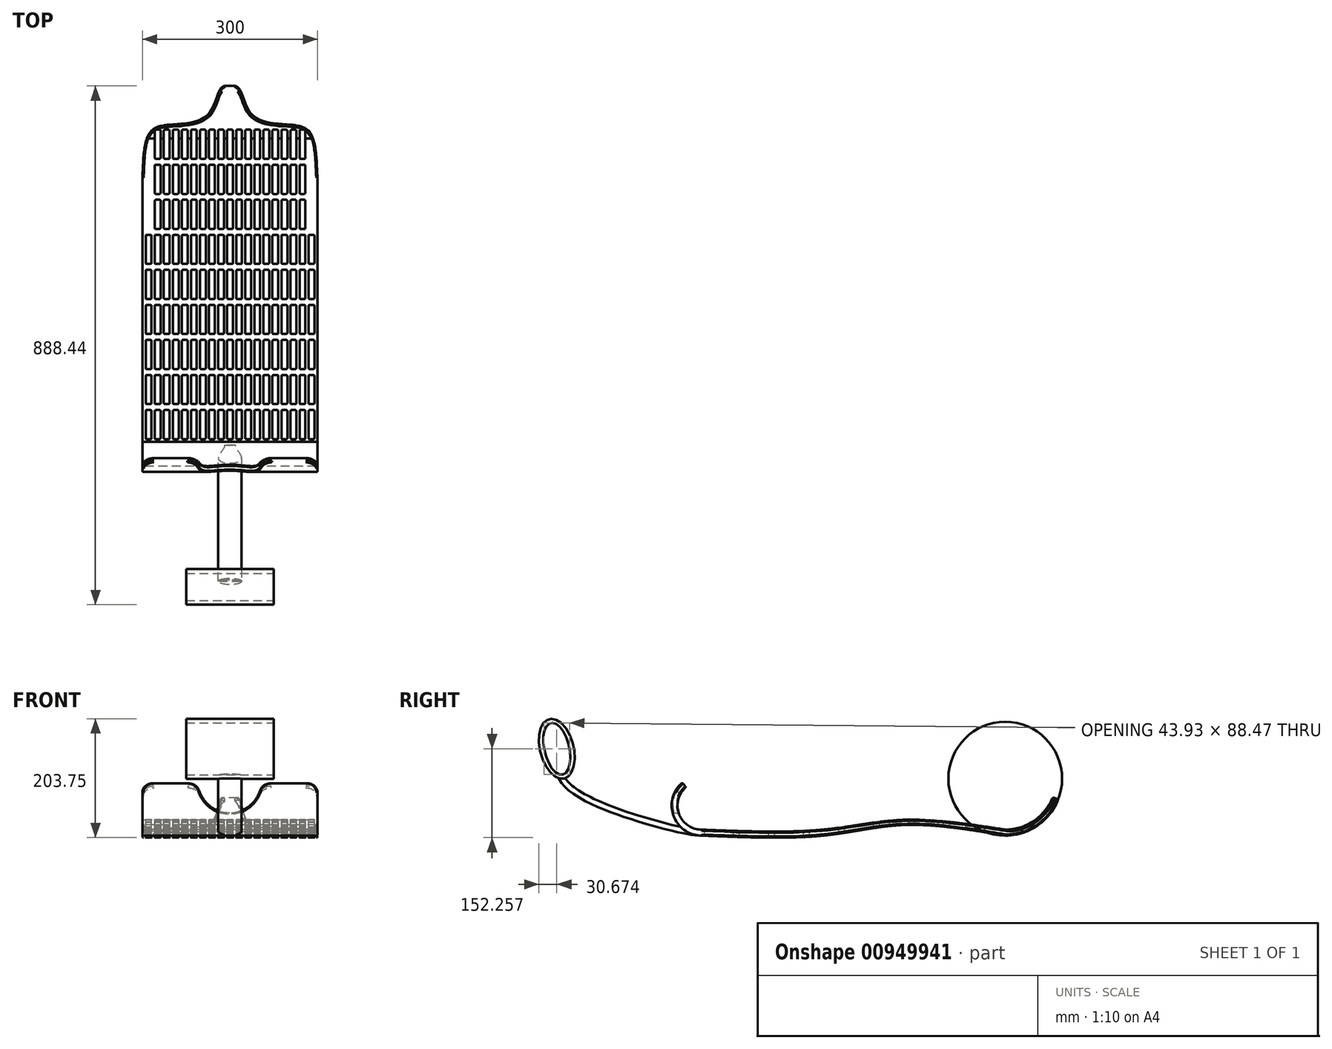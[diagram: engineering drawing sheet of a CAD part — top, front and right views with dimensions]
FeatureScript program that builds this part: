
annotation { "Feature Type Name" : "Feature", "Feature Type Description" : "" }
export const myFeature = defineFeature(function(context is Context, id is Id, definition is map)
    precondition{}
    {
        {
            var Q0;
            Q0=qCreatedBy(makeId("Right.planeOp"),FACE);
            var sketch = newSketch(context, id + "F0", { "sketchPlane" : qUnion([Q0])});
            skArc(sketch, "E0", {"start": v(0, 0) * mm, "mid": v(54.84, 16.9) * mm, "end": v(90.64, 61.76) * mm});
            skArc(sketch, "E1", {"start": v(-520, 0) * mm, "mid": v(-568.17, 33.63) * mm, "end": v(-553.2, 90.44) * mm});
            skArc(sketch, "E2.0", {"start": v(-520, 10) * mm, "mid": v(-558.78, 37.08) * mm, "end": v(-546.73, 82.82) * mm});
            skArc(sketch, "E2.2", {"start": v(0, 10) * mm, "mid": v(49.2, 25.17) * mm, "end": v(81.33, 65.42) * mm});
            skLineSegment(sketch, "E3", {"start": v(-553.2, 90.44) * mm, "end": v(-546.73, 82.82) * mm});
            skLineSegment(sketch, "E4", {"start": v(81.33, 65.42) * mm, "end": v(90.64, 61.76) * mm});
            skFitSpline(sketch, "E5", {"points": [v(-520, 10) * mm, v(-313.28, 10) * mm, v(-172.96, 26.9) * mm, v(0, 10) * mm], "startDerivative": vector(600.12, -23.53) * mm, "endDerivative": vector(538.4, -83.7) * mm});
            skFitSpline(sketch, "E6", {"points": [v(-520, 0) * mm, v(-310.97, 0) * mm, v(-172.96, 18.13) * mm, v(0, 0) * mm], "startDerivative": vector(605.75, -25.5) * mm, "endDerivative": vector(539.73, -90) * mm});
            skSolve(sketch);
        }
        {
            var Q0;
            Q0=makeQuery(id+"F0.imprint","IMPRINT",FACE,{"disambiguationData":[TD([[makeQuery(id+"F0.imprint","IMPRINT",EDGE,{"derivedFrom":sQuery(id+"F0.wireOp",EDGE,"GC1lfuyi-SQlX-Y11Y-IKv3-B2b0vn97BP75")}),-1.0]])]});
            var Q1;
            Q1=makeQuery(id+"F0.imprint","IMPRINT",FACE,{"disambiguationData":[TD([[makeQuery(id+"F0.imprint","IMPRINT",EDGE,{"derivedFrom":sQuery(id+"F0.wireOp",EDGE,"E0")}),1.0]])]});
            extrude(context, id + "F1", {"entities" : qUnion([Q0, Q1]), "depth" : 300 * mm, "offsetDistance" : 25 * mm});
        }
        {
            var Q0;
            Q0=qCreatedBy(makeId("Front.planeOp"),FACE);
            var sketch = newSketch(context, id + "F2", { "sketchPlane" : qUnion([Q0])});
            skCircle(sketch, "E7", {"center": v(149.46, 93.55) * mm, "radius": 54.72 * mm});
            skSolve(sketch);
        }
        {
            var Q0;
            Q0 = qSketchRegion(id + "F2", true);
            extrude(context, id + "F3", {"entities" : qUnion([Q0]), "operationType" : NewBodyOperationType.REMOVE, "endBound" : BoundingType.THROUGH_ALL, "depth" : 25 * mm, "offsetDistance" : 25 * mm});
        }
        {
            var Q0;
            Q0=makeQuery(id+"F3.boolean.opBoolean","INTERSECT",EDGE,{"disambiguationData":[OD(0.0)],"derivedFrom":[makeQuery(id+"F1.opExtrude","SWEPT_FACE",FACE,{"disambiguationData":[OSD([sQuery(id+"F0.wireOp",EDGE,"E3")])]}),makeQuery(id+"F3.opExtrude","SWEPT_FACE",FACE,{"disambiguationData":[OSD([sQuery(id+"F2.wireOp",EDGE,"E7")])]})]});
            var Q1;
            Q1=makeQuery(id+"F3.boolean.opBoolean","INTERSECT",EDGE,{"disambiguationData":[OD(1.0)],"derivedFrom":[makeQuery(id+"F1.opExtrude","SWEPT_FACE",FACE,{"disambiguationData":[OSD([sQuery(id+"F0.wireOp",EDGE,"E3")])]}),makeQuery(id+"F3.opExtrude","SWEPT_FACE",FACE,{"disambiguationData":[OSD([sQuery(id+"F2.wireOp",EDGE,"E7")])]})]});
            fillet(context, id + "F4", {"entities" : qUnion([Q0, Q1]), "radius" : 20 * mm, "tangentPropagation" : true, "allowEdgeOverflow" : false});
        }
        {
            var Q0;
            Q0=makeQuery(id+"F1.opExtrude","CAP_EDGE",EDGE,{"disambiguationData":[OSD([sQuery(id+"F0.wireOp",EDGE,"E3")])],"isStart":false});
            var Q1;
            Q1=makeQuery(id+"F1.opExtrude","CAP_EDGE",EDGE,{"disambiguationData":[OSD([sQuery(id+"F0.wireOp",EDGE,"E3")])],"isStart":true});
            fillet(context, id + "F5", {"entities" : qUnion([Q0, Q1]), "radius" : 20 * mm, "tangentPropagation" : true, "allowEdgeOverflow" : false});
        }
        {
            var Q0;
            Q0=qCreatedBy(makeId("Front.planeOp"),FACE);
            cPlane(context, id + "F6", {"entities" : qUnion([Q0]), "cplaneType" : CPlaneType.OFFSET, "offset" : 526 * mm, "width" : 150 * mm, "height" : 150 * mm});
        }
        {
            var Q0;
            Q0=qCreatedBy(makeId("Right.planeOp"),FACE);
            cPlane(context, id + "F7", {"entities" : qUnion([Q0]), "cplaneType" : CPlaneType.OFFSET, "offset" : 150 * mm, "width" : 150 * mm, "height" : 150 * mm});
        }
        {
            var Q0;
            Q0=qCreatedBy(id+"F7.planeOp",FACE);
            var sketch = newSketch(context, id + "F8", { "sketchPlane" : qUnion([Q0])});
            skFitSpline(sketch, "E8", {"points": [v(-525.68, 4.57) * mm, v(-580.72, 15.5) * mm, v(-760.94, 103.52) * mm], "startDerivative": vector(-124.59, 16.55) * mm, "endDerivative": vector(-36.47, 177.5) * mm});
            skSolve(sketch);
        }
        {
            var Q0;
            Q0=qCreatedBy(id+"F6.planeOp",FACE);
            var sketch = newSketch(context, id + "F9", { "sketchPlane" : qUnion([Q0])});
            skEllipse(sketch, "E9", {"center": v(150.13, 4.74) * mm, "majorRadius": 20 * mm, "minorRadius": 5 * mm, "majorAxis": v(1, 0)});
            skSolve(sketch);
        }
        {
            var Q0;
            Q0 = qSketchRegion(id + "F9", true);
            var Q1;
            Q1=sQuery(id+"F8.wireOp",EDGE,"E8");
            sweep(context, id + "F10", {"operationType" : NewBodyOperationType.ADD, "profiles" : qUnion([Q0]), "path" : qUnion([Q1])});
        }
        {
            var Q0;
            Q0=qCreatedBy(makeId("Right.planeOp"),FACE);
            cPlane(context, id + "F11", {"entities" : qUnion([Q0]), "cplaneType" : CPlaneType.OFFSET, "offset" : 150 * mm, "width" : 150 * mm, "height" : 150 * mm});
        }
        {
            var Q0;
            Q0=qCreatedBy(id+"F11.planeOp",FACE);
            var sketch = newSketch(context, id + "F12", { "sketchPlane" : qUnion([Q0])});
            skEllipse(sketch, "E10", {"center": v(-768.07, 148.66) * mm, "majorRadius": 52.59 * mm, "minorRadius": 28.75 * mm, "majorAxis": v(0.24, -0.97)});
            skEllipse(sketch, "E11", {"center": v(-768.07, 148.66) * mm, "majorRadius": 45.41 * mm, "minorRadius": 21.36 * mm, "majorAxis": v(0.23, -0.97)});
            skSolve(sketch);
        }
        {
            var Q0;
            Q0 = qSketchRegion(id + "F12", true);
            extrude(context, id + "F13", {"entities" : qUnion([Q0]), "operationType" : NewBodyOperationType.ADD, "depth" : 150 * mm, "offsetDistance" : 25 * mm, "symmetric" : true});
        }
        {
            var Q0;
            Q0=qCreatedBy(makeId("Top.planeOp"),FACE);
            var sketch = newSketch(context, id + "F14", { "sketchPlane" : qUnion([Q0])});
            skLineSegment(sketch, "E12.bottom", {"start": v(7.77, -515.2) * mm, "end": v(13.77, -515.2) * mm});
            skLineSegment(sketch, "E12.top", {"start": v(7.77, -465.2) * mm, "end": v(13.77, -465.2) * mm});
            skLineSegment(sketch, "E12.left", {"start": v(5.77, -513.2) * mm, "end": v(5.77, -467.2) * mm});
            skLineSegment(sketch, "E12.right", {"start": v(15.77, -513.2) * mm, "end": v(15.77, -467.2) * mm});
            skPoint(sketch, "E13.visualSharp", {"position": v(15.77, -465.2) * mm});
            skArc(sketch, "E13.filletArc", {"start": v(15.77, -467.2) * mm, "mid": v(15.18, -465.8) * mm, "end": v(13.77, -465.2) * mm});
            skPoint(sketch, "E14.visualSharp", {"position": v(5.77, -465.2) * mm});
            skArc(sketch, "E14.filletArc", {"start": v(7.77, -465.2) * mm, "mid": v(6.35, -465.8) * mm, "end": v(5.77, -467.2) * mm});
            skPoint(sketch, "E15.visualSharp", {"position": v(5.77, -515.2) * mm});
            skArc(sketch, "E15.filletArc", {"start": v(5.77, -513.2) * mm, "mid": v(6.35, -514.62) * mm, "end": v(7.77, -515.2) * mm});
            skPoint(sketch, "E16.visualSharp", {"position": v(15.77, -515.2) * mm});
            skArc(sketch, "E16.filletArc", {"start": v(13.77, -515.2) * mm, "mid": v(15.18, -514.62) * mm, "end": v(15.77, -513.2) * mm});
            skLineSegment(sketch, "E17.0.1.0", {"start": v(15.77, -453.2) * mm, "end": v(15.77, -407.2) * mm});
            skPoint(sketch, "E17.0.1.1", {"position": v(5.77, -455.2) * mm});
            skLineSegment(sketch, "E17.0.1.2", {"start": v(5.77, -453.2) * mm, "end": v(5.77, -407.2) * mm});
            skArc(sketch, "E17.0.1.3", {"start": v(5.77, -453.2) * mm, "mid": v(6.35, -454.62) * mm, "end": v(7.77, -455.2) * mm});
            skPoint(sketch, "E17.0.1.4", {"position": v(15.77, -455.2) * mm});
            skPoint(sketch, "E17.0.1.5", {"position": v(5.77, -405.2) * mm});
            skLineSegment(sketch, "E17.0.1.6", {"start": v(7.77, -405.2) * mm, "end": v(13.77, -405.2) * mm});
            skLineSegment(sketch, "E17.0.1.7", {"start": v(7.77, -455.2) * mm, "end": v(13.77, -455.2) * mm});
            skPoint(sketch, "E17.0.1.8", {"position": v(15.77, -405.2) * mm});
            skArc(sketch, "E17.0.1.9", {"start": v(15.77, -407.2) * mm, "mid": v(15.18, -405.8) * mm, "end": v(13.77, -405.2) * mm});
            skArc(sketch, "E17.0.1.10", {"start": v(13.77, -455.2) * mm, "mid": v(15.18, -454.62) * mm, "end": v(15.77, -453.2) * mm});
            skArc(sketch, "E17.0.1.11", {"start": v(7.77, -405.2) * mm, "mid": v(6.35, -405.8) * mm, "end": v(5.77, -407.2) * mm});
            skLineSegment(sketch, "E17.0.2.0", {"start": v(15.77, -393.2) * mm, "end": v(15.77, -347.2) * mm});
            skPoint(sketch, "E17.0.2.1", {"position": v(5.77, -395.2) * mm});
            skLineSegment(sketch, "E17.0.2.2", {"start": v(5.77, -393.2) * mm, "end": v(5.77, -347.2) * mm});
            skArc(sketch, "E17.0.2.3", {"start": v(5.77, -393.2) * mm, "mid": v(6.35, -394.62) * mm, "end": v(7.77, -395.2) * mm});
            skPoint(sketch, "E17.0.2.4", {"position": v(15.77, -395.2) * mm});
            skPoint(sketch, "E17.0.2.5", {"position": v(5.77, -345.2) * mm});
            skLineSegment(sketch, "E17.0.2.6", {"start": v(7.77, -345.2) * mm, "end": v(13.77, -345.2) * mm});
            skLineSegment(sketch, "E17.0.2.7", {"start": v(7.77, -395.2) * mm, "end": v(13.77, -395.2) * mm});
            skPoint(sketch, "E17.0.2.8", {"position": v(15.77, -345.2) * mm});
            skArc(sketch, "E17.0.2.9", {"start": v(15.77, -347.2) * mm, "mid": v(15.18, -345.8) * mm, "end": v(13.77, -345.2) * mm});
            skArc(sketch, "E17.0.2.10", {"start": v(13.77, -395.2) * mm, "mid": v(15.18, -394.62) * mm, "end": v(15.77, -393.2) * mm});
            skArc(sketch, "E17.0.2.11", {"start": v(7.77, -345.2) * mm, "mid": v(6.35, -345.8) * mm, "end": v(5.77, -347.2) * mm});
            skLineSegment(sketch, "E17.0.3.0", {"start": v(15.77, -333.2) * mm, "end": v(15.77, -287.2) * mm});
            skPoint(sketch, "E17.0.3.1", {"position": v(5.77, -335.2) * mm});
            skLineSegment(sketch, "E17.0.3.2", {"start": v(5.77, -333.2) * mm, "end": v(5.77, -287.2) * mm});
            skArc(sketch, "E17.0.3.3", {"start": v(5.77, -333.2) * mm, "mid": v(6.35, -334.62) * mm, "end": v(7.77, -335.2) * mm});
            skPoint(sketch, "E17.0.3.4", {"position": v(15.77, -335.2) * mm});
            skPoint(sketch, "E17.0.3.5", {"position": v(5.77, -285.2) * mm});
            skLineSegment(sketch, "E17.0.3.6", {"start": v(7.77, -285.2) * mm, "end": v(13.77, -285.2) * mm});
            skLineSegment(sketch, "E17.0.3.7", {"start": v(7.77, -335.2) * mm, "end": v(13.77, -335.2) * mm});
            skPoint(sketch, "E17.0.3.8", {"position": v(15.77, -285.2) * mm});
            skArc(sketch, "E17.0.3.9", {"start": v(15.77, -287.2) * mm, "mid": v(15.18, -285.8) * mm, "end": v(13.77, -285.2) * mm});
            skArc(sketch, "E17.0.3.10", {"start": v(13.77, -335.2) * mm, "mid": v(15.18, -334.62) * mm, "end": v(15.77, -333.2) * mm});
            skArc(sketch, "E17.0.3.11", {"start": v(7.77, -285.2) * mm, "mid": v(6.35, -285.8) * mm, "end": v(5.77, -287.2) * mm});
            skLineSegment(sketch, "E17.0.4.0", {"start": v(15.77, -273.2) * mm, "end": v(15.77, -227.2) * mm});
            skPoint(sketch, "E17.0.4.1", {"position": v(5.77, -275.2) * mm});
            skLineSegment(sketch, "E17.0.4.2", {"start": v(5.77, -273.2) * mm, "end": v(5.77, -227.2) * mm});
            skArc(sketch, "E17.0.4.3", {"start": v(5.77, -273.2) * mm, "mid": v(6.35, -274.62) * mm, "end": v(7.77, -275.2) * mm});
            skPoint(sketch, "E17.0.4.4", {"position": v(15.77, -275.2) * mm});
            skPoint(sketch, "E17.0.4.5", {"position": v(5.77, -225.2) * mm});
            skLineSegment(sketch, "E17.0.4.6", {"start": v(7.77, -225.2) * mm, "end": v(13.77, -225.2) * mm});
            skLineSegment(sketch, "E17.0.4.7", {"start": v(7.77, -275.2) * mm, "end": v(13.77, -275.2) * mm});
            skPoint(sketch, "E17.0.4.8", {"position": v(15.77, -225.2) * mm});
            skArc(sketch, "E17.0.4.9", {"start": v(15.77, -227.2) * mm, "mid": v(15.18, -225.8) * mm, "end": v(13.77, -225.2) * mm});
            skArc(sketch, "E17.0.4.10", {"start": v(13.77, -275.2) * mm, "mid": v(15.18, -274.62) * mm, "end": v(15.77, -273.2) * mm});
            skArc(sketch, "E17.0.4.11", {"start": v(7.77, -225.2) * mm, "mid": v(6.35, -225.8) * mm, "end": v(5.77, -227.2) * mm});
            skLineSegment(sketch, "E17.1.0.0", {"start": v(31.27, -513.2) * mm, "end": v(31.27, -467.2) * mm});
            skPoint(sketch, "E17.1.0.1", {"position": v(21.27, -515.2) * mm});
            skLineSegment(sketch, "E17.1.0.2", {"start": v(21.27, -513.2) * mm, "end": v(21.27, -467.2) * mm});
            skArc(sketch, "E17.1.0.3", {"start": v(21.27, -513.2) * mm, "mid": v(21.85, -514.62) * mm, "end": v(23.27, -515.2) * mm});
            skPoint(sketch, "E17.1.0.4", {"position": v(31.27, -515.2) * mm});
            skPoint(sketch, "E17.1.0.5", {"position": v(21.27, -465.2) * mm});
            skLineSegment(sketch, "E17.1.0.6", {"start": v(23.27, -465.2) * mm, "end": v(29.27, -465.2) * mm});
            skLineSegment(sketch, "E17.1.0.7", {"start": v(23.27, -515.2) * mm, "end": v(29.27, -515.2) * mm});
            skPoint(sketch, "E17.1.0.8", {"position": v(31.27, -465.2) * mm});
            skArc(sketch, "E17.1.0.9", {"start": v(31.27, -467.2) * mm, "mid": v(30.68, -465.8) * mm, "end": v(29.27, -465.2) * mm});
            skArc(sketch, "E17.1.0.10", {"start": v(29.27, -515.2) * mm, "mid": v(30.68, -514.62) * mm, "end": v(31.27, -513.2) * mm});
            skArc(sketch, "E17.1.0.11", {"start": v(23.27, -465.2) * mm, "mid": v(21.85, -465.8) * mm, "end": v(21.27, -467.2) * mm});
            skLineSegment(sketch, "E17.1.1.0", {"start": v(31.27, -453.2) * mm, "end": v(31.27, -407.2) * mm});
            skPoint(sketch, "E17.1.1.1", {"position": v(21.27, -455.2) * mm});
            skLineSegment(sketch, "E17.1.1.2", {"start": v(21.27, -453.2) * mm, "end": v(21.27, -407.2) * mm});
            skArc(sketch, "E17.1.1.3", {"start": v(21.27, -453.2) * mm, "mid": v(21.85, -454.62) * mm, "end": v(23.27, -455.2) * mm});
            skPoint(sketch, "E17.1.1.4", {"position": v(31.27, -455.2) * mm});
            skPoint(sketch, "E17.1.1.5", {"position": v(21.27, -405.2) * mm});
            skLineSegment(sketch, "E17.1.1.6", {"start": v(23.27, -405.2) * mm, "end": v(29.27, -405.2) * mm});
            skLineSegment(sketch, "E17.1.1.7", {"start": v(23.27, -455.2) * mm, "end": v(29.27, -455.2) * mm});
            skPoint(sketch, "E17.1.1.8", {"position": v(31.27, -405.2) * mm});
            skArc(sketch, "E17.1.1.9", {"start": v(31.27, -407.2) * mm, "mid": v(30.68, -405.8) * mm, "end": v(29.27, -405.2) * mm});
            skArc(sketch, "E17.1.1.10", {"start": v(29.27, -455.2) * mm, "mid": v(30.68, -454.62) * mm, "end": v(31.27, -453.2) * mm});
            skArc(sketch, "E17.1.1.11", {"start": v(23.27, -405.2) * mm, "mid": v(21.85, -405.8) * mm, "end": v(21.27, -407.2) * mm});
            skLineSegment(sketch, "E17.1.2.0", {"start": v(31.27, -393.2) * mm, "end": v(31.27, -347.2) * mm});
            skPoint(sketch, "E17.1.2.1", {"position": v(21.27, -395.2) * mm});
            skLineSegment(sketch, "E17.1.2.2", {"start": v(21.27, -393.2) * mm, "end": v(21.27, -347.2) * mm});
            skArc(sketch, "E17.1.2.3", {"start": v(21.27, -393.2) * mm, "mid": v(21.85, -394.62) * mm, "end": v(23.27, -395.2) * mm});
            skPoint(sketch, "E17.1.2.4", {"position": v(31.27, -395.2) * mm});
            skPoint(sketch, "E17.1.2.5", {"position": v(21.27, -345.2) * mm});
            skLineSegment(sketch, "E17.1.2.6", {"start": v(23.27, -345.2) * mm, "end": v(29.27, -345.2) * mm});
            skLineSegment(sketch, "E17.1.2.7", {"start": v(23.27, -395.2) * mm, "end": v(29.27, -395.2) * mm});
            skPoint(sketch, "E17.1.2.8", {"position": v(31.27, -345.2) * mm});
            skArc(sketch, "E17.1.2.9", {"start": v(31.27, -347.2) * mm, "mid": v(30.68, -345.8) * mm, "end": v(29.27, -345.2) * mm});
            skArc(sketch, "E17.1.2.10", {"start": v(29.27, -395.2) * mm, "mid": v(30.68, -394.62) * mm, "end": v(31.27, -393.2) * mm});
            skArc(sketch, "E17.1.2.11", {"start": v(23.27, -345.2) * mm, "mid": v(21.85, -345.8) * mm, "end": v(21.27, -347.2) * mm});
            skLineSegment(sketch, "E17.1.3.0", {"start": v(31.27, -333.2) * mm, "end": v(31.27, -287.2) * mm});
            skPoint(sketch, "E17.1.3.1", {"position": v(21.27, -335.2) * mm});
            skLineSegment(sketch, "E17.1.3.2", {"start": v(21.27, -333.2) * mm, "end": v(21.27, -287.2) * mm});
            skArc(sketch, "E17.1.3.3", {"start": v(21.27, -333.2) * mm, "mid": v(21.85, -334.62) * mm, "end": v(23.27, -335.2) * mm});
            skPoint(sketch, "E17.1.3.4", {"position": v(31.27, -335.2) * mm});
            skPoint(sketch, "E17.1.3.5", {"position": v(21.27, -285.2) * mm});
            skLineSegment(sketch, "E17.1.3.6", {"start": v(23.27, -285.2) * mm, "end": v(29.27, -285.2) * mm});
            skLineSegment(sketch, "E17.1.3.7", {"start": v(23.27, -335.2) * mm, "end": v(29.27, -335.2) * mm});
            skPoint(sketch, "E17.1.3.8", {"position": v(31.27, -285.2) * mm});
            skArc(sketch, "E17.1.3.9", {"start": v(31.27, -287.2) * mm, "mid": v(30.68, -285.8) * mm, "end": v(29.27, -285.2) * mm});
            skArc(sketch, "E17.1.3.10", {"start": v(29.27, -335.2) * mm, "mid": v(30.68, -334.62) * mm, "end": v(31.27, -333.2) * mm});
            skArc(sketch, "E17.1.3.11", {"start": v(23.27, -285.2) * mm, "mid": v(21.85, -285.8) * mm, "end": v(21.27, -287.2) * mm});
            skLineSegment(sketch, "E17.1.4.0", {"start": v(31.27, -273.2) * mm, "end": v(31.27, -227.2) * mm});
            skPoint(sketch, "E17.1.4.1", {"position": v(21.27, -275.2) * mm});
            skLineSegment(sketch, "E17.1.4.2", {"start": v(21.27, -273.2) * mm, "end": v(21.27, -227.2) * mm});
            skArc(sketch, "E17.1.4.3", {"start": v(21.27, -273.2) * mm, "mid": v(21.85, -274.62) * mm, "end": v(23.27, -275.2) * mm});
            skPoint(sketch, "E17.1.4.4", {"position": v(31.27, -275.2) * mm});
            skPoint(sketch, "E17.1.4.5", {"position": v(21.27, -225.2) * mm});
            skLineSegment(sketch, "E17.1.4.6", {"start": v(23.27, -225.2) * mm, "end": v(29.27, -225.2) * mm});
            skLineSegment(sketch, "E17.1.4.7", {"start": v(23.27, -275.2) * mm, "end": v(29.27, -275.2) * mm});
            skPoint(sketch, "E17.1.4.8", {"position": v(31.27, -225.2) * mm});
            skArc(sketch, "E17.1.4.9", {"start": v(31.27, -227.2) * mm, "mid": v(30.68, -225.8) * mm, "end": v(29.27, -225.2) * mm});
            skArc(sketch, "E17.1.4.10", {"start": v(29.27, -275.2) * mm, "mid": v(30.68, -274.62) * mm, "end": v(31.27, -273.2) * mm});
            skArc(sketch, "E17.1.4.11", {"start": v(23.27, -225.2) * mm, "mid": v(21.85, -225.8) * mm, "end": v(21.27, -227.2) * mm});
            skLineSegment(sketch, "E17.2.0.0", {"start": v(46.77, -513.2) * mm, "end": v(46.77, -467.2) * mm});
            skPoint(sketch, "E17.2.0.1", {"position": v(36.77, -515.2) * mm});
            skLineSegment(sketch, "E17.2.0.2", {"start": v(36.77, -513.2) * mm, "end": v(36.77, -467.2) * mm});
            skArc(sketch, "E17.2.0.3", {"start": v(36.77, -513.2) * mm, "mid": v(37.35, -514.62) * mm, "end": v(38.77, -515.2) * mm});
            skPoint(sketch, "E17.2.0.4", {"position": v(46.77, -515.2) * mm});
            skPoint(sketch, "E17.2.0.5", {"position": v(36.77, -465.2) * mm});
            skLineSegment(sketch, "E17.2.0.6", {"start": v(38.77, -465.2) * mm, "end": v(44.77, -465.2) * mm});
            skLineSegment(sketch, "E17.2.0.7", {"start": v(38.77, -515.2) * mm, "end": v(44.77, -515.2) * mm});
            skPoint(sketch, "E17.2.0.8", {"position": v(46.77, -465.2) * mm});
            skArc(sketch, "E17.2.0.9", {"start": v(46.77, -467.2) * mm, "mid": v(46.18, -465.8) * mm, "end": v(44.77, -465.2) * mm});
            skArc(sketch, "E17.2.0.10", {"start": v(44.77, -515.2) * mm, "mid": v(46.18, -514.62) * mm, "end": v(46.77, -513.2) * mm});
            skArc(sketch, "E17.2.0.11", {"start": v(38.77, -465.2) * mm, "mid": v(37.35, -465.8) * mm, "end": v(36.77, -467.2) * mm});
            skLineSegment(sketch, "E17.2.1.0", {"start": v(46.77, -453.2) * mm, "end": v(46.77, -407.2) * mm});
            skPoint(sketch, "E17.2.1.1", {"position": v(36.77, -455.2) * mm});
            skLineSegment(sketch, "E17.2.1.2", {"start": v(36.77, -453.2) * mm, "end": v(36.77, -407.2) * mm});
            skArc(sketch, "E17.2.1.3", {"start": v(36.77, -453.2) * mm, "mid": v(37.35, -454.62) * mm, "end": v(38.77, -455.2) * mm});
            skPoint(sketch, "E17.2.1.4", {"position": v(46.77, -455.2) * mm});
            skPoint(sketch, "E17.2.1.5", {"position": v(36.77, -405.2) * mm});
            skLineSegment(sketch, "E17.2.1.6", {"start": v(38.77, -405.2) * mm, "end": v(44.77, -405.2) * mm});
            skLineSegment(sketch, "E17.2.1.7", {"start": v(38.77, -455.2) * mm, "end": v(44.77, -455.2) * mm});
            skPoint(sketch, "E17.2.1.8", {"position": v(46.77, -405.2) * mm});
            skArc(sketch, "E17.2.1.9", {"start": v(46.77, -407.2) * mm, "mid": v(46.18, -405.8) * mm, "end": v(44.77, -405.2) * mm});
            skArc(sketch, "E17.2.1.10", {"start": v(44.77, -455.2) * mm, "mid": v(46.18, -454.62) * mm, "end": v(46.77, -453.2) * mm});
            skArc(sketch, "E17.2.1.11", {"start": v(38.77, -405.2) * mm, "mid": v(37.35, -405.8) * mm, "end": v(36.77, -407.2) * mm});
            skLineSegment(sketch, "E17.2.2.0", {"start": v(46.77, -393.2) * mm, "end": v(46.77, -347.2) * mm});
            skPoint(sketch, "E17.2.2.1", {"position": v(36.77, -395.2) * mm});
            skLineSegment(sketch, "E17.2.2.2", {"start": v(36.77, -393.2) * mm, "end": v(36.77, -347.2) * mm});
            skArc(sketch, "E17.2.2.3", {"start": v(36.77, -393.2) * mm, "mid": v(37.35, -394.62) * mm, "end": v(38.77, -395.2) * mm});
            skPoint(sketch, "E17.2.2.4", {"position": v(46.77, -395.2) * mm});
            skPoint(sketch, "E17.2.2.5", {"position": v(36.77, -345.2) * mm});
            skLineSegment(sketch, "E17.2.2.6", {"start": v(38.77, -345.2) * mm, "end": v(44.77, -345.2) * mm});
            skLineSegment(sketch, "E17.2.2.7", {"start": v(38.77, -395.2) * mm, "end": v(44.77, -395.2) * mm});
            skPoint(sketch, "E17.2.2.8", {"position": v(46.77, -345.2) * mm});
            skArc(sketch, "E17.2.2.9", {"start": v(46.77, -347.2) * mm, "mid": v(46.18, -345.8) * mm, "end": v(44.77, -345.2) * mm});
            skArc(sketch, "E17.2.2.10", {"start": v(44.77, -395.2) * mm, "mid": v(46.18, -394.62) * mm, "end": v(46.77, -393.2) * mm});
            skArc(sketch, "E17.2.2.11", {"start": v(38.77, -345.2) * mm, "mid": v(37.35, -345.8) * mm, "end": v(36.77, -347.2) * mm});
            skLineSegment(sketch, "E17.2.3.0", {"start": v(46.77, -333.2) * mm, "end": v(46.77, -287.2) * mm});
            skPoint(sketch, "E17.2.3.1", {"position": v(36.77, -335.2) * mm});
            skLineSegment(sketch, "E17.2.3.2", {"start": v(36.77, -333.2) * mm, "end": v(36.77, -287.2) * mm});
            skArc(sketch, "E17.2.3.3", {"start": v(36.77, -333.2) * mm, "mid": v(37.35, -334.62) * mm, "end": v(38.77, -335.2) * mm});
            skPoint(sketch, "E17.2.3.4", {"position": v(46.77, -335.2) * mm});
            skPoint(sketch, "E17.2.3.5", {"position": v(36.77, -285.2) * mm});
            skLineSegment(sketch, "E17.2.3.6", {"start": v(38.77, -285.2) * mm, "end": v(44.77, -285.2) * mm});
            skLineSegment(sketch, "E17.2.3.7", {"start": v(38.77, -335.2) * mm, "end": v(44.77, -335.2) * mm});
            skPoint(sketch, "E17.2.3.8", {"position": v(46.77, -285.2) * mm});
            skArc(sketch, "E17.2.3.9", {"start": v(46.77, -287.2) * mm, "mid": v(46.18, -285.8) * mm, "end": v(44.77, -285.2) * mm});
            skArc(sketch, "E17.2.3.10", {"start": v(44.77, -335.2) * mm, "mid": v(46.18, -334.62) * mm, "end": v(46.77, -333.2) * mm});
            skArc(sketch, "E17.2.3.11", {"start": v(38.77, -285.2) * mm, "mid": v(37.35, -285.8) * mm, "end": v(36.77, -287.2) * mm});
            skLineSegment(sketch, "E17.2.4.0", {"start": v(46.77, -273.2) * mm, "end": v(46.77, -227.2) * mm});
            skPoint(sketch, "E17.2.4.1", {"position": v(36.77, -275.2) * mm});
            skLineSegment(sketch, "E17.2.4.2", {"start": v(36.77, -273.2) * mm, "end": v(36.77, -227.2) * mm});
            skArc(sketch, "E17.2.4.3", {"start": v(36.77, -273.2) * mm, "mid": v(37.35, -274.62) * mm, "end": v(38.77, -275.2) * mm});
            skPoint(sketch, "E17.2.4.4", {"position": v(46.77, -275.2) * mm});
            skPoint(sketch, "E17.2.4.5", {"position": v(36.77, -225.2) * mm});
            skLineSegment(sketch, "E17.2.4.6", {"start": v(38.77, -225.2) * mm, "end": v(44.77, -225.2) * mm});
            skLineSegment(sketch, "E17.2.4.7", {"start": v(38.77, -275.2) * mm, "end": v(44.77, -275.2) * mm});
            skPoint(sketch, "E17.2.4.8", {"position": v(46.77, -225.2) * mm});
            skArc(sketch, "E17.2.4.9", {"start": v(46.77, -227.2) * mm, "mid": v(46.18, -225.8) * mm, "end": v(44.77, -225.2) * mm});
            skArc(sketch, "E17.2.4.10", {"start": v(44.77, -275.2) * mm, "mid": v(46.18, -274.62) * mm, "end": v(46.77, -273.2) * mm});
            skArc(sketch, "E17.2.4.11", {"start": v(38.77, -225.2) * mm, "mid": v(37.35, -225.8) * mm, "end": v(36.77, -227.2) * mm});
            skLineSegment(sketch, "E17.3.0.0", {"start": v(62.27, -513.2) * mm, "end": v(62.27, -467.2) * mm});
            skPoint(sketch, "E17.3.0.1", {"position": v(52.27, -515.2) * mm});
            skLineSegment(sketch, "E17.3.0.2", {"start": v(52.27, -513.2) * mm, "end": v(52.27, -467.2) * mm});
            skArc(sketch, "E17.3.0.3", {"start": v(52.27, -513.2) * mm, "mid": v(52.85, -514.62) * mm, "end": v(54.27, -515.2) * mm});
            skPoint(sketch, "E17.3.0.4", {"position": v(62.27, -515.2) * mm});
            skPoint(sketch, "E17.3.0.5", {"position": v(52.27, -465.2) * mm});
            skLineSegment(sketch, "E17.3.0.6", {"start": v(54.27, -465.2) * mm, "end": v(60.27, -465.2) * mm});
            skLineSegment(sketch, "E17.3.0.7", {"start": v(54.27, -515.2) * mm, "end": v(60.27, -515.2) * mm});
            skPoint(sketch, "E17.3.0.8", {"position": v(62.27, -465.2) * mm});
            skArc(sketch, "E17.3.0.9", {"start": v(62.27, -467.2) * mm, "mid": v(61.68, -465.8) * mm, "end": v(60.27, -465.2) * mm});
            skArc(sketch, "E17.3.0.10", {"start": v(60.27, -515.2) * mm, "mid": v(61.68, -514.62) * mm, "end": v(62.27, -513.2) * mm});
            skArc(sketch, "E17.3.0.11", {"start": v(54.27, -465.2) * mm, "mid": v(52.85, -465.8) * mm, "end": v(52.27, -467.2) * mm});
            skLineSegment(sketch, "E17.3.1.0", {"start": v(62.27, -453.2) * mm, "end": v(62.27, -407.2) * mm});
            skPoint(sketch, "E17.3.1.1", {"position": v(52.27, -455.2) * mm});
            skLineSegment(sketch, "E17.3.1.2", {"start": v(52.27, -453.2) * mm, "end": v(52.27, -407.2) * mm});
            skArc(sketch, "E17.3.1.3", {"start": v(52.27, -453.2) * mm, "mid": v(52.85, -454.62) * mm, "end": v(54.27, -455.2) * mm});
            skPoint(sketch, "E17.3.1.4", {"position": v(62.27, -455.2) * mm});
            skPoint(sketch, "E17.3.1.5", {"position": v(52.27, -405.2) * mm});
            skLineSegment(sketch, "E17.3.1.6", {"start": v(54.27, -405.2) * mm, "end": v(60.27, -405.2) * mm});
            skLineSegment(sketch, "E17.3.1.7", {"start": v(54.27, -455.2) * mm, "end": v(60.27, -455.2) * mm});
            skPoint(sketch, "E17.3.1.8", {"position": v(62.27, -405.2) * mm});
            skArc(sketch, "E17.3.1.9", {"start": v(62.27, -407.2) * mm, "mid": v(61.68, -405.8) * mm, "end": v(60.27, -405.2) * mm});
            skArc(sketch, "E17.3.1.10", {"start": v(60.27, -455.2) * mm, "mid": v(61.68, -454.62) * mm, "end": v(62.27, -453.2) * mm});
            skArc(sketch, "E17.3.1.11", {"start": v(54.27, -405.2) * mm, "mid": v(52.85, -405.8) * mm, "end": v(52.27, -407.2) * mm});
            skLineSegment(sketch, "E17.3.2.0", {"start": v(62.27, -393.2) * mm, "end": v(62.27, -347.2) * mm});
            skPoint(sketch, "E17.3.2.1", {"position": v(52.27, -395.2) * mm});
            skLineSegment(sketch, "E17.3.2.2", {"start": v(52.27, -393.2) * mm, "end": v(52.27, -347.2) * mm});
            skArc(sketch, "E17.3.2.3", {"start": v(52.27, -393.2) * mm, "mid": v(52.85, -394.62) * mm, "end": v(54.27, -395.2) * mm});
            skPoint(sketch, "E17.3.2.4", {"position": v(62.27, -395.2) * mm});
            skPoint(sketch, "E17.3.2.5", {"position": v(52.27, -345.2) * mm});
            skLineSegment(sketch, "E17.3.2.6", {"start": v(54.27, -345.2) * mm, "end": v(60.27, -345.2) * mm});
            skLineSegment(sketch, "E17.3.2.7", {"start": v(54.27, -395.2) * mm, "end": v(60.27, -395.2) * mm});
            skPoint(sketch, "E17.3.2.8", {"position": v(62.27, -345.2) * mm});
            skArc(sketch, "E17.3.2.9", {"start": v(62.27, -347.2) * mm, "mid": v(61.68, -345.8) * mm, "end": v(60.27, -345.2) * mm});
            skArc(sketch, "E17.3.2.10", {"start": v(60.27, -395.2) * mm, "mid": v(61.68, -394.62) * mm, "end": v(62.27, -393.2) * mm});
            skArc(sketch, "E17.3.2.11", {"start": v(54.27, -345.2) * mm, "mid": v(52.85, -345.8) * mm, "end": v(52.27, -347.2) * mm});
            skLineSegment(sketch, "E17.3.3.0", {"start": v(62.27, -333.2) * mm, "end": v(62.27, -287.2) * mm});
            skPoint(sketch, "E17.3.3.1", {"position": v(52.27, -335.2) * mm});
            skLineSegment(sketch, "E17.3.3.2", {"start": v(52.27, -333.2) * mm, "end": v(52.27, -287.2) * mm});
            skArc(sketch, "E17.3.3.3", {"start": v(52.27, -333.2) * mm, "mid": v(52.85, -334.62) * mm, "end": v(54.27, -335.2) * mm});
            skPoint(sketch, "E17.3.3.4", {"position": v(62.27, -335.2) * mm});
            skPoint(sketch, "E17.3.3.5", {"position": v(52.27, -285.2) * mm});
            skLineSegment(sketch, "E17.3.3.6", {"start": v(54.27, -285.2) * mm, "end": v(60.27, -285.2) * mm});
            skLineSegment(sketch, "E17.3.3.7", {"start": v(54.27, -335.2) * mm, "end": v(60.27, -335.2) * mm});
            skPoint(sketch, "E17.3.3.8", {"position": v(62.27, -285.2) * mm});
            skArc(sketch, "E17.3.3.9", {"start": v(62.27, -287.2) * mm, "mid": v(61.68, -285.8) * mm, "end": v(60.27, -285.2) * mm});
            skArc(sketch, "E17.3.3.10", {"start": v(60.27, -335.2) * mm, "mid": v(61.68, -334.62) * mm, "end": v(62.27, -333.2) * mm});
            skArc(sketch, "E17.3.3.11", {"start": v(54.27, -285.2) * mm, "mid": v(52.85, -285.8) * mm, "end": v(52.27, -287.2) * mm});
            skLineSegment(sketch, "E17.3.4.0", {"start": v(62.27, -273.2) * mm, "end": v(62.27, -227.2) * mm});
            skPoint(sketch, "E17.3.4.1", {"position": v(52.27, -275.2) * mm});
            skLineSegment(sketch, "E17.3.4.2", {"start": v(52.27, -273.2) * mm, "end": v(52.27, -227.2) * mm});
            skArc(sketch, "E17.3.4.3", {"start": v(52.27, -273.2) * mm, "mid": v(52.85, -274.62) * mm, "end": v(54.27, -275.2) * mm});
            skPoint(sketch, "E17.3.4.4", {"position": v(62.27, -275.2) * mm});
            skPoint(sketch, "E17.3.4.5", {"position": v(52.27, -225.2) * mm});
            skLineSegment(sketch, "E17.3.4.6", {"start": v(54.27, -225.2) * mm, "end": v(60.27, -225.2) * mm});
            skLineSegment(sketch, "E17.3.4.7", {"start": v(54.27, -275.2) * mm, "end": v(60.27, -275.2) * mm});
            skPoint(sketch, "E17.3.4.8", {"position": v(62.27, -225.2) * mm});
            skArc(sketch, "E17.3.4.9", {"start": v(62.27, -227.2) * mm, "mid": v(61.68, -225.8) * mm, "end": v(60.27, -225.2) * mm});
            skArc(sketch, "E17.3.4.10", {"start": v(60.27, -275.2) * mm, "mid": v(61.68, -274.62) * mm, "end": v(62.27, -273.2) * mm});
            skArc(sketch, "E17.3.4.11", {"start": v(54.27, -225.2) * mm, "mid": v(52.85, -225.8) * mm, "end": v(52.27, -227.2) * mm});
            skLineSegment(sketch, "E17.4.0.0", {"start": v(77.77, -513.2) * mm, "end": v(77.77, -467.2) * mm});
            skPoint(sketch, "E17.4.0.1", {"position": v(67.77, -515.2) * mm});
            skLineSegment(sketch, "E17.4.0.2", {"start": v(67.77, -513.2) * mm, "end": v(67.77, -467.2) * mm});
            skArc(sketch, "E17.4.0.3", {"start": v(67.77, -513.2) * mm, "mid": v(68.35, -514.62) * mm, "end": v(69.77, -515.2) * mm});
            skPoint(sketch, "E17.4.0.4", {"position": v(77.77, -515.2) * mm});
            skPoint(sketch, "E17.4.0.5", {"position": v(67.77, -465.2) * mm});
            skLineSegment(sketch, "E17.4.0.6", {"start": v(69.77, -465.2) * mm, "end": v(75.77, -465.2) * mm});
            skLineSegment(sketch, "E17.4.0.7", {"start": v(69.77, -515.2) * mm, "end": v(75.77, -515.2) * mm});
            skPoint(sketch, "E17.4.0.8", {"position": v(77.77, -465.2) * mm});
            skArc(sketch, "E17.4.0.9", {"start": v(77.77, -467.2) * mm, "mid": v(77.18, -465.8) * mm, "end": v(75.77, -465.2) * mm});
            skArc(sketch, "E17.4.0.10", {"start": v(75.77, -515.2) * mm, "mid": v(77.18, -514.62) * mm, "end": v(77.77, -513.2) * mm});
            skArc(sketch, "E17.4.0.11", {"start": v(69.77, -465.2) * mm, "mid": v(68.35, -465.8) * mm, "end": v(67.77, -467.2) * mm});
            skLineSegment(sketch, "E17.4.1.0", {"start": v(77.77, -453.2) * mm, "end": v(77.77, -407.2) * mm});
            skPoint(sketch, "E17.4.1.1", {"position": v(67.77, -455.2) * mm});
            skLineSegment(sketch, "E17.4.1.2", {"start": v(67.77, -453.2) * mm, "end": v(67.77, -407.2) * mm});
            skArc(sketch, "E17.4.1.3", {"start": v(67.77, -453.2) * mm, "mid": v(68.35, -454.62) * mm, "end": v(69.77, -455.2) * mm});
            skPoint(sketch, "E17.4.1.4", {"position": v(77.77, -455.2) * mm});
            skPoint(sketch, "E17.4.1.5", {"position": v(67.77, -405.2) * mm});
            skLineSegment(sketch, "E17.4.1.6", {"start": v(69.77, -405.2) * mm, "end": v(75.77, -405.2) * mm});
            skLineSegment(sketch, "E17.4.1.7", {"start": v(69.77, -455.2) * mm, "end": v(75.77, -455.2) * mm});
            skPoint(sketch, "E17.4.1.8", {"position": v(77.77, -405.2) * mm});
            skArc(sketch, "E17.4.1.9", {"start": v(77.77, -407.2) * mm, "mid": v(77.18, -405.8) * mm, "end": v(75.77, -405.2) * mm});
            skArc(sketch, "E17.4.1.10", {"start": v(75.77, -455.2) * mm, "mid": v(77.18, -454.62) * mm, "end": v(77.77, -453.2) * mm});
            skArc(sketch, "E17.4.1.11", {"start": v(69.77, -405.2) * mm, "mid": v(68.35, -405.8) * mm, "end": v(67.77, -407.2) * mm});
            skLineSegment(sketch, "E17.4.2.0", {"start": v(77.77, -393.2) * mm, "end": v(77.77, -347.2) * mm});
            skPoint(sketch, "E17.4.2.1", {"position": v(67.77, -395.2) * mm});
            skLineSegment(sketch, "E17.4.2.2", {"start": v(67.77, -393.2) * mm, "end": v(67.77, -347.2) * mm});
            skArc(sketch, "E17.4.2.3", {"start": v(67.77, -393.2) * mm, "mid": v(68.35, -394.62) * mm, "end": v(69.77, -395.2) * mm});
            skPoint(sketch, "E17.4.2.4", {"position": v(77.77, -395.2) * mm});
            skPoint(sketch, "E17.4.2.5", {"position": v(67.77, -345.2) * mm});
            skLineSegment(sketch, "E17.4.2.6", {"start": v(69.77, -345.2) * mm, "end": v(75.77, -345.2) * mm});
            skLineSegment(sketch, "E17.4.2.7", {"start": v(69.77, -395.2) * mm, "end": v(75.77, -395.2) * mm});
            skPoint(sketch, "E17.4.2.8", {"position": v(77.77, -345.2) * mm});
            skArc(sketch, "E17.4.2.9", {"start": v(77.77, -347.2) * mm, "mid": v(77.18, -345.8) * mm, "end": v(75.77, -345.2) * mm});
            skArc(sketch, "E17.4.2.10", {"start": v(75.77, -395.2) * mm, "mid": v(77.18, -394.62) * mm, "end": v(77.77, -393.2) * mm});
            skArc(sketch, "E17.4.2.11", {"start": v(69.77, -345.2) * mm, "mid": v(68.35, -345.8) * mm, "end": v(67.77, -347.2) * mm});
            skLineSegment(sketch, "E17.4.3.0", {"start": v(77.77, -333.2) * mm, "end": v(77.77, -287.2) * mm});
            skPoint(sketch, "E17.4.3.1", {"position": v(67.77, -335.2) * mm});
            skLineSegment(sketch, "E17.4.3.2", {"start": v(67.77, -333.2) * mm, "end": v(67.77, -287.2) * mm});
            skArc(sketch, "E17.4.3.3", {"start": v(67.77, -333.2) * mm, "mid": v(68.35, -334.62) * mm, "end": v(69.77, -335.2) * mm});
            skPoint(sketch, "E17.4.3.4", {"position": v(77.77, -335.2) * mm});
            skPoint(sketch, "E17.4.3.5", {"position": v(67.77, -285.2) * mm});
            skLineSegment(sketch, "E17.4.3.6", {"start": v(69.77, -285.2) * mm, "end": v(75.77, -285.2) * mm});
            skLineSegment(sketch, "E17.4.3.7", {"start": v(69.77, -335.2) * mm, "end": v(75.77, -335.2) * mm});
            skPoint(sketch, "E17.4.3.8", {"position": v(77.77, -285.2) * mm});
            skArc(sketch, "E17.4.3.9", {"start": v(77.77, -287.2) * mm, "mid": v(77.18, -285.8) * mm, "end": v(75.77, -285.2) * mm});
            skArc(sketch, "E17.4.3.10", {"start": v(75.77, -335.2) * mm, "mid": v(77.18, -334.62) * mm, "end": v(77.77, -333.2) * mm});
            skArc(sketch, "E17.4.3.11", {"start": v(69.77, -285.2) * mm, "mid": v(68.35, -285.8) * mm, "end": v(67.77, -287.2) * mm});
            skLineSegment(sketch, "E17.4.4.0", {"start": v(77.77, -273.2) * mm, "end": v(77.77, -227.2) * mm});
            skPoint(sketch, "E17.4.4.1", {"position": v(67.77, -275.2) * mm});
            skLineSegment(sketch, "E17.4.4.2", {"start": v(67.77, -273.2) * mm, "end": v(67.77, -227.2) * mm});
            skArc(sketch, "E17.4.4.3", {"start": v(67.77, -273.2) * mm, "mid": v(68.35, -274.62) * mm, "end": v(69.77, -275.2) * mm});
            skPoint(sketch, "E17.4.4.4", {"position": v(77.77, -275.2) * mm});
            skPoint(sketch, "E17.4.4.5", {"position": v(67.77, -225.2) * mm});
            skLineSegment(sketch, "E17.4.4.6", {"start": v(69.77, -225.2) * mm, "end": v(75.77, -225.2) * mm});
            skLineSegment(sketch, "E17.4.4.7", {"start": v(69.77, -275.2) * mm, "end": v(75.77, -275.2) * mm});
            skPoint(sketch, "E17.4.4.8", {"position": v(77.77, -225.2) * mm});
            skArc(sketch, "E17.4.4.9", {"start": v(77.77, -227.2) * mm, "mid": v(77.18, -225.8) * mm, "end": v(75.77, -225.2) * mm});
            skArc(sketch, "E17.4.4.10", {"start": v(75.77, -275.2) * mm, "mid": v(77.18, -274.62) * mm, "end": v(77.77, -273.2) * mm});
            skArc(sketch, "E17.4.4.11", {"start": v(69.77, -225.2) * mm, "mid": v(68.35, -225.8) * mm, "end": v(67.77, -227.2) * mm});
            skLineSegment(sketch, "E17.5.0.0", {"start": v(93.27, -513.2) * mm, "end": v(93.27, -467.2) * mm});
            skPoint(sketch, "E17.5.0.1", {"position": v(83.27, -515.2) * mm});
            skLineSegment(sketch, "E17.5.0.2", {"start": v(83.27, -513.2) * mm, "end": v(83.27, -467.2) * mm});
            skArc(sketch, "E17.5.0.3", {"start": v(83.27, -513.2) * mm, "mid": v(83.85, -514.62) * mm, "end": v(85.27, -515.2) * mm});
            skPoint(sketch, "E17.5.0.4", {"position": v(93.27, -515.2) * mm});
            skPoint(sketch, "E17.5.0.5", {"position": v(83.27, -465.2) * mm});
            skLineSegment(sketch, "E17.5.0.6", {"start": v(85.27, -465.2) * mm, "end": v(91.27, -465.2) * mm});
            skLineSegment(sketch, "E17.5.0.7", {"start": v(85.27, -515.2) * mm, "end": v(91.27, -515.2) * mm});
            skPoint(sketch, "E17.5.0.8", {"position": v(93.27, -465.2) * mm});
            skArc(sketch, "E17.5.0.9", {"start": v(93.27, -467.2) * mm, "mid": v(92.68, -465.8) * mm, "end": v(91.27, -465.2) * mm});
            skArc(sketch, "E17.5.0.10", {"start": v(91.27, -515.2) * mm, "mid": v(92.68, -514.62) * mm, "end": v(93.27, -513.2) * mm});
            skArc(sketch, "E17.5.0.11", {"start": v(85.27, -465.2) * mm, "mid": v(83.85, -465.8) * mm, "end": v(83.27, -467.2) * mm});
            skLineSegment(sketch, "E17.5.1.0", {"start": v(93.27, -453.2) * mm, "end": v(93.27, -407.2) * mm});
            skPoint(sketch, "E17.5.1.1", {"position": v(83.27, -455.2) * mm});
            skLineSegment(sketch, "E17.5.1.2", {"start": v(83.27, -453.2) * mm, "end": v(83.27, -407.2) * mm});
            skArc(sketch, "E17.5.1.3", {"start": v(83.27, -453.2) * mm, "mid": v(83.85, -454.62) * mm, "end": v(85.27, -455.2) * mm});
            skPoint(sketch, "E17.5.1.4", {"position": v(93.27, -455.2) * mm});
            skPoint(sketch, "E17.5.1.5", {"position": v(83.27, -405.2) * mm});
            skLineSegment(sketch, "E17.5.1.6", {"start": v(85.27, -405.2) * mm, "end": v(91.27, -405.2) * mm});
            skLineSegment(sketch, "E17.5.1.7", {"start": v(85.27, -455.2) * mm, "end": v(91.27, -455.2) * mm});
            skPoint(sketch, "E17.5.1.8", {"position": v(93.27, -405.2) * mm});
            skArc(sketch, "E17.5.1.9", {"start": v(93.27, -407.2) * mm, "mid": v(92.68, -405.8) * mm, "end": v(91.27, -405.2) * mm});
            skArc(sketch, "E17.5.1.10", {"start": v(91.27, -455.2) * mm, "mid": v(92.68, -454.62) * mm, "end": v(93.27, -453.2) * mm});
            skArc(sketch, "E17.5.1.11", {"start": v(85.27, -405.2) * mm, "mid": v(83.85, -405.8) * mm, "end": v(83.27, -407.2) * mm});
            skLineSegment(sketch, "E17.5.2.0", {"start": v(93.27, -393.2) * mm, "end": v(93.27, -347.2) * mm});
            skPoint(sketch, "E17.5.2.1", {"position": v(83.27, -395.2) * mm});
            skLineSegment(sketch, "E17.5.2.2", {"start": v(83.27, -393.2) * mm, "end": v(83.27, -347.2) * mm});
            skArc(sketch, "E17.5.2.3", {"start": v(83.27, -393.2) * mm, "mid": v(83.85, -394.62) * mm, "end": v(85.27, -395.2) * mm});
            skPoint(sketch, "E17.5.2.4", {"position": v(93.27, -395.2) * mm});
            skPoint(sketch, "E17.5.2.5", {"position": v(83.27, -345.2) * mm});
            skLineSegment(sketch, "E17.5.2.6", {"start": v(85.27, -345.2) * mm, "end": v(91.27, -345.2) * mm});
            skLineSegment(sketch, "E17.5.2.7", {"start": v(85.27, -395.2) * mm, "end": v(91.27, -395.2) * mm});
            skPoint(sketch, "E17.5.2.8", {"position": v(93.27, -345.2) * mm});
            skArc(sketch, "E17.5.2.9", {"start": v(93.27, -347.2) * mm, "mid": v(92.68, -345.8) * mm, "end": v(91.27, -345.2) * mm});
            skArc(sketch, "E17.5.2.10", {"start": v(91.27, -395.2) * mm, "mid": v(92.68, -394.62) * mm, "end": v(93.27, -393.2) * mm});
            skArc(sketch, "E17.5.2.11", {"start": v(85.27, -345.2) * mm, "mid": v(83.85, -345.8) * mm, "end": v(83.27, -347.2) * mm});
            skLineSegment(sketch, "E17.5.3.0", {"start": v(93.27, -333.2) * mm, "end": v(93.27, -287.2) * mm});
            skPoint(sketch, "E17.5.3.1", {"position": v(83.27, -335.2) * mm});
            skLineSegment(sketch, "E17.5.3.2", {"start": v(83.27, -333.2) * mm, "end": v(83.27, -287.2) * mm});
            skArc(sketch, "E17.5.3.3", {"start": v(83.27, -333.2) * mm, "mid": v(83.85, -334.62) * mm, "end": v(85.27, -335.2) * mm});
            skPoint(sketch, "E17.5.3.4", {"position": v(93.27, -335.2) * mm});
            skPoint(sketch, "E17.5.3.5", {"position": v(83.27, -285.2) * mm});
            skLineSegment(sketch, "E17.5.3.6", {"start": v(85.27, -285.2) * mm, "end": v(91.27, -285.2) * mm});
            skLineSegment(sketch, "E17.5.3.7", {"start": v(85.27, -335.2) * mm, "end": v(91.27, -335.2) * mm});
            skPoint(sketch, "E17.5.3.8", {"position": v(93.27, -285.2) * mm});
            skArc(sketch, "E17.5.3.9", {"start": v(93.27, -287.2) * mm, "mid": v(92.68, -285.8) * mm, "end": v(91.27, -285.2) * mm});
            skArc(sketch, "E17.5.3.10", {"start": v(91.27, -335.2) * mm, "mid": v(92.68, -334.62) * mm, "end": v(93.27, -333.2) * mm});
            skArc(sketch, "E17.5.3.11", {"start": v(85.27, -285.2) * mm, "mid": v(83.85, -285.8) * mm, "end": v(83.27, -287.2) * mm});
            skLineSegment(sketch, "E17.5.4.0", {"start": v(93.27, -273.2) * mm, "end": v(93.27, -227.2) * mm});
            skPoint(sketch, "E17.5.4.1", {"position": v(83.27, -275.2) * mm});
            skLineSegment(sketch, "E17.5.4.2", {"start": v(83.27, -273.2) * mm, "end": v(83.27, -227.2) * mm});
            skArc(sketch, "E17.5.4.3", {"start": v(83.27, -273.2) * mm, "mid": v(83.85, -274.62) * mm, "end": v(85.27, -275.2) * mm});
            skPoint(sketch, "E17.5.4.4", {"position": v(93.27, -275.2) * mm});
            skPoint(sketch, "E17.5.4.5", {"position": v(83.27, -225.2) * mm});
            skLineSegment(sketch, "E17.5.4.6", {"start": v(85.27, -225.2) * mm, "end": v(91.27, -225.2) * mm});
            skLineSegment(sketch, "E17.5.4.7", {"start": v(85.27, -275.2) * mm, "end": v(91.27, -275.2) * mm});
            skPoint(sketch, "E17.5.4.8", {"position": v(93.27, -225.2) * mm});
            skArc(sketch, "E17.5.4.9", {"start": v(93.27, -227.2) * mm, "mid": v(92.68, -225.8) * mm, "end": v(91.27, -225.2) * mm});
            skArc(sketch, "E17.5.4.10", {"start": v(91.27, -275.2) * mm, "mid": v(92.68, -274.62) * mm, "end": v(93.27, -273.2) * mm});
            skArc(sketch, "E17.5.4.11", {"start": v(85.27, -225.2) * mm, "mid": v(83.85, -225.8) * mm, "end": v(83.27, -227.2) * mm});
            skLineSegment(sketch, "E17.6.0.0", {"start": v(108.77, -513.2) * mm, "end": v(108.77, -467.2) * mm});
            skPoint(sketch, "E17.6.0.1", {"position": v(98.77, -515.2) * mm});
            skLineSegment(sketch, "E17.6.0.2", {"start": v(98.77, -513.2) * mm, "end": v(98.77, -467.2) * mm});
            skArc(sketch, "E17.6.0.3", {"start": v(98.77, -513.2) * mm, "mid": v(99.35, -514.62) * mm, "end": v(100.77, -515.2) * mm});
            skPoint(sketch, "E17.6.0.4", {"position": v(108.77, -515.2) * mm});
            skPoint(sketch, "E17.6.0.5", {"position": v(98.77, -465.2) * mm});
            skLineSegment(sketch, "E17.6.0.6", {"start": v(100.77, -465.2) * mm, "end": v(106.77, -465.2) * mm});
            skLineSegment(sketch, "E17.6.0.7", {"start": v(100.77, -515.2) * mm, "end": v(106.77, -515.2) * mm});
            skPoint(sketch, "E17.6.0.8", {"position": v(108.77, -465.2) * mm});
            skArc(sketch, "E17.6.0.9", {"start": v(108.77, -467.2) * mm, "mid": v(108.18, -465.8) * mm, "end": v(106.77, -465.2) * mm});
            skArc(sketch, "E17.6.0.10", {"start": v(106.77, -515.2) * mm, "mid": v(108.18, -514.62) * mm, "end": v(108.77, -513.2) * mm});
            skArc(sketch, "E17.6.0.11", {"start": v(100.77, -465.2) * mm, "mid": v(99.35, -465.8) * mm, "end": v(98.77, -467.2) * mm});
            skLineSegment(sketch, "E17.6.1.0", {"start": v(108.77, -453.2) * mm, "end": v(108.77, -407.2) * mm});
            skPoint(sketch, "E17.6.1.1", {"position": v(98.77, -455.2) * mm});
            skLineSegment(sketch, "E17.6.1.2", {"start": v(98.77, -453.2) * mm, "end": v(98.77, -407.2) * mm});
            skArc(sketch, "E17.6.1.3", {"start": v(98.77, -453.2) * mm, "mid": v(99.35, -454.62) * mm, "end": v(100.77, -455.2) * mm});
            skPoint(sketch, "E17.6.1.4", {"position": v(108.77, -455.2) * mm});
            skPoint(sketch, "E17.6.1.5", {"position": v(98.77, -405.2) * mm});
            skLineSegment(sketch, "E17.6.1.6", {"start": v(100.77, -405.2) * mm, "end": v(106.77, -405.2) * mm});
            skLineSegment(sketch, "E17.6.1.7", {"start": v(100.77, -455.2) * mm, "end": v(106.77, -455.2) * mm});
            skPoint(sketch, "E17.6.1.8", {"position": v(108.77, -405.2) * mm});
            skArc(sketch, "E17.6.1.9", {"start": v(108.77, -407.2) * mm, "mid": v(108.18, -405.8) * mm, "end": v(106.77, -405.2) * mm});
            skArc(sketch, "E17.6.1.10", {"start": v(106.77, -455.2) * mm, "mid": v(108.18, -454.62) * mm, "end": v(108.77, -453.2) * mm});
            skArc(sketch, "E17.6.1.11", {"start": v(100.77, -405.2) * mm, "mid": v(99.35, -405.8) * mm, "end": v(98.77, -407.2) * mm});
            skLineSegment(sketch, "E17.6.2.0", {"start": v(108.77, -393.2) * mm, "end": v(108.77, -347.2) * mm});
            skPoint(sketch, "E17.6.2.1", {"position": v(98.77, -395.2) * mm});
            skLineSegment(sketch, "E17.6.2.2", {"start": v(98.77, -393.2) * mm, "end": v(98.77, -347.2) * mm});
            skArc(sketch, "E17.6.2.3", {"start": v(98.77, -393.2) * mm, "mid": v(99.35, -394.62) * mm, "end": v(100.77, -395.2) * mm});
            skPoint(sketch, "E17.6.2.4", {"position": v(108.77, -395.2) * mm});
            skPoint(sketch, "E17.6.2.5", {"position": v(98.77, -345.2) * mm});
            skLineSegment(sketch, "E17.6.2.6", {"start": v(100.77, -345.2) * mm, "end": v(106.77, -345.2) * mm});
            skLineSegment(sketch, "E17.6.2.7", {"start": v(100.77, -395.2) * mm, "end": v(106.77, -395.2) * mm});
            skPoint(sketch, "E17.6.2.8", {"position": v(108.77, -345.2) * mm});
            skArc(sketch, "E17.6.2.9", {"start": v(108.77, -347.2) * mm, "mid": v(108.18, -345.8) * mm, "end": v(106.77, -345.2) * mm});
            skArc(sketch, "E17.6.2.10", {"start": v(106.77, -395.2) * mm, "mid": v(108.18, -394.62) * mm, "end": v(108.77, -393.2) * mm});
            skArc(sketch, "E17.6.2.11", {"start": v(100.77, -345.2) * mm, "mid": v(99.35, -345.8) * mm, "end": v(98.77, -347.2) * mm});
            skLineSegment(sketch, "E17.6.3.0", {"start": v(108.77, -333.2) * mm, "end": v(108.77, -287.2) * mm});
            skPoint(sketch, "E17.6.3.1", {"position": v(98.77, -335.2) * mm});
            skLineSegment(sketch, "E17.6.3.2", {"start": v(98.77, -333.2) * mm, "end": v(98.77, -287.2) * mm});
            skArc(sketch, "E17.6.3.3", {"start": v(98.77, -333.2) * mm, "mid": v(99.35, -334.62) * mm, "end": v(100.77, -335.2) * mm});
            skPoint(sketch, "E17.6.3.4", {"position": v(108.77, -335.2) * mm});
            skPoint(sketch, "E17.6.3.5", {"position": v(98.77, -285.2) * mm});
            skLineSegment(sketch, "E17.6.3.6", {"start": v(100.77, -285.2) * mm, "end": v(106.77, -285.2) * mm});
            skLineSegment(sketch, "E17.6.3.7", {"start": v(100.77, -335.2) * mm, "end": v(106.77, -335.2) * mm});
            skPoint(sketch, "E17.6.3.8", {"position": v(108.77, -285.2) * mm});
            skArc(sketch, "E17.6.3.9", {"start": v(108.77, -287.2) * mm, "mid": v(108.18, -285.8) * mm, "end": v(106.77, -285.2) * mm});
            skArc(sketch, "E17.6.3.10", {"start": v(106.77, -335.2) * mm, "mid": v(108.18, -334.62) * mm, "end": v(108.77, -333.2) * mm});
            skArc(sketch, "E17.6.3.11", {"start": v(100.77, -285.2) * mm, "mid": v(99.35, -285.8) * mm, "end": v(98.77, -287.2) * mm});
            skLineSegment(sketch, "E17.6.4.0", {"start": v(108.77, -273.2) * mm, "end": v(108.77, -227.2) * mm});
            skPoint(sketch, "E17.6.4.1", {"position": v(98.77, -275.2) * mm});
            skLineSegment(sketch, "E17.6.4.2", {"start": v(98.77, -273.2) * mm, "end": v(98.77, -227.2) * mm});
            skArc(sketch, "E17.6.4.3", {"start": v(98.77, -273.2) * mm, "mid": v(99.35, -274.62) * mm, "end": v(100.77, -275.2) * mm});
            skPoint(sketch, "E17.6.4.4", {"position": v(108.77, -275.2) * mm});
            skPoint(sketch, "E17.6.4.5", {"position": v(98.77, -225.2) * mm});
            skLineSegment(sketch, "E17.6.4.6", {"start": v(100.77, -225.2) * mm, "end": v(106.77, -225.2) * mm});
            skLineSegment(sketch, "E17.6.4.7", {"start": v(100.77, -275.2) * mm, "end": v(106.77, -275.2) * mm});
            skPoint(sketch, "E17.6.4.8", {"position": v(108.77, -225.2) * mm});
            skArc(sketch, "E17.6.4.9", {"start": v(108.77, -227.2) * mm, "mid": v(108.18, -225.8) * mm, "end": v(106.77, -225.2) * mm});
            skArc(sketch, "E17.6.4.10", {"start": v(106.77, -275.2) * mm, "mid": v(108.18, -274.62) * mm, "end": v(108.77, -273.2) * mm});
            skArc(sketch, "E17.6.4.11", {"start": v(100.77, -225.2) * mm, "mid": v(99.35, -225.8) * mm, "end": v(98.77, -227.2) * mm});
            skLineSegment(sketch, "E17.7.0.0", {"start": v(124.27, -513.2) * mm, "end": v(124.27, -467.2) * mm});
            skPoint(sketch, "E17.7.0.1", {"position": v(114.27, -515.2) * mm});
            skLineSegment(sketch, "E17.7.0.2", {"start": v(114.27, -513.2) * mm, "end": v(114.27, -467.2) * mm});
            skArc(sketch, "E17.7.0.3", {"start": v(114.27, -513.2) * mm, "mid": v(114.85, -514.62) * mm, "end": v(116.27, -515.2) * mm});
            skPoint(sketch, "E17.7.0.4", {"position": v(124.27, -515.2) * mm});
            skPoint(sketch, "E17.7.0.5", {"position": v(114.27, -465.2) * mm});
            skLineSegment(sketch, "E17.7.0.6", {"start": v(116.27, -465.2) * mm, "end": v(122.27, -465.2) * mm});
            skLineSegment(sketch, "E17.7.0.7", {"start": v(116.27, -515.2) * mm, "end": v(122.27, -515.2) * mm});
            skPoint(sketch, "E17.7.0.8", {"position": v(124.27, -465.2) * mm});
            skArc(sketch, "E17.7.0.9", {"start": v(124.27, -467.2) * mm, "mid": v(123.68, -465.8) * mm, "end": v(122.27, -465.2) * mm});
            skArc(sketch, "E17.7.0.10", {"start": v(122.27, -515.2) * mm, "mid": v(123.68, -514.62) * mm, "end": v(124.27, -513.2) * mm});
            skArc(sketch, "E17.7.0.11", {"start": v(116.27, -465.2) * mm, "mid": v(114.85, -465.8) * mm, "end": v(114.27, -467.2) * mm});
            skLineSegment(sketch, "E17.7.1.0", {"start": v(124.27, -453.2) * mm, "end": v(124.27, -407.2) * mm});
            skPoint(sketch, "E17.7.1.1", {"position": v(114.27, -455.2) * mm});
            skLineSegment(sketch, "E17.7.1.2", {"start": v(114.27, -453.2) * mm, "end": v(114.27, -407.2) * mm});
            skArc(sketch, "E17.7.1.3", {"start": v(114.27, -453.2) * mm, "mid": v(114.85, -454.62) * mm, "end": v(116.27, -455.2) * mm});
            skPoint(sketch, "E17.7.1.4", {"position": v(124.27, -455.2) * mm});
            skPoint(sketch, "E17.7.1.5", {"position": v(114.27, -405.2) * mm});
            skLineSegment(sketch, "E17.7.1.6", {"start": v(116.27, -405.2) * mm, "end": v(122.27, -405.2) * mm});
            skLineSegment(sketch, "E17.7.1.7", {"start": v(116.27, -455.2) * mm, "end": v(122.27, -455.2) * mm});
            skPoint(sketch, "E17.7.1.8", {"position": v(124.27, -405.2) * mm});
            skArc(sketch, "E17.7.1.9", {"start": v(124.27, -407.2) * mm, "mid": v(123.68, -405.8) * mm, "end": v(122.27, -405.2) * mm});
            skArc(sketch, "E17.7.1.10", {"start": v(122.27, -455.2) * mm, "mid": v(123.68, -454.62) * mm, "end": v(124.27, -453.2) * mm});
            skArc(sketch, "E17.7.1.11", {"start": v(116.27, -405.2) * mm, "mid": v(114.85, -405.8) * mm, "end": v(114.27, -407.2) * mm});
            skLineSegment(sketch, "E17.7.2.0", {"start": v(124.27, -393.2) * mm, "end": v(124.27, -347.2) * mm});
            skPoint(sketch, "E17.7.2.1", {"position": v(114.27, -395.2) * mm});
            skLineSegment(sketch, "E17.7.2.2", {"start": v(114.27, -393.2) * mm, "end": v(114.27, -347.2) * mm});
            skArc(sketch, "E17.7.2.3", {"start": v(114.27, -393.2) * mm, "mid": v(114.85, -394.62) * mm, "end": v(116.27, -395.2) * mm});
            skPoint(sketch, "E17.7.2.4", {"position": v(124.27, -395.2) * mm});
            skPoint(sketch, "E17.7.2.5", {"position": v(114.27, -345.2) * mm});
            skLineSegment(sketch, "E17.7.2.6", {"start": v(116.27, -345.2) * mm, "end": v(122.27, -345.2) * mm});
            skLineSegment(sketch, "E17.7.2.7", {"start": v(116.27, -395.2) * mm, "end": v(122.27, -395.2) * mm});
            skPoint(sketch, "E17.7.2.8", {"position": v(124.27, -345.2) * mm});
            skArc(sketch, "E17.7.2.9", {"start": v(124.27, -347.2) * mm, "mid": v(123.68, -345.8) * mm, "end": v(122.27, -345.2) * mm});
            skArc(sketch, "E17.7.2.10", {"start": v(122.27, -395.2) * mm, "mid": v(123.68, -394.62) * mm, "end": v(124.27, -393.2) * mm});
            skArc(sketch, "E17.7.2.11", {"start": v(116.27, -345.2) * mm, "mid": v(114.85, -345.8) * mm, "end": v(114.27, -347.2) * mm});
            skLineSegment(sketch, "E17.7.3.0", {"start": v(124.27, -333.2) * mm, "end": v(124.27, -287.2) * mm});
            skPoint(sketch, "E17.7.3.1", {"position": v(114.27, -335.2) * mm});
            skLineSegment(sketch, "E17.7.3.2", {"start": v(114.27, -333.2) * mm, "end": v(114.27, -287.2) * mm});
            skArc(sketch, "E17.7.3.3", {"start": v(114.27, -333.2) * mm, "mid": v(114.85, -334.62) * mm, "end": v(116.27, -335.2) * mm});
            skPoint(sketch, "E17.7.3.4", {"position": v(124.27, -335.2) * mm});
            skPoint(sketch, "E17.7.3.5", {"position": v(114.27, -285.2) * mm});
            skLineSegment(sketch, "E17.7.3.6", {"start": v(116.27, -285.2) * mm, "end": v(122.27, -285.2) * mm});
            skLineSegment(sketch, "E17.7.3.7", {"start": v(116.27, -335.2) * mm, "end": v(122.27, -335.2) * mm});
            skPoint(sketch, "E17.7.3.8", {"position": v(124.27, -285.2) * mm});
            skArc(sketch, "E17.7.3.9", {"start": v(124.27, -287.2) * mm, "mid": v(123.68, -285.8) * mm, "end": v(122.27, -285.2) * mm});
            skArc(sketch, "E17.7.3.10", {"start": v(122.27, -335.2) * mm, "mid": v(123.68, -334.62) * mm, "end": v(124.27, -333.2) * mm});
            skArc(sketch, "E17.7.3.11", {"start": v(116.27, -285.2) * mm, "mid": v(114.85, -285.8) * mm, "end": v(114.27, -287.2) * mm});
            skLineSegment(sketch, "E17.7.4.0", {"start": v(124.27, -273.2) * mm, "end": v(124.27, -227.2) * mm});
            skPoint(sketch, "E17.7.4.1", {"position": v(114.27, -275.2) * mm});
            skLineSegment(sketch, "E17.7.4.2", {"start": v(114.27, -273.2) * mm, "end": v(114.27, -227.2) * mm});
            skArc(sketch, "E17.7.4.3", {"start": v(114.27, -273.2) * mm, "mid": v(114.85, -274.62) * mm, "end": v(116.27, -275.2) * mm});
            skPoint(sketch, "E17.7.4.4", {"position": v(124.27, -275.2) * mm});
            skPoint(sketch, "E17.7.4.5", {"position": v(114.27, -225.2) * mm});
            skLineSegment(sketch, "E17.7.4.6", {"start": v(116.27, -225.2) * mm, "end": v(122.27, -225.2) * mm});
            skLineSegment(sketch, "E17.7.4.7", {"start": v(116.27, -275.2) * mm, "end": v(122.27, -275.2) * mm});
            skPoint(sketch, "E17.7.4.8", {"position": v(124.27, -225.2) * mm});
            skArc(sketch, "E17.7.4.9", {"start": v(124.27, -227.2) * mm, "mid": v(123.68, -225.8) * mm, "end": v(122.27, -225.2) * mm});
            skArc(sketch, "E17.7.4.10", {"start": v(122.27, -275.2) * mm, "mid": v(123.68, -274.62) * mm, "end": v(124.27, -273.2) * mm});
            skArc(sketch, "E17.7.4.11", {"start": v(116.27, -225.2) * mm, "mid": v(114.85, -225.8) * mm, "end": v(114.27, -227.2) * mm});
            skLineSegment(sketch, "E17.8.0.0", {"start": v(139.77, -513.2) * mm, "end": v(139.77, -467.2) * mm});
            skPoint(sketch, "E17.8.0.1", {"position": v(129.77, -515.2) * mm});
            skLineSegment(sketch, "E17.8.0.2", {"start": v(129.77, -513.2) * mm, "end": v(129.77, -467.2) * mm});
            skArc(sketch, "E17.8.0.3", {"start": v(129.77, -513.2) * mm, "mid": v(130.35, -514.62) * mm, "end": v(131.77, -515.2) * mm});
            skPoint(sketch, "E17.8.0.4", {"position": v(139.77, -515.2) * mm});
            skPoint(sketch, "E17.8.0.5", {"position": v(129.77, -465.2) * mm});
            skLineSegment(sketch, "E17.8.0.6", {"start": v(131.77, -465.2) * mm, "end": v(137.77, -465.2) * mm});
            skLineSegment(sketch, "E17.8.0.7", {"start": v(131.77, -515.2) * mm, "end": v(137.77, -515.2) * mm});
            skPoint(sketch, "E17.8.0.8", {"position": v(139.77, -465.2) * mm});
            skArc(sketch, "E17.8.0.9", {"start": v(139.77, -467.2) * mm, "mid": v(139.18, -465.8) * mm, "end": v(137.77, -465.2) * mm});
            skArc(sketch, "E17.8.0.10", {"start": v(137.77, -515.2) * mm, "mid": v(139.18, -514.62) * mm, "end": v(139.77, -513.2) * mm});
            skArc(sketch, "E17.8.0.11", {"start": v(131.77, -465.2) * mm, "mid": v(130.35, -465.8) * mm, "end": v(129.77, -467.2) * mm});
            skLineSegment(sketch, "E17.8.1.0", {"start": v(139.77, -453.2) * mm, "end": v(139.77, -407.2) * mm});
            skPoint(sketch, "E17.8.1.1", {"position": v(129.77, -455.2) * mm});
            skLineSegment(sketch, "E17.8.1.2", {"start": v(129.77, -453.2) * mm, "end": v(129.77, -407.2) * mm});
            skArc(sketch, "E17.8.1.3", {"start": v(129.77, -453.2) * mm, "mid": v(130.35, -454.62) * mm, "end": v(131.77, -455.2) * mm});
            skPoint(sketch, "E17.8.1.4", {"position": v(139.77, -455.2) * mm});
            skPoint(sketch, "E17.8.1.5", {"position": v(129.77, -405.2) * mm});
            skLineSegment(sketch, "E17.8.1.6", {"start": v(131.77, -405.2) * mm, "end": v(137.77, -405.2) * mm});
            skLineSegment(sketch, "E17.8.1.7", {"start": v(131.77, -455.2) * mm, "end": v(137.77, -455.2) * mm});
            skPoint(sketch, "E17.8.1.8", {"position": v(139.77, -405.2) * mm});
            skArc(sketch, "E17.8.1.9", {"start": v(139.77, -407.2) * mm, "mid": v(139.18, -405.8) * mm, "end": v(137.77, -405.2) * mm});
            skArc(sketch, "E17.8.1.10", {"start": v(137.77, -455.2) * mm, "mid": v(139.18, -454.62) * mm, "end": v(139.77, -453.2) * mm});
            skArc(sketch, "E17.8.1.11", {"start": v(131.77, -405.2) * mm, "mid": v(130.35, -405.8) * mm, "end": v(129.77, -407.2) * mm});
            skLineSegment(sketch, "E17.8.2.0", {"start": v(139.77, -393.2) * mm, "end": v(139.77, -347.2) * mm});
            skPoint(sketch, "E17.8.2.1", {"position": v(129.77, -395.2) * mm});
            skLineSegment(sketch, "E17.8.2.2", {"start": v(129.77, -393.2) * mm, "end": v(129.77, -347.2) * mm});
            skArc(sketch, "E17.8.2.3", {"start": v(129.77, -393.2) * mm, "mid": v(130.35, -394.62) * mm, "end": v(131.77, -395.2) * mm});
            skPoint(sketch, "E17.8.2.4", {"position": v(139.77, -395.2) * mm});
            skPoint(sketch, "E17.8.2.5", {"position": v(129.77, -345.2) * mm});
            skLineSegment(sketch, "E17.8.2.6", {"start": v(131.77, -345.2) * mm, "end": v(137.77, -345.2) * mm});
            skLineSegment(sketch, "E17.8.2.7", {"start": v(131.77, -395.2) * mm, "end": v(137.77, -395.2) * mm});
            skPoint(sketch, "E17.8.2.8", {"position": v(139.77, -345.2) * mm});
            skArc(sketch, "E17.8.2.9", {"start": v(139.77, -347.2) * mm, "mid": v(139.18, -345.8) * mm, "end": v(137.77, -345.2) * mm});
            skArc(sketch, "E17.8.2.10", {"start": v(137.77, -395.2) * mm, "mid": v(139.18, -394.62) * mm, "end": v(139.77, -393.2) * mm});
            skArc(sketch, "E17.8.2.11", {"start": v(131.77, -345.2) * mm, "mid": v(130.35, -345.8) * mm, "end": v(129.77, -347.2) * mm});
            skLineSegment(sketch, "E17.8.3.0", {"start": v(139.77, -333.2) * mm, "end": v(139.77, -287.2) * mm});
            skPoint(sketch, "E17.8.3.1", {"position": v(129.77, -335.2) * mm});
            skLineSegment(sketch, "E17.8.3.2", {"start": v(129.77, -333.2) * mm, "end": v(129.77, -287.2) * mm});
            skArc(sketch, "E17.8.3.3", {"start": v(129.77, -333.2) * mm, "mid": v(130.35, -334.62) * mm, "end": v(131.77, -335.2) * mm});
            skPoint(sketch, "E17.8.3.4", {"position": v(139.77, -335.2) * mm});
            skPoint(sketch, "E17.8.3.5", {"position": v(129.77, -285.2) * mm});
            skLineSegment(sketch, "E17.8.3.6", {"start": v(131.77, -285.2) * mm, "end": v(137.77, -285.2) * mm});
            skLineSegment(sketch, "E17.8.3.7", {"start": v(131.77, -335.2) * mm, "end": v(137.77, -335.2) * mm});
            skPoint(sketch, "E17.8.3.8", {"position": v(139.77, -285.2) * mm});
            skArc(sketch, "E17.8.3.9", {"start": v(139.77, -287.2) * mm, "mid": v(139.18, -285.8) * mm, "end": v(137.77, -285.2) * mm});
            skArc(sketch, "E17.8.3.10", {"start": v(137.77, -335.2) * mm, "mid": v(139.18, -334.62) * mm, "end": v(139.77, -333.2) * mm});
            skArc(sketch, "E17.8.3.11", {"start": v(131.77, -285.2) * mm, "mid": v(130.35, -285.8) * mm, "end": v(129.77, -287.2) * mm});
            skLineSegment(sketch, "E17.8.4.0", {"start": v(139.77, -273.2) * mm, "end": v(139.77, -227.2) * mm});
            skPoint(sketch, "E17.8.4.1", {"position": v(129.77, -275.2) * mm});
            skLineSegment(sketch, "E17.8.4.2", {"start": v(129.77, -273.2) * mm, "end": v(129.77, -227.2) * mm});
            skArc(sketch, "E17.8.4.3", {"start": v(129.77, -273.2) * mm, "mid": v(130.35, -274.62) * mm, "end": v(131.77, -275.2) * mm});
            skPoint(sketch, "E17.8.4.4", {"position": v(139.77, -275.2) * mm});
            skPoint(sketch, "E17.8.4.5", {"position": v(129.77, -225.2) * mm});
            skLineSegment(sketch, "E17.8.4.6", {"start": v(131.77, -225.2) * mm, "end": v(137.77, -225.2) * mm});
            skLineSegment(sketch, "E17.8.4.7", {"start": v(131.77, -275.2) * mm, "end": v(137.77, -275.2) * mm});
            skPoint(sketch, "E17.8.4.8", {"position": v(139.77, -225.2) * mm});
            skArc(sketch, "E17.8.4.9", {"start": v(139.77, -227.2) * mm, "mid": v(139.18, -225.8) * mm, "end": v(137.77, -225.2) * mm});
            skArc(sketch, "E17.8.4.10", {"start": v(137.77, -275.2) * mm, "mid": v(139.18, -274.62) * mm, "end": v(139.77, -273.2) * mm});
            skArc(sketch, "E17.8.4.11", {"start": v(131.77, -225.2) * mm, "mid": v(130.35, -225.8) * mm, "end": v(129.77, -227.2) * mm});
            skLineSegment(sketch, "E17.9.0.0", {"start": v(155.27, -513.2) * mm, "end": v(155.27, -467.2) * mm});
            skPoint(sketch, "E17.9.0.1", {"position": v(145.27, -515.2) * mm});
            skLineSegment(sketch, "E17.9.0.2", {"start": v(145.27, -513.2) * mm, "end": v(145.27, -467.2) * mm});
            skArc(sketch, "E17.9.0.3", {"start": v(145.27, -513.2) * mm, "mid": v(145.85, -514.62) * mm, "end": v(147.27, -515.2) * mm});
            skPoint(sketch, "E17.9.0.4", {"position": v(155.27, -515.2) * mm});
            skPoint(sketch, "E17.9.0.5", {"position": v(145.27, -465.2) * mm});
            skLineSegment(sketch, "E17.9.0.6", {"start": v(147.27, -465.2) * mm, "end": v(153.27, -465.2) * mm});
            skLineSegment(sketch, "E17.9.0.7", {"start": v(147.27, -515.2) * mm, "end": v(153.27, -515.2) * mm});
            skPoint(sketch, "E17.9.0.8", {"position": v(155.27, -465.2) * mm});
            skArc(sketch, "E17.9.0.9", {"start": v(155.27, -467.2) * mm, "mid": v(154.68, -465.8) * mm, "end": v(153.27, -465.2) * mm});
            skArc(sketch, "E17.9.0.10", {"start": v(153.27, -515.2) * mm, "mid": v(154.68, -514.62) * mm, "end": v(155.27, -513.2) * mm});
            skArc(sketch, "E17.9.0.11", {"start": v(147.27, -465.2) * mm, "mid": v(145.85, -465.8) * mm, "end": v(145.27, -467.2) * mm});
            skLineSegment(sketch, "E17.9.1.0", {"start": v(155.27, -453.2) * mm, "end": v(155.27, -407.2) * mm});
            skPoint(sketch, "E17.9.1.1", {"position": v(145.27, -455.2) * mm});
            skLineSegment(sketch, "E17.9.1.2", {"start": v(145.27, -453.2) * mm, "end": v(145.27, -407.2) * mm});
            skArc(sketch, "E17.9.1.3", {"start": v(145.27, -453.2) * mm, "mid": v(145.85, -454.62) * mm, "end": v(147.27, -455.2) * mm});
            skPoint(sketch, "E17.9.1.4", {"position": v(155.27, -455.2) * mm});
            skPoint(sketch, "E17.9.1.5", {"position": v(145.27, -405.2) * mm});
            skLineSegment(sketch, "E17.9.1.6", {"start": v(147.27, -405.2) * mm, "end": v(153.27, -405.2) * mm});
            skLineSegment(sketch, "E17.9.1.7", {"start": v(147.27, -455.2) * mm, "end": v(153.27, -455.2) * mm});
            skPoint(sketch, "E17.9.1.8", {"position": v(155.27, -405.2) * mm});
            skArc(sketch, "E17.9.1.9", {"start": v(155.27, -407.2) * mm, "mid": v(154.68, -405.8) * mm, "end": v(153.27, -405.2) * mm});
            skArc(sketch, "E17.9.1.10", {"start": v(153.27, -455.2) * mm, "mid": v(154.68, -454.62) * mm, "end": v(155.27, -453.2) * mm});
            skArc(sketch, "E17.9.1.11", {"start": v(147.27, -405.2) * mm, "mid": v(145.85, -405.8) * mm, "end": v(145.27, -407.2) * mm});
            skLineSegment(sketch, "E17.9.2.0", {"start": v(155.27, -393.2) * mm, "end": v(155.27, -347.2) * mm});
            skPoint(sketch, "E17.9.2.1", {"position": v(145.27, -395.2) * mm});
            skLineSegment(sketch, "E17.9.2.2", {"start": v(145.27, -393.2) * mm, "end": v(145.27, -347.2) * mm});
            skArc(sketch, "E17.9.2.3", {"start": v(145.27, -393.2) * mm, "mid": v(145.85, -394.62) * mm, "end": v(147.27, -395.2) * mm});
            skPoint(sketch, "E17.9.2.4", {"position": v(155.27, -395.2) * mm});
            skPoint(sketch, "E17.9.2.5", {"position": v(145.27, -345.2) * mm});
            skLineSegment(sketch, "E17.9.2.6", {"start": v(147.27, -345.2) * mm, "end": v(153.27, -345.2) * mm});
            skLineSegment(sketch, "E17.9.2.7", {"start": v(147.27, -395.2) * mm, "end": v(153.27, -395.2) * mm});
            skPoint(sketch, "E17.9.2.8", {"position": v(155.27, -345.2) * mm});
            skArc(sketch, "E17.9.2.9", {"start": v(155.27, -347.2) * mm, "mid": v(154.68, -345.8) * mm, "end": v(153.27, -345.2) * mm});
            skArc(sketch, "E17.9.2.10", {"start": v(153.27, -395.2) * mm, "mid": v(154.68, -394.62) * mm, "end": v(155.27, -393.2) * mm});
            skArc(sketch, "E17.9.2.11", {"start": v(147.27, -345.2) * mm, "mid": v(145.85, -345.8) * mm, "end": v(145.27, -347.2) * mm});
            skLineSegment(sketch, "E17.9.3.0", {"start": v(155.27, -333.2) * mm, "end": v(155.27, -287.2) * mm});
            skPoint(sketch, "E17.9.3.1", {"position": v(145.27, -335.2) * mm});
            skLineSegment(sketch, "E17.9.3.2", {"start": v(145.27, -333.2) * mm, "end": v(145.27, -287.2) * mm});
            skArc(sketch, "E17.9.3.3", {"start": v(145.27, -333.2) * mm, "mid": v(145.85, -334.62) * mm, "end": v(147.27, -335.2) * mm});
            skPoint(sketch, "E17.9.3.4", {"position": v(155.27, -335.2) * mm});
            skPoint(sketch, "E17.9.3.5", {"position": v(145.27, -285.2) * mm});
            skLineSegment(sketch, "E17.9.3.6", {"start": v(147.27, -285.2) * mm, "end": v(153.27, -285.2) * mm});
            skLineSegment(sketch, "E17.9.3.7", {"start": v(147.27, -335.2) * mm, "end": v(153.27, -335.2) * mm});
            skPoint(sketch, "E17.9.3.8", {"position": v(155.27, -285.2) * mm});
            skArc(sketch, "E17.9.3.9", {"start": v(155.27, -287.2) * mm, "mid": v(154.68, -285.8) * mm, "end": v(153.27, -285.2) * mm});
            skArc(sketch, "E17.9.3.10", {"start": v(153.27, -335.2) * mm, "mid": v(154.68, -334.62) * mm, "end": v(155.27, -333.2) * mm});
            skArc(sketch, "E17.9.3.11", {"start": v(147.27, -285.2) * mm, "mid": v(145.85, -285.8) * mm, "end": v(145.27, -287.2) * mm});
            skLineSegment(sketch, "E17.9.4.0", {"start": v(155.27, -273.2) * mm, "end": v(155.27, -227.2) * mm});
            skPoint(sketch, "E17.9.4.1", {"position": v(145.27, -275.2) * mm});
            skLineSegment(sketch, "E17.9.4.2", {"start": v(145.27, -273.2) * mm, "end": v(145.27, -227.2) * mm});
            skArc(sketch, "E17.9.4.3", {"start": v(145.27, -273.2) * mm, "mid": v(145.85, -274.62) * mm, "end": v(147.27, -275.2) * mm});
            skPoint(sketch, "E17.9.4.4", {"position": v(155.27, -275.2) * mm});
            skPoint(sketch, "E17.9.4.5", {"position": v(145.27, -225.2) * mm});
            skLineSegment(sketch, "E17.9.4.6", {"start": v(147.27, -225.2) * mm, "end": v(153.27, -225.2) * mm});
            skLineSegment(sketch, "E17.9.4.7", {"start": v(147.27, -275.2) * mm, "end": v(153.27, -275.2) * mm});
            skPoint(sketch, "E17.9.4.8", {"position": v(155.27, -225.2) * mm});
            skArc(sketch, "E17.9.4.9", {"start": v(155.27, -227.2) * mm, "mid": v(154.68, -225.8) * mm, "end": v(153.27, -225.2) * mm});
            skArc(sketch, "E17.9.4.10", {"start": v(153.27, -275.2) * mm, "mid": v(154.68, -274.62) * mm, "end": v(155.27, -273.2) * mm});
            skArc(sketch, "E17.9.4.11", {"start": v(147.27, -225.2) * mm, "mid": v(145.85, -225.8) * mm, "end": v(145.27, -227.2) * mm});
            skLineSegment(sketch, "E17.10.0.0", {"start": v(170.77, -513.2) * mm, "end": v(170.77, -467.2) * mm});
            skPoint(sketch, "E17.10.0.1", {"position": v(160.77, -515.2) * mm});
            skLineSegment(sketch, "E17.10.0.2", {"start": v(160.77, -513.2) * mm, "end": v(160.77, -467.2) * mm});
            skArc(sketch, "E17.10.0.3", {"start": v(160.77, -513.2) * mm, "mid": v(161.35, -514.62) * mm, "end": v(162.77, -515.2) * mm});
            skPoint(sketch, "E17.10.0.4", {"position": v(170.77, -515.2) * mm});
            skPoint(sketch, "E17.10.0.5", {"position": v(160.77, -465.2) * mm});
            skLineSegment(sketch, "E17.10.0.6", {"start": v(162.77, -465.2) * mm, "end": v(168.77, -465.2) * mm});
            skLineSegment(sketch, "E17.10.0.7", {"start": v(162.77, -515.2) * mm, "end": v(168.77, -515.2) * mm});
            skPoint(sketch, "E17.10.0.8", {"position": v(170.77, -465.2) * mm});
            skArc(sketch, "E17.10.0.9", {"start": v(170.77, -467.2) * mm, "mid": v(170.18, -465.8) * mm, "end": v(168.77, -465.2) * mm});
            skArc(sketch, "E17.10.0.10", {"start": v(168.77, -515.2) * mm, "mid": v(170.18, -514.62) * mm, "end": v(170.77, -513.2) * mm});
            skArc(sketch, "E17.10.0.11", {"start": v(162.77, -465.2) * mm, "mid": v(161.35, -465.8) * mm, "end": v(160.77, -467.2) * mm});
            skLineSegment(sketch, "E17.10.1.0", {"start": v(170.77, -453.2) * mm, "end": v(170.77, -407.2) * mm});
            skPoint(sketch, "E17.10.1.1", {"position": v(160.77, -455.2) * mm});
            skLineSegment(sketch, "E17.10.1.2", {"start": v(160.77, -453.2) * mm, "end": v(160.77, -407.2) * mm});
            skArc(sketch, "E17.10.1.3", {"start": v(160.77, -453.2) * mm, "mid": v(161.35, -454.62) * mm, "end": v(162.77, -455.2) * mm});
            skPoint(sketch, "E17.10.1.4", {"position": v(170.77, -455.2) * mm});
            skPoint(sketch, "E17.10.1.5", {"position": v(160.77, -405.2) * mm});
            skLineSegment(sketch, "E17.10.1.6", {"start": v(162.77, -405.2) * mm, "end": v(168.77, -405.2) * mm});
            skLineSegment(sketch, "E17.10.1.7", {"start": v(162.77, -455.2) * mm, "end": v(168.77, -455.2) * mm});
            skPoint(sketch, "E17.10.1.8", {"position": v(170.77, -405.2) * mm});
            skArc(sketch, "E17.10.1.9", {"start": v(170.77, -407.2) * mm, "mid": v(170.18, -405.8) * mm, "end": v(168.77, -405.2) * mm});
            skArc(sketch, "E17.10.1.10", {"start": v(168.77, -455.2) * mm, "mid": v(170.18, -454.62) * mm, "end": v(170.77, -453.2) * mm});
            skArc(sketch, "E17.10.1.11", {"start": v(162.77, -405.2) * mm, "mid": v(161.35, -405.8) * mm, "end": v(160.77, -407.2) * mm});
            skLineSegment(sketch, "E17.10.2.0", {"start": v(170.77, -393.2) * mm, "end": v(170.77, -347.2) * mm});
            skPoint(sketch, "E17.10.2.1", {"position": v(160.77, -395.2) * mm});
            skLineSegment(sketch, "E17.10.2.2", {"start": v(160.77, -393.2) * mm, "end": v(160.77, -347.2) * mm});
            skArc(sketch, "E17.10.2.3", {"start": v(160.77, -393.2) * mm, "mid": v(161.35, -394.62) * mm, "end": v(162.77, -395.2) * mm});
            skPoint(sketch, "E17.10.2.4", {"position": v(170.77, -395.2) * mm});
            skPoint(sketch, "E17.10.2.5", {"position": v(160.77, -345.2) * mm});
            skLineSegment(sketch, "E17.10.2.6", {"start": v(162.77, -345.2) * mm, "end": v(168.77, -345.2) * mm});
            skLineSegment(sketch, "E17.10.2.7", {"start": v(162.77, -395.2) * mm, "end": v(168.77, -395.2) * mm});
            skPoint(sketch, "E17.10.2.8", {"position": v(170.77, -345.2) * mm});
            skArc(sketch, "E17.10.2.9", {"start": v(170.77, -347.2) * mm, "mid": v(170.18, -345.8) * mm, "end": v(168.77, -345.2) * mm});
            skArc(sketch, "E17.10.2.10", {"start": v(168.77, -395.2) * mm, "mid": v(170.18, -394.62) * mm, "end": v(170.77, -393.2) * mm});
            skArc(sketch, "E17.10.2.11", {"start": v(162.77, -345.2) * mm, "mid": v(161.35, -345.8) * mm, "end": v(160.77, -347.2) * mm});
            skLineSegment(sketch, "E17.10.3.0", {"start": v(170.77, -333.2) * mm, "end": v(170.77, -287.2) * mm});
            skPoint(sketch, "E17.10.3.1", {"position": v(160.77, -335.2) * mm});
            skLineSegment(sketch, "E17.10.3.2", {"start": v(160.77, -333.2) * mm, "end": v(160.77, -287.2) * mm});
            skArc(sketch, "E17.10.3.3", {"start": v(160.77, -333.2) * mm, "mid": v(161.35, -334.62) * mm, "end": v(162.77, -335.2) * mm});
            skPoint(sketch, "E17.10.3.4", {"position": v(170.77, -335.2) * mm});
            skPoint(sketch, "E17.10.3.5", {"position": v(160.77, -285.2) * mm});
            skLineSegment(sketch, "E17.10.3.6", {"start": v(162.77, -285.2) * mm, "end": v(168.77, -285.2) * mm});
            skLineSegment(sketch, "E17.10.3.7", {"start": v(162.77, -335.2) * mm, "end": v(168.77, -335.2) * mm});
            skPoint(sketch, "E17.10.3.8", {"position": v(170.77, -285.2) * mm});
            skArc(sketch, "E17.10.3.9", {"start": v(170.77, -287.2) * mm, "mid": v(170.18, -285.8) * mm, "end": v(168.77, -285.2) * mm});
            skArc(sketch, "E17.10.3.10", {"start": v(168.77, -335.2) * mm, "mid": v(170.18, -334.62) * mm, "end": v(170.77, -333.2) * mm});
            skArc(sketch, "E17.10.3.11", {"start": v(162.77, -285.2) * mm, "mid": v(161.35, -285.8) * mm, "end": v(160.77, -287.2) * mm});
            skLineSegment(sketch, "E17.10.4.0", {"start": v(170.77, -273.2) * mm, "end": v(170.77, -227.2) * mm});
            skPoint(sketch, "E17.10.4.1", {"position": v(160.77, -275.2) * mm});
            skLineSegment(sketch, "E17.10.4.2", {"start": v(160.77, -273.2) * mm, "end": v(160.77, -227.2) * mm});
            skArc(sketch, "E17.10.4.3", {"start": v(160.77, -273.2) * mm, "mid": v(161.35, -274.62) * mm, "end": v(162.77, -275.2) * mm});
            skPoint(sketch, "E17.10.4.4", {"position": v(170.77, -275.2) * mm});
            skPoint(sketch, "E17.10.4.5", {"position": v(160.77, -225.2) * mm});
            skLineSegment(sketch, "E17.10.4.6", {"start": v(162.77, -225.2) * mm, "end": v(168.77, -225.2) * mm});
            skLineSegment(sketch, "E17.10.4.7", {"start": v(162.77, -275.2) * mm, "end": v(168.77, -275.2) * mm});
            skPoint(sketch, "E17.10.4.8", {"position": v(170.77, -225.2) * mm});
            skArc(sketch, "E17.10.4.9", {"start": v(170.77, -227.2) * mm, "mid": v(170.18, -225.8) * mm, "end": v(168.77, -225.2) * mm});
            skArc(sketch, "E17.10.4.10", {"start": v(168.77, -275.2) * mm, "mid": v(170.18, -274.62) * mm, "end": v(170.77, -273.2) * mm});
            skArc(sketch, "E17.10.4.11", {"start": v(162.77, -225.2) * mm, "mid": v(161.35, -225.8) * mm, "end": v(160.77, -227.2) * mm});
            skLineSegment(sketch, "E17.11.0.0", {"start": v(186.27, -513.2) * mm, "end": v(186.27, -467.2) * mm});
            skPoint(sketch, "E17.11.0.1", {"position": v(176.27, -515.2) * mm});
            skLineSegment(sketch, "E17.11.0.2", {"start": v(176.27, -513.2) * mm, "end": v(176.27, -467.2) * mm});
            skArc(sketch, "E17.11.0.3", {"start": v(176.27, -513.2) * mm, "mid": v(176.85, -514.62) * mm, "end": v(178.27, -515.2) * mm});
            skPoint(sketch, "E17.11.0.4", {"position": v(186.27, -515.2) * mm});
            skPoint(sketch, "E17.11.0.5", {"position": v(176.27, -465.2) * mm});
            skLineSegment(sketch, "E17.11.0.6", {"start": v(178.27, -465.2) * mm, "end": v(184.27, -465.2) * mm});
            skLineSegment(sketch, "E17.11.0.7", {"start": v(178.27, -515.2) * mm, "end": v(184.27, -515.2) * mm});
            skPoint(sketch, "E17.11.0.8", {"position": v(186.27, -465.2) * mm});
            skArc(sketch, "E17.11.0.9", {"start": v(186.27, -467.2) * mm, "mid": v(185.68, -465.8) * mm, "end": v(184.27, -465.2) * mm});
            skArc(sketch, "E17.11.0.10", {"start": v(184.27, -515.2) * mm, "mid": v(185.68, -514.62) * mm, "end": v(186.27, -513.2) * mm});
            skArc(sketch, "E17.11.0.11", {"start": v(178.27, -465.2) * mm, "mid": v(176.85, -465.8) * mm, "end": v(176.27, -467.2) * mm});
            skLineSegment(sketch, "E17.11.1.0", {"start": v(186.27, -453.2) * mm, "end": v(186.27, -407.2) * mm});
            skPoint(sketch, "E17.11.1.1", {"position": v(176.27, -455.2) * mm});
            skLineSegment(sketch, "E17.11.1.2", {"start": v(176.27, -453.2) * mm, "end": v(176.27, -407.2) * mm});
            skArc(sketch, "E17.11.1.3", {"start": v(176.27, -453.2) * mm, "mid": v(176.85, -454.62) * mm, "end": v(178.27, -455.2) * mm});
            skPoint(sketch, "E17.11.1.4", {"position": v(186.27, -455.2) * mm});
            skPoint(sketch, "E17.11.1.5", {"position": v(176.27, -405.2) * mm});
            skLineSegment(sketch, "E17.11.1.6", {"start": v(178.27, -405.2) * mm, "end": v(184.27, -405.2) * mm});
            skLineSegment(sketch, "E17.11.1.7", {"start": v(178.27, -455.2) * mm, "end": v(184.27, -455.2) * mm});
            skPoint(sketch, "E17.11.1.8", {"position": v(186.27, -405.2) * mm});
            skArc(sketch, "E17.11.1.9", {"start": v(186.27, -407.2) * mm, "mid": v(185.68, -405.8) * mm, "end": v(184.27, -405.2) * mm});
            skArc(sketch, "E17.11.1.10", {"start": v(184.27, -455.2) * mm, "mid": v(185.68, -454.62) * mm, "end": v(186.27, -453.2) * mm});
            skArc(sketch, "E17.11.1.11", {"start": v(178.27, -405.2) * mm, "mid": v(176.85, -405.8) * mm, "end": v(176.27, -407.2) * mm});
            skLineSegment(sketch, "E17.11.2.0", {"start": v(186.27, -393.2) * mm, "end": v(186.27, -347.2) * mm});
            skPoint(sketch, "E17.11.2.1", {"position": v(176.27, -395.2) * mm});
            skLineSegment(sketch, "E17.11.2.2", {"start": v(176.27, -393.2) * mm, "end": v(176.27, -347.2) * mm});
            skArc(sketch, "E17.11.2.3", {"start": v(176.27, -393.2) * mm, "mid": v(176.85, -394.62) * mm, "end": v(178.27, -395.2) * mm});
            skPoint(sketch, "E17.11.2.4", {"position": v(186.27, -395.2) * mm});
            skPoint(sketch, "E17.11.2.5", {"position": v(176.27, -345.2) * mm});
            skLineSegment(sketch, "E17.11.2.6", {"start": v(178.27, -345.2) * mm, "end": v(184.27, -345.2) * mm});
            skLineSegment(sketch, "E17.11.2.7", {"start": v(178.27, -395.2) * mm, "end": v(184.27, -395.2) * mm});
            skPoint(sketch, "E17.11.2.8", {"position": v(186.27, -345.2) * mm});
            skArc(sketch, "E17.11.2.9", {"start": v(186.27, -347.2) * mm, "mid": v(185.68, -345.8) * mm, "end": v(184.27, -345.2) * mm});
            skArc(sketch, "E17.11.2.10", {"start": v(184.27, -395.2) * mm, "mid": v(185.68, -394.62) * mm, "end": v(186.27, -393.2) * mm});
            skArc(sketch, "E17.11.2.11", {"start": v(178.27, -345.2) * mm, "mid": v(176.85, -345.8) * mm, "end": v(176.27, -347.2) * mm});
            skLineSegment(sketch, "E17.11.3.0", {"start": v(186.27, -333.2) * mm, "end": v(186.27, -287.2) * mm});
            skPoint(sketch, "E17.11.3.1", {"position": v(176.27, -335.2) * mm});
            skLineSegment(sketch, "E17.11.3.2", {"start": v(176.27, -333.2) * mm, "end": v(176.27, -287.2) * mm});
            skArc(sketch, "E17.11.3.3", {"start": v(176.27, -333.2) * mm, "mid": v(176.85, -334.62) * mm, "end": v(178.27, -335.2) * mm});
            skPoint(sketch, "E17.11.3.4", {"position": v(186.27, -335.2) * mm});
            skPoint(sketch, "E17.11.3.5", {"position": v(176.27, -285.2) * mm});
            skLineSegment(sketch, "E17.11.3.6", {"start": v(178.27, -285.2) * mm, "end": v(184.27, -285.2) * mm});
            skLineSegment(sketch, "E17.11.3.7", {"start": v(178.27, -335.2) * mm, "end": v(184.27, -335.2) * mm});
            skPoint(sketch, "E17.11.3.8", {"position": v(186.27, -285.2) * mm});
            skArc(sketch, "E17.11.3.9", {"start": v(186.27, -287.2) * mm, "mid": v(185.68, -285.8) * mm, "end": v(184.27, -285.2) * mm});
            skArc(sketch, "E17.11.3.10", {"start": v(184.27, -335.2) * mm, "mid": v(185.68, -334.62) * mm, "end": v(186.27, -333.2) * mm});
            skArc(sketch, "E17.11.3.11", {"start": v(178.27, -285.2) * mm, "mid": v(176.85, -285.8) * mm, "end": v(176.27, -287.2) * mm});
            skLineSegment(sketch, "E17.11.4.0", {"start": v(186.27, -273.2) * mm, "end": v(186.27, -227.2) * mm});
            skPoint(sketch, "E17.11.4.1", {"position": v(176.27, -275.2) * mm});
            skLineSegment(sketch, "E17.11.4.2", {"start": v(176.27, -273.2) * mm, "end": v(176.27, -227.2) * mm});
            skArc(sketch, "E17.11.4.3", {"start": v(176.27, -273.2) * mm, "mid": v(176.85, -274.62) * mm, "end": v(178.27, -275.2) * mm});
            skPoint(sketch, "E17.11.4.4", {"position": v(186.27, -275.2) * mm});
            skPoint(sketch, "E17.11.4.5", {"position": v(176.27, -225.2) * mm});
            skLineSegment(sketch, "E17.11.4.6", {"start": v(178.27, -225.2) * mm, "end": v(184.27, -225.2) * mm});
            skLineSegment(sketch, "E17.11.4.7", {"start": v(178.27, -275.2) * mm, "end": v(184.27, -275.2) * mm});
            skPoint(sketch, "E17.11.4.8", {"position": v(186.27, -225.2) * mm});
            skArc(sketch, "E17.11.4.9", {"start": v(186.27, -227.2) * mm, "mid": v(185.68, -225.8) * mm, "end": v(184.27, -225.2) * mm});
            skArc(sketch, "E17.11.4.10", {"start": v(184.27, -275.2) * mm, "mid": v(185.68, -274.62) * mm, "end": v(186.27, -273.2) * mm});
            skArc(sketch, "E17.11.4.11", {"start": v(178.27, -225.2) * mm, "mid": v(176.85, -225.8) * mm, "end": v(176.27, -227.2) * mm});
            skLineSegment(sketch, "E17.12.0.0", {"start": v(201.77, -513.2) * mm, "end": v(201.77, -467.2) * mm});
            skPoint(sketch, "E17.12.0.1", {"position": v(191.77, -515.2) * mm});
            skLineSegment(sketch, "E17.12.0.2", {"start": v(191.77, -513.2) * mm, "end": v(191.77, -467.2) * mm});
            skArc(sketch, "E17.12.0.3", {"start": v(191.77, -513.2) * mm, "mid": v(192.35, -514.62) * mm, "end": v(193.77, -515.2) * mm});
            skPoint(sketch, "E17.12.0.4", {"position": v(201.77, -515.2) * mm});
            skPoint(sketch, "E17.12.0.5", {"position": v(191.77, -465.2) * mm});
            skLineSegment(sketch, "E17.12.0.6", {"start": v(193.77, -465.2) * mm, "end": v(199.77, -465.2) * mm});
            skLineSegment(sketch, "E17.12.0.7", {"start": v(193.77, -515.2) * mm, "end": v(199.77, -515.2) * mm});
            skPoint(sketch, "E17.12.0.8", {"position": v(201.77, -465.2) * mm});
            skArc(sketch, "E17.12.0.9", {"start": v(201.77, -467.2) * mm, "mid": v(201.18, -465.8) * mm, "end": v(199.77, -465.2) * mm});
            skArc(sketch, "E17.12.0.10", {"start": v(199.77, -515.2) * mm, "mid": v(201.18, -514.62) * mm, "end": v(201.77, -513.2) * mm});
            skArc(sketch, "E17.12.0.11", {"start": v(193.77, -465.2) * mm, "mid": v(192.35, -465.8) * mm, "end": v(191.77, -467.2) * mm});
            skLineSegment(sketch, "E17.12.1.0", {"start": v(201.77, -453.2) * mm, "end": v(201.77, -407.2) * mm});
            skPoint(sketch, "E17.12.1.1", {"position": v(191.77, -455.2) * mm});
            skLineSegment(sketch, "E17.12.1.2", {"start": v(191.77, -453.2) * mm, "end": v(191.77, -407.2) * mm});
            skArc(sketch, "E17.12.1.3", {"start": v(191.77, -453.2) * mm, "mid": v(192.35, -454.62) * mm, "end": v(193.77, -455.2) * mm});
            skPoint(sketch, "E17.12.1.4", {"position": v(201.77, -455.2) * mm});
            skPoint(sketch, "E17.12.1.5", {"position": v(191.77, -405.2) * mm});
            skLineSegment(sketch, "E17.12.1.6", {"start": v(193.77, -405.2) * mm, "end": v(199.77, -405.2) * mm});
            skLineSegment(sketch, "E17.12.1.7", {"start": v(193.77, -455.2) * mm, "end": v(199.77, -455.2) * mm});
            skPoint(sketch, "E17.12.1.8", {"position": v(201.77, -405.2) * mm});
            skArc(sketch, "E17.12.1.9", {"start": v(201.77, -407.2) * mm, "mid": v(201.18, -405.8) * mm, "end": v(199.77, -405.2) * mm});
            skArc(sketch, "E17.12.1.10", {"start": v(199.77, -455.2) * mm, "mid": v(201.18, -454.62) * mm, "end": v(201.77, -453.2) * mm});
            skArc(sketch, "E17.12.1.11", {"start": v(193.77, -405.2) * mm, "mid": v(192.35, -405.8) * mm, "end": v(191.77, -407.2) * mm});
            skLineSegment(sketch, "E17.12.2.0", {"start": v(201.77, -393.2) * mm, "end": v(201.77, -347.2) * mm});
            skPoint(sketch, "E17.12.2.1", {"position": v(191.77, -395.2) * mm});
            skLineSegment(sketch, "E17.12.2.2", {"start": v(191.77, -393.2) * mm, "end": v(191.77, -347.2) * mm});
            skArc(sketch, "E17.12.2.3", {"start": v(191.77, -393.2) * mm, "mid": v(192.35, -394.62) * mm, "end": v(193.77, -395.2) * mm});
            skPoint(sketch, "E17.12.2.4", {"position": v(201.77, -395.2) * mm});
            skPoint(sketch, "E17.12.2.5", {"position": v(191.77, -345.2) * mm});
            skLineSegment(sketch, "E17.12.2.6", {"start": v(193.77, -345.2) * mm, "end": v(199.77, -345.2) * mm});
            skLineSegment(sketch, "E17.12.2.7", {"start": v(193.77, -395.2) * mm, "end": v(199.77, -395.2) * mm});
            skPoint(sketch, "E17.12.2.8", {"position": v(201.77, -345.2) * mm});
            skArc(sketch, "E17.12.2.9", {"start": v(201.77, -347.2) * mm, "mid": v(201.18, -345.8) * mm, "end": v(199.77, -345.2) * mm});
            skArc(sketch, "E17.12.2.10", {"start": v(199.77, -395.2) * mm, "mid": v(201.18, -394.62) * mm, "end": v(201.77, -393.2) * mm});
            skArc(sketch, "E17.12.2.11", {"start": v(193.77, -345.2) * mm, "mid": v(192.35, -345.8) * mm, "end": v(191.77, -347.2) * mm});
            skLineSegment(sketch, "E17.12.3.0", {"start": v(201.77, -333.2) * mm, "end": v(201.77, -287.2) * mm});
            skPoint(sketch, "E17.12.3.1", {"position": v(191.77, -335.2) * mm});
            skLineSegment(sketch, "E17.12.3.2", {"start": v(191.77, -333.2) * mm, "end": v(191.77, -287.2) * mm});
            skArc(sketch, "E17.12.3.3", {"start": v(191.77, -333.2) * mm, "mid": v(192.35, -334.62) * mm, "end": v(193.77, -335.2) * mm});
            skPoint(sketch, "E17.12.3.4", {"position": v(201.77, -335.2) * mm});
            skPoint(sketch, "E17.12.3.5", {"position": v(191.77, -285.2) * mm});
            skLineSegment(sketch, "E17.12.3.6", {"start": v(193.77, -285.2) * mm, "end": v(199.77, -285.2) * mm});
            skLineSegment(sketch, "E17.12.3.7", {"start": v(193.77, -335.2) * mm, "end": v(199.77, -335.2) * mm});
            skPoint(sketch, "E17.12.3.8", {"position": v(201.77, -285.2) * mm});
            skArc(sketch, "E17.12.3.9", {"start": v(201.77, -287.2) * mm, "mid": v(201.18, -285.8) * mm, "end": v(199.77, -285.2) * mm});
            skArc(sketch, "E17.12.3.10", {"start": v(199.77, -335.2) * mm, "mid": v(201.18, -334.62) * mm, "end": v(201.77, -333.2) * mm});
            skArc(sketch, "E17.12.3.11", {"start": v(193.77, -285.2) * mm, "mid": v(192.35, -285.8) * mm, "end": v(191.77, -287.2) * mm});
            skLineSegment(sketch, "E17.12.4.0", {"start": v(201.77, -273.2) * mm, "end": v(201.77, -227.2) * mm});
            skPoint(sketch, "E17.12.4.1", {"position": v(191.77, -275.2) * mm});
            skLineSegment(sketch, "E17.12.4.2", {"start": v(191.77, -273.2) * mm, "end": v(191.77, -227.2) * mm});
            skArc(sketch, "E17.12.4.3", {"start": v(191.77, -273.2) * mm, "mid": v(192.35, -274.62) * mm, "end": v(193.77, -275.2) * mm});
            skPoint(sketch, "E17.12.4.4", {"position": v(201.77, -275.2) * mm});
            skPoint(sketch, "E17.12.4.5", {"position": v(191.77, -225.2) * mm});
            skLineSegment(sketch, "E17.12.4.6", {"start": v(193.77, -225.2) * mm, "end": v(199.77, -225.2) * mm});
            skLineSegment(sketch, "E17.12.4.7", {"start": v(193.77, -275.2) * mm, "end": v(199.77, -275.2) * mm});
            skPoint(sketch, "E17.12.4.8", {"position": v(201.77, -225.2) * mm});
            skArc(sketch, "E17.12.4.9", {"start": v(201.77, -227.2) * mm, "mid": v(201.18, -225.8) * mm, "end": v(199.77, -225.2) * mm});
            skArc(sketch, "E17.12.4.10", {"start": v(199.77, -275.2) * mm, "mid": v(201.18, -274.62) * mm, "end": v(201.77, -273.2) * mm});
            skArc(sketch, "E17.12.4.11", {"start": v(193.77, -225.2) * mm, "mid": v(192.35, -225.8) * mm, "end": v(191.77, -227.2) * mm});
            skLineSegment(sketch, "E17.13.0.0", {"start": v(217.27, -513.2) * mm, "end": v(217.27, -467.2) * mm});
            skPoint(sketch, "E17.13.0.1", {"position": v(207.27, -515.2) * mm});
            skLineSegment(sketch, "E17.13.0.2", {"start": v(207.27, -513.2) * mm, "end": v(207.27, -467.2) * mm});
            skArc(sketch, "E17.13.0.3", {"start": v(207.27, -513.2) * mm, "mid": v(207.85, -514.62) * mm, "end": v(209.27, -515.2) * mm});
            skPoint(sketch, "E17.13.0.4", {"position": v(217.27, -515.2) * mm});
            skPoint(sketch, "E17.13.0.5", {"position": v(207.27, -465.2) * mm});
            skLineSegment(sketch, "E17.13.0.6", {"start": v(209.27, -465.2) * mm, "end": v(215.27, -465.2) * mm});
            skLineSegment(sketch, "E17.13.0.7", {"start": v(209.27, -515.2) * mm, "end": v(215.27, -515.2) * mm});
            skPoint(sketch, "E17.13.0.8", {"position": v(217.27, -465.2) * mm});
            skArc(sketch, "E17.13.0.9", {"start": v(217.27, -467.2) * mm, "mid": v(216.68, -465.8) * mm, "end": v(215.27, -465.2) * mm});
            skArc(sketch, "E17.13.0.10", {"start": v(215.27, -515.2) * mm, "mid": v(216.68, -514.62) * mm, "end": v(217.27, -513.2) * mm});
            skArc(sketch, "E17.13.0.11", {"start": v(209.27, -465.2) * mm, "mid": v(207.85, -465.8) * mm, "end": v(207.27, -467.2) * mm});
            skLineSegment(sketch, "E17.13.1.0", {"start": v(217.27, -453.2) * mm, "end": v(217.27, -407.2) * mm});
            skPoint(sketch, "E17.13.1.1", {"position": v(207.27, -455.2) * mm});
            skLineSegment(sketch, "E17.13.1.2", {"start": v(207.27, -453.2) * mm, "end": v(207.27, -407.2) * mm});
            skArc(sketch, "E17.13.1.3", {"start": v(207.27, -453.2) * mm, "mid": v(207.85, -454.62) * mm, "end": v(209.27, -455.2) * mm});
            skPoint(sketch, "E17.13.1.4", {"position": v(217.27, -455.2) * mm});
            skPoint(sketch, "E17.13.1.5", {"position": v(207.27, -405.2) * mm});
            skLineSegment(sketch, "E17.13.1.6", {"start": v(209.27, -405.2) * mm, "end": v(215.27, -405.2) * mm});
            skLineSegment(sketch, "E17.13.1.7", {"start": v(209.27, -455.2) * mm, "end": v(215.27, -455.2) * mm});
            skPoint(sketch, "E17.13.1.8", {"position": v(217.27, -405.2) * mm});
            skArc(sketch, "E17.13.1.9", {"start": v(217.27, -407.2) * mm, "mid": v(216.68, -405.8) * mm, "end": v(215.27, -405.2) * mm});
            skArc(sketch, "E17.13.1.10", {"start": v(215.27, -455.2) * mm, "mid": v(216.68, -454.62) * mm, "end": v(217.27, -453.2) * mm});
            skArc(sketch, "E17.13.1.11", {"start": v(209.27, -405.2) * mm, "mid": v(207.85, -405.8) * mm, "end": v(207.27, -407.2) * mm});
            skLineSegment(sketch, "E17.13.2.0", {"start": v(217.27, -393.2) * mm, "end": v(217.27, -347.2) * mm});
            skPoint(sketch, "E17.13.2.1", {"position": v(207.27, -395.2) * mm});
            skLineSegment(sketch, "E17.13.2.2", {"start": v(207.27, -393.2) * mm, "end": v(207.27, -347.2) * mm});
            skArc(sketch, "E17.13.2.3", {"start": v(207.27, -393.2) * mm, "mid": v(207.85, -394.62) * mm, "end": v(209.27, -395.2) * mm});
            skPoint(sketch, "E17.13.2.4", {"position": v(217.27, -395.2) * mm});
            skPoint(sketch, "E17.13.2.5", {"position": v(207.27, -345.2) * mm});
            skLineSegment(sketch, "E17.13.2.6", {"start": v(209.27, -345.2) * mm, "end": v(215.27, -345.2) * mm});
            skLineSegment(sketch, "E17.13.2.7", {"start": v(209.27, -395.2) * mm, "end": v(215.27, -395.2) * mm});
            skPoint(sketch, "E17.13.2.8", {"position": v(217.27, -345.2) * mm});
            skArc(sketch, "E17.13.2.9", {"start": v(217.27, -347.2) * mm, "mid": v(216.68, -345.8) * mm, "end": v(215.27, -345.2) * mm});
            skArc(sketch, "E17.13.2.10", {"start": v(215.27, -395.2) * mm, "mid": v(216.68, -394.62) * mm, "end": v(217.27, -393.2) * mm});
            skArc(sketch, "E17.13.2.11", {"start": v(209.27, -345.2) * mm, "mid": v(207.85, -345.8) * mm, "end": v(207.27, -347.2) * mm});
            skLineSegment(sketch, "E17.13.3.0", {"start": v(217.27, -333.2) * mm, "end": v(217.27, -287.2) * mm});
            skPoint(sketch, "E17.13.3.1", {"position": v(207.27, -335.2) * mm});
            skLineSegment(sketch, "E17.13.3.2", {"start": v(207.27, -333.2) * mm, "end": v(207.27, -287.2) * mm});
            skArc(sketch, "E17.13.3.3", {"start": v(207.27, -333.2) * mm, "mid": v(207.85, -334.62) * mm, "end": v(209.27, -335.2) * mm});
            skPoint(sketch, "E17.13.3.4", {"position": v(217.27, -335.2) * mm});
            skPoint(sketch, "E17.13.3.5", {"position": v(207.27, -285.2) * mm});
            skLineSegment(sketch, "E17.13.3.6", {"start": v(209.27, -285.2) * mm, "end": v(215.27, -285.2) * mm});
            skLineSegment(sketch, "E17.13.3.7", {"start": v(209.27, -335.2) * mm, "end": v(215.27, -335.2) * mm});
            skPoint(sketch, "E17.13.3.8", {"position": v(217.27, -285.2) * mm});
            skArc(sketch, "E17.13.3.9", {"start": v(217.27, -287.2) * mm, "mid": v(216.68, -285.8) * mm, "end": v(215.27, -285.2) * mm});
            skArc(sketch, "E17.13.3.10", {"start": v(215.27, -335.2) * mm, "mid": v(216.68, -334.62) * mm, "end": v(217.27, -333.2) * mm});
            skArc(sketch, "E17.13.3.11", {"start": v(209.27, -285.2) * mm, "mid": v(207.85, -285.8) * mm, "end": v(207.27, -287.2) * mm});
            skLineSegment(sketch, "E17.13.4.0", {"start": v(217.27, -273.2) * mm, "end": v(217.27, -227.2) * mm});
            skPoint(sketch, "E17.13.4.1", {"position": v(207.27, -275.2) * mm});
            skLineSegment(sketch, "E17.13.4.2", {"start": v(207.27, -273.2) * mm, "end": v(207.27, -227.2) * mm});
            skArc(sketch, "E17.13.4.3", {"start": v(207.27, -273.2) * mm, "mid": v(207.85, -274.62) * mm, "end": v(209.27, -275.2) * mm});
            skPoint(sketch, "E17.13.4.4", {"position": v(217.27, -275.2) * mm});
            skPoint(sketch, "E17.13.4.5", {"position": v(207.27, -225.2) * mm});
            skLineSegment(sketch, "E17.13.4.6", {"start": v(209.27, -225.2) * mm, "end": v(215.27, -225.2) * mm});
            skLineSegment(sketch, "E17.13.4.7", {"start": v(209.27, -275.2) * mm, "end": v(215.27, -275.2) * mm});
            skPoint(sketch, "E17.13.4.8", {"position": v(217.27, -225.2) * mm});
            skArc(sketch, "E17.13.4.9", {"start": v(217.27, -227.2) * mm, "mid": v(216.68, -225.8) * mm, "end": v(215.27, -225.2) * mm});
            skArc(sketch, "E17.13.4.10", {"start": v(215.27, -275.2) * mm, "mid": v(216.68, -274.62) * mm, "end": v(217.27, -273.2) * mm});
            skArc(sketch, "E17.13.4.11", {"start": v(209.27, -225.2) * mm, "mid": v(207.85, -225.8) * mm, "end": v(207.27, -227.2) * mm});
            skLineSegment(sketch, "E17.14.0.0", {"start": v(232.77, -513.2) * mm, "end": v(232.77, -467.2) * mm});
            skPoint(sketch, "E17.14.0.1", {"position": v(222.77, -515.2) * mm});
            skLineSegment(sketch, "E17.14.0.2", {"start": v(222.77, -513.2) * mm, "end": v(222.77, -467.2) * mm});
            skArc(sketch, "E17.14.0.3", {"start": v(222.77, -513.2) * mm, "mid": v(223.35, -514.62) * mm, "end": v(224.77, -515.2) * mm});
            skPoint(sketch, "E17.14.0.4", {"position": v(232.77, -515.2) * mm});
            skPoint(sketch, "E17.14.0.5", {"position": v(222.77, -465.2) * mm});
            skLineSegment(sketch, "E17.14.0.6", {"start": v(224.77, -465.2) * mm, "end": v(230.77, -465.2) * mm});
            skLineSegment(sketch, "E17.14.0.7", {"start": v(224.77, -515.2) * mm, "end": v(230.77, -515.2) * mm});
            skPoint(sketch, "E17.14.0.8", {"position": v(232.77, -465.2) * mm});
            skArc(sketch, "E17.14.0.9", {"start": v(232.77, -467.2) * mm, "mid": v(232.18, -465.8) * mm, "end": v(230.77, -465.2) * mm});
            skArc(sketch, "E17.14.0.10", {"start": v(230.77, -515.2) * mm, "mid": v(232.18, -514.62) * mm, "end": v(232.77, -513.2) * mm});
            skArc(sketch, "E17.14.0.11", {"start": v(224.77, -465.2) * mm, "mid": v(223.35, -465.8) * mm, "end": v(222.77, -467.2) * mm});
            skLineSegment(sketch, "E17.14.1.0", {"start": v(232.77, -453.2) * mm, "end": v(232.77, -407.2) * mm});
            skPoint(sketch, "E17.14.1.1", {"position": v(222.77, -455.2) * mm});
            skLineSegment(sketch, "E17.14.1.2", {"start": v(222.77, -453.2) * mm, "end": v(222.77, -407.2) * mm});
            skArc(sketch, "E17.14.1.3", {"start": v(222.77, -453.2) * mm, "mid": v(223.35, -454.62) * mm, "end": v(224.77, -455.2) * mm});
            skPoint(sketch, "E17.14.1.4", {"position": v(232.77, -455.2) * mm});
            skPoint(sketch, "E17.14.1.5", {"position": v(222.77, -405.2) * mm});
            skLineSegment(sketch, "E17.14.1.6", {"start": v(224.77, -405.2) * mm, "end": v(230.77, -405.2) * mm});
            skLineSegment(sketch, "E17.14.1.7", {"start": v(224.77, -455.2) * mm, "end": v(230.77, -455.2) * mm});
            skPoint(sketch, "E17.14.1.8", {"position": v(232.77, -405.2) * mm});
            skArc(sketch, "E17.14.1.9", {"start": v(232.77, -407.2) * mm, "mid": v(232.18, -405.8) * mm, "end": v(230.77, -405.2) * mm});
            skArc(sketch, "E17.14.1.10", {"start": v(230.77, -455.2) * mm, "mid": v(232.18, -454.62) * mm, "end": v(232.77, -453.2) * mm});
            skArc(sketch, "E17.14.1.11", {"start": v(224.77, -405.2) * mm, "mid": v(223.35, -405.8) * mm, "end": v(222.77, -407.2) * mm});
            skLineSegment(sketch, "E17.14.2.0", {"start": v(232.77, -393.2) * mm, "end": v(232.77, -347.2) * mm});
            skPoint(sketch, "E17.14.2.1", {"position": v(222.77, -395.2) * mm});
            skLineSegment(sketch, "E17.14.2.2", {"start": v(222.77, -393.2) * mm, "end": v(222.77, -347.2) * mm});
            skArc(sketch, "E17.14.2.3", {"start": v(222.77, -393.2) * mm, "mid": v(223.35, -394.62) * mm, "end": v(224.77, -395.2) * mm});
            skPoint(sketch, "E17.14.2.4", {"position": v(232.77, -395.2) * mm});
            skPoint(sketch, "E17.14.2.5", {"position": v(222.77, -345.2) * mm});
            skLineSegment(sketch, "E17.14.2.6", {"start": v(224.77, -345.2) * mm, "end": v(230.77, -345.2) * mm});
            skLineSegment(sketch, "E17.14.2.7", {"start": v(224.77, -395.2) * mm, "end": v(230.77, -395.2) * mm});
            skPoint(sketch, "E17.14.2.8", {"position": v(232.77, -345.2) * mm});
            skArc(sketch, "E17.14.2.9", {"start": v(232.77, -347.2) * mm, "mid": v(232.18, -345.8) * mm, "end": v(230.77, -345.2) * mm});
            skArc(sketch, "E17.14.2.10", {"start": v(230.77, -395.2) * mm, "mid": v(232.18, -394.62) * mm, "end": v(232.77, -393.2) * mm});
            skArc(sketch, "E17.14.2.11", {"start": v(224.77, -345.2) * mm, "mid": v(223.35, -345.8) * mm, "end": v(222.77, -347.2) * mm});
            skLineSegment(sketch, "E17.14.3.0", {"start": v(232.77, -333.2) * mm, "end": v(232.77, -287.2) * mm});
            skPoint(sketch, "E17.14.3.1", {"position": v(222.77, -335.2) * mm});
            skLineSegment(sketch, "E17.14.3.2", {"start": v(222.77, -333.2) * mm, "end": v(222.77, -287.2) * mm});
            skArc(sketch, "E17.14.3.3", {"start": v(222.77, -333.2) * mm, "mid": v(223.35, -334.62) * mm, "end": v(224.77, -335.2) * mm});
            skPoint(sketch, "E17.14.3.4", {"position": v(232.77, -335.2) * mm});
            skPoint(sketch, "E17.14.3.5", {"position": v(222.77, -285.2) * mm});
            skLineSegment(sketch, "E17.14.3.6", {"start": v(224.77, -285.2) * mm, "end": v(230.77, -285.2) * mm});
            skLineSegment(sketch, "E17.14.3.7", {"start": v(224.77, -335.2) * mm, "end": v(230.77, -335.2) * mm});
            skPoint(sketch, "E17.14.3.8", {"position": v(232.77, -285.2) * mm});
            skArc(sketch, "E17.14.3.9", {"start": v(232.77, -287.2) * mm, "mid": v(232.18, -285.8) * mm, "end": v(230.77, -285.2) * mm});
            skArc(sketch, "E17.14.3.10", {"start": v(230.77, -335.2) * mm, "mid": v(232.18, -334.62) * mm, "end": v(232.77, -333.2) * mm});
            skArc(sketch, "E17.14.3.11", {"start": v(224.77, -285.2) * mm, "mid": v(223.35, -285.8) * mm, "end": v(222.77, -287.2) * mm});
            skLineSegment(sketch, "E17.14.4.0", {"start": v(232.77, -273.2) * mm, "end": v(232.77, -227.2) * mm});
            skPoint(sketch, "E17.14.4.1", {"position": v(222.77, -275.2) * mm});
            skLineSegment(sketch, "E17.14.4.2", {"start": v(222.77, -273.2) * mm, "end": v(222.77, -227.2) * mm});
            skArc(sketch, "E17.14.4.3", {"start": v(222.77, -273.2) * mm, "mid": v(223.35, -274.62) * mm, "end": v(224.77, -275.2) * mm});
            skPoint(sketch, "E17.14.4.4", {"position": v(232.77, -275.2) * mm});
            skPoint(sketch, "E17.14.4.5", {"position": v(222.77, -225.2) * mm});
            skLineSegment(sketch, "E17.14.4.6", {"start": v(224.77, -225.2) * mm, "end": v(230.77, -225.2) * mm});
            skLineSegment(sketch, "E17.14.4.7", {"start": v(224.77, -275.2) * mm, "end": v(230.77, -275.2) * mm});
            skPoint(sketch, "E17.14.4.8", {"position": v(232.77, -225.2) * mm});
            skArc(sketch, "E17.14.4.9", {"start": v(232.77, -227.2) * mm, "mid": v(232.18, -225.8) * mm, "end": v(230.77, -225.2) * mm});
            skArc(sketch, "E17.14.4.10", {"start": v(230.77, -275.2) * mm, "mid": v(232.18, -274.62) * mm, "end": v(232.77, -273.2) * mm});
            skArc(sketch, "E17.14.4.11", {"start": v(224.77, -225.2) * mm, "mid": v(223.35, -225.8) * mm, "end": v(222.77, -227.2) * mm});
            skLineSegment(sketch, "E17.15.0.0", {"start": v(248.27, -513.2) * mm, "end": v(248.27, -467.2) * mm});
            skPoint(sketch, "E17.15.0.1", {"position": v(238.27, -515.2) * mm});
            skLineSegment(sketch, "E17.15.0.2", {"start": v(238.27, -513.2) * mm, "end": v(238.27, -467.2) * mm});
            skArc(sketch, "E17.15.0.3", {"start": v(238.27, -513.2) * mm, "mid": v(238.85, -514.62) * mm, "end": v(240.27, -515.2) * mm});
            skPoint(sketch, "E17.15.0.4", {"position": v(248.27, -515.2) * mm});
            skPoint(sketch, "E17.15.0.5", {"position": v(238.27, -465.2) * mm});
            skLineSegment(sketch, "E17.15.0.6", {"start": v(240.27, -465.2) * mm, "end": v(246.27, -465.2) * mm});
            skLineSegment(sketch, "E17.15.0.7", {"start": v(240.27, -515.2) * mm, "end": v(246.27, -515.2) * mm});
            skPoint(sketch, "E17.15.0.8", {"position": v(248.27, -465.2) * mm});
            skArc(sketch, "E17.15.0.9", {"start": v(248.27, -467.2) * mm, "mid": v(247.68, -465.8) * mm, "end": v(246.27, -465.2) * mm});
            skArc(sketch, "E17.15.0.10", {"start": v(246.27, -515.2) * mm, "mid": v(247.68, -514.62) * mm, "end": v(248.27, -513.2) * mm});
            skArc(sketch, "E17.15.0.11", {"start": v(240.27, -465.2) * mm, "mid": v(238.85, -465.8) * mm, "end": v(238.27, -467.2) * mm});
            skLineSegment(sketch, "E17.15.1.0", {"start": v(248.27, -453.2) * mm, "end": v(248.27, -407.2) * mm});
            skPoint(sketch, "E17.15.1.1", {"position": v(238.27, -455.2) * mm});
            skLineSegment(sketch, "E17.15.1.2", {"start": v(238.27, -453.2) * mm, "end": v(238.27, -407.2) * mm});
            skArc(sketch, "E17.15.1.3", {"start": v(238.27, -453.2) * mm, "mid": v(238.85, -454.62) * mm, "end": v(240.27, -455.2) * mm});
            skPoint(sketch, "E17.15.1.4", {"position": v(248.27, -455.2) * mm});
            skPoint(sketch, "E17.15.1.5", {"position": v(238.27, -405.2) * mm});
            skLineSegment(sketch, "E17.15.1.6", {"start": v(240.27, -405.2) * mm, "end": v(246.27, -405.2) * mm});
            skLineSegment(sketch, "E17.15.1.7", {"start": v(240.27, -455.2) * mm, "end": v(246.27, -455.2) * mm});
            skPoint(sketch, "E17.15.1.8", {"position": v(248.27, -405.2) * mm});
            skArc(sketch, "E17.15.1.9", {"start": v(248.27, -407.2) * mm, "mid": v(247.68, -405.8) * mm, "end": v(246.27, -405.2) * mm});
            skArc(sketch, "E17.15.1.10", {"start": v(246.27, -455.2) * mm, "mid": v(247.68, -454.62) * mm, "end": v(248.27, -453.2) * mm});
            skArc(sketch, "E17.15.1.11", {"start": v(240.27, -405.2) * mm, "mid": v(238.85, -405.8) * mm, "end": v(238.27, -407.2) * mm});
            skLineSegment(sketch, "E17.15.2.0", {"start": v(248.27, -393.2) * mm, "end": v(248.27, -347.2) * mm});
            skPoint(sketch, "E17.15.2.1", {"position": v(238.27, -395.2) * mm});
            skLineSegment(sketch, "E17.15.2.2", {"start": v(238.27, -393.2) * mm, "end": v(238.27, -347.2) * mm});
            skArc(sketch, "E17.15.2.3", {"start": v(238.27, -393.2) * mm, "mid": v(238.85, -394.62) * mm, "end": v(240.27, -395.2) * mm});
            skPoint(sketch, "E17.15.2.4", {"position": v(248.27, -395.2) * mm});
            skPoint(sketch, "E17.15.2.5", {"position": v(238.27, -345.2) * mm});
            skLineSegment(sketch, "E17.15.2.6", {"start": v(240.27, -345.2) * mm, "end": v(246.27, -345.2) * mm});
            skLineSegment(sketch, "E17.15.2.7", {"start": v(240.27, -395.2) * mm, "end": v(246.27, -395.2) * mm});
            skPoint(sketch, "E17.15.2.8", {"position": v(248.27, -345.2) * mm});
            skArc(sketch, "E17.15.2.9", {"start": v(248.27, -347.2) * mm, "mid": v(247.68, -345.8) * mm, "end": v(246.27, -345.2) * mm});
            skArc(sketch, "E17.15.2.10", {"start": v(246.27, -395.2) * mm, "mid": v(247.68, -394.62) * mm, "end": v(248.27, -393.2) * mm});
            skArc(sketch, "E17.15.2.11", {"start": v(240.27, -345.2) * mm, "mid": v(238.85, -345.8) * mm, "end": v(238.27, -347.2) * mm});
            skLineSegment(sketch, "E17.15.3.0", {"start": v(248.27, -333.2) * mm, "end": v(248.27, -287.2) * mm});
            skPoint(sketch, "E17.15.3.1", {"position": v(238.27, -335.2) * mm});
            skLineSegment(sketch, "E17.15.3.2", {"start": v(238.27, -333.2) * mm, "end": v(238.27, -287.2) * mm});
            skArc(sketch, "E17.15.3.3", {"start": v(238.27, -333.2) * mm, "mid": v(238.85, -334.62) * mm, "end": v(240.27, -335.2) * mm});
            skPoint(sketch, "E17.15.3.4", {"position": v(248.27, -335.2) * mm});
            skPoint(sketch, "E17.15.3.5", {"position": v(238.27, -285.2) * mm});
            skLineSegment(sketch, "E17.15.3.6", {"start": v(240.27, -285.2) * mm, "end": v(246.27, -285.2) * mm});
            skLineSegment(sketch, "E17.15.3.7", {"start": v(240.27, -335.2) * mm, "end": v(246.27, -335.2) * mm});
            skPoint(sketch, "E17.15.3.8", {"position": v(248.27, -285.2) * mm});
            skArc(sketch, "E17.15.3.9", {"start": v(248.27, -287.2) * mm, "mid": v(247.68, -285.8) * mm, "end": v(246.27, -285.2) * mm});
            skArc(sketch, "E17.15.3.10", {"start": v(246.27, -335.2) * mm, "mid": v(247.68, -334.62) * mm, "end": v(248.27, -333.2) * mm});
            skArc(sketch, "E17.15.3.11", {"start": v(240.27, -285.2) * mm, "mid": v(238.85, -285.8) * mm, "end": v(238.27, -287.2) * mm});
            skLineSegment(sketch, "E17.15.4.0", {"start": v(248.27, -273.2) * mm, "end": v(248.27, -227.2) * mm});
            skPoint(sketch, "E17.15.4.1", {"position": v(238.27, -275.2) * mm});
            skLineSegment(sketch, "E17.15.4.2", {"start": v(238.27, -273.2) * mm, "end": v(238.27, -227.2) * mm});
            skArc(sketch, "E17.15.4.3", {"start": v(238.27, -273.2) * mm, "mid": v(238.85, -274.62) * mm, "end": v(240.27, -275.2) * mm});
            skPoint(sketch, "E17.15.4.4", {"position": v(248.27, -275.2) * mm});
            skPoint(sketch, "E17.15.4.5", {"position": v(238.27, -225.2) * mm});
            skLineSegment(sketch, "E17.15.4.6", {"start": v(240.27, -225.2) * mm, "end": v(246.27, -225.2) * mm});
            skLineSegment(sketch, "E17.15.4.7", {"start": v(240.27, -275.2) * mm, "end": v(246.27, -275.2) * mm});
            skPoint(sketch, "E17.15.4.8", {"position": v(248.27, -225.2) * mm});
            skArc(sketch, "E17.15.4.9", {"start": v(248.27, -227.2) * mm, "mid": v(247.68, -225.8) * mm, "end": v(246.27, -225.2) * mm});
            skArc(sketch, "E17.15.4.10", {"start": v(246.27, -275.2) * mm, "mid": v(247.68, -274.62) * mm, "end": v(248.27, -273.2) * mm});
            skArc(sketch, "E17.15.4.11", {"start": v(240.27, -225.2) * mm, "mid": v(238.85, -225.8) * mm, "end": v(238.27, -227.2) * mm});
            skLineSegment(sketch, "E17.16.0.0", {"start": v(263.77, -513.2) * mm, "end": v(263.77, -467.2) * mm});
            skPoint(sketch, "E17.16.0.1", {"position": v(253.77, -515.2) * mm});
            skLineSegment(sketch, "E17.16.0.2", {"start": v(253.77, -513.2) * mm, "end": v(253.77, -467.2) * mm});
            skArc(sketch, "E17.16.0.3", {"start": v(253.77, -513.2) * mm, "mid": v(254.35, -514.62) * mm, "end": v(255.77, -515.2) * mm});
            skPoint(sketch, "E17.16.0.4", {"position": v(263.77, -515.2) * mm});
            skPoint(sketch, "E17.16.0.5", {"position": v(253.77, -465.2) * mm});
            skLineSegment(sketch, "E17.16.0.6", {"start": v(255.77, -465.2) * mm, "end": v(261.77, -465.2) * mm});
            skLineSegment(sketch, "E17.16.0.7", {"start": v(255.77, -515.2) * mm, "end": v(261.77, -515.2) * mm});
            skPoint(sketch, "E17.16.0.8", {"position": v(263.77, -465.2) * mm});
            skArc(sketch, "E17.16.0.9", {"start": v(263.77, -467.2) * mm, "mid": v(263.18, -465.8) * mm, "end": v(261.77, -465.2) * mm});
            skArc(sketch, "E17.16.0.10", {"start": v(261.77, -515.2) * mm, "mid": v(263.18, -514.62) * mm, "end": v(263.77, -513.2) * mm});
            skArc(sketch, "E17.16.0.11", {"start": v(255.77, -465.2) * mm, "mid": v(254.35, -465.8) * mm, "end": v(253.77, -467.2) * mm});
            skLineSegment(sketch, "E17.16.1.0", {"start": v(263.77, -453.2) * mm, "end": v(263.77, -407.2) * mm});
            skPoint(sketch, "E17.16.1.1", {"position": v(253.77, -455.2) * mm});
            skLineSegment(sketch, "E17.16.1.2", {"start": v(253.77, -453.2) * mm, "end": v(253.77, -407.2) * mm});
            skArc(sketch, "E17.16.1.3", {"start": v(253.77, -453.2) * mm, "mid": v(254.35, -454.62) * mm, "end": v(255.77, -455.2) * mm});
            skPoint(sketch, "E17.16.1.4", {"position": v(263.77, -455.2) * mm});
            skPoint(sketch, "E17.16.1.5", {"position": v(253.77, -405.2) * mm});
            skLineSegment(sketch, "E17.16.1.6", {"start": v(255.77, -405.2) * mm, "end": v(261.77, -405.2) * mm});
            skLineSegment(sketch, "E17.16.1.7", {"start": v(255.77, -455.2) * mm, "end": v(261.77, -455.2) * mm});
            skPoint(sketch, "E17.16.1.8", {"position": v(263.77, -405.2) * mm});
            skArc(sketch, "E17.16.1.9", {"start": v(263.77, -407.2) * mm, "mid": v(263.18, -405.8) * mm, "end": v(261.77, -405.2) * mm});
            skArc(sketch, "E17.16.1.10", {"start": v(261.77, -455.2) * mm, "mid": v(263.18, -454.62) * mm, "end": v(263.77, -453.2) * mm});
            skArc(sketch, "E17.16.1.11", {"start": v(255.77, -405.2) * mm, "mid": v(254.35, -405.8) * mm, "end": v(253.77, -407.2) * mm});
            skLineSegment(sketch, "E17.16.2.0", {"start": v(263.77, -393.2) * mm, "end": v(263.77, -347.2) * mm});
            skPoint(sketch, "E17.16.2.1", {"position": v(253.77, -395.2) * mm});
            skLineSegment(sketch, "E17.16.2.2", {"start": v(253.77, -393.2) * mm, "end": v(253.77, -347.2) * mm});
            skArc(sketch, "E17.16.2.3", {"start": v(253.77, -393.2) * mm, "mid": v(254.35, -394.62) * mm, "end": v(255.77, -395.2) * mm});
            skPoint(sketch, "E17.16.2.4", {"position": v(263.77, -395.2) * mm});
            skPoint(sketch, "E17.16.2.5", {"position": v(253.77, -345.2) * mm});
            skLineSegment(sketch, "E17.16.2.6", {"start": v(255.77, -345.2) * mm, "end": v(261.77, -345.2) * mm});
            skLineSegment(sketch, "E17.16.2.7", {"start": v(255.77, -395.2) * mm, "end": v(261.77, -395.2) * mm});
            skPoint(sketch, "E17.16.2.8", {"position": v(263.77, -345.2) * mm});
            skArc(sketch, "E17.16.2.9", {"start": v(263.77, -347.2) * mm, "mid": v(263.18, -345.8) * mm, "end": v(261.77, -345.2) * mm});
            skArc(sketch, "E17.16.2.10", {"start": v(261.77, -395.2) * mm, "mid": v(263.18, -394.62) * mm, "end": v(263.77, -393.2) * mm});
            skArc(sketch, "E17.16.2.11", {"start": v(255.77, -345.2) * mm, "mid": v(254.35, -345.8) * mm, "end": v(253.77, -347.2) * mm});
            skLineSegment(sketch, "E17.16.3.0", {"start": v(263.77, -333.2) * mm, "end": v(263.77, -287.2) * mm});
            skPoint(sketch, "E17.16.3.1", {"position": v(253.77, -335.2) * mm});
            skLineSegment(sketch, "E17.16.3.2", {"start": v(253.77, -333.2) * mm, "end": v(253.77, -287.2) * mm});
            skArc(sketch, "E17.16.3.3", {"start": v(253.77, -333.2) * mm, "mid": v(254.35, -334.62) * mm, "end": v(255.77, -335.2) * mm});
            skPoint(sketch, "E17.16.3.4", {"position": v(263.77, -335.2) * mm});
            skPoint(sketch, "E17.16.3.5", {"position": v(253.77, -285.2) * mm});
            skLineSegment(sketch, "E17.16.3.6", {"start": v(255.77, -285.2) * mm, "end": v(261.77, -285.2) * mm});
            skLineSegment(sketch, "E17.16.3.7", {"start": v(255.77, -335.2) * mm, "end": v(261.77, -335.2) * mm});
            skPoint(sketch, "E17.16.3.8", {"position": v(263.77, -285.2) * mm});
            skArc(sketch, "E17.16.3.9", {"start": v(263.77, -287.2) * mm, "mid": v(263.18, -285.8) * mm, "end": v(261.77, -285.2) * mm});
            skArc(sketch, "E17.16.3.10", {"start": v(261.77, -335.2) * mm, "mid": v(263.18, -334.62) * mm, "end": v(263.77, -333.2) * mm});
            skArc(sketch, "E17.16.3.11", {"start": v(255.77, -285.2) * mm, "mid": v(254.35, -285.8) * mm, "end": v(253.77, -287.2) * mm});
            skLineSegment(sketch, "E17.16.4.0", {"start": v(263.77, -273.2) * mm, "end": v(263.77, -227.2) * mm});
            skPoint(sketch, "E17.16.4.1", {"position": v(253.77, -275.2) * mm});
            skLineSegment(sketch, "E17.16.4.2", {"start": v(253.77, -273.2) * mm, "end": v(253.77, -227.2) * mm});
            skArc(sketch, "E17.16.4.3", {"start": v(253.77, -273.2) * mm, "mid": v(254.35, -274.62) * mm, "end": v(255.77, -275.2) * mm});
            skPoint(sketch, "E17.16.4.4", {"position": v(263.77, -275.2) * mm});
            skPoint(sketch, "E17.16.4.5", {"position": v(253.77, -225.2) * mm});
            skLineSegment(sketch, "E17.16.4.6", {"start": v(255.77, -225.2) * mm, "end": v(261.77, -225.2) * mm});
            skLineSegment(sketch, "E17.16.4.7", {"start": v(255.77, -275.2) * mm, "end": v(261.77, -275.2) * mm});
            skPoint(sketch, "E17.16.4.8", {"position": v(263.77, -225.2) * mm});
            skArc(sketch, "E17.16.4.9", {"start": v(263.77, -227.2) * mm, "mid": v(263.18, -225.8) * mm, "end": v(261.77, -225.2) * mm});
            skArc(sketch, "E17.16.4.10", {"start": v(261.77, -275.2) * mm, "mid": v(263.18, -274.62) * mm, "end": v(263.77, -273.2) * mm});
            skArc(sketch, "E17.16.4.11", {"start": v(255.77, -225.2) * mm, "mid": v(254.35, -225.8) * mm, "end": v(253.77, -227.2) * mm});
            skLineSegment(sketch, "E17.17.0.0", {"start": v(279.27, -513.2) * mm, "end": v(279.27, -467.2) * mm});
            skPoint(sketch, "E17.17.0.1", {"position": v(269.27, -515.2) * mm});
            skLineSegment(sketch, "E17.17.0.2", {"start": v(269.27, -513.2) * mm, "end": v(269.27, -467.2) * mm});
            skArc(sketch, "E17.17.0.3", {"start": v(269.27, -513.2) * mm, "mid": v(269.85, -514.62) * mm, "end": v(271.27, -515.2) * mm});
            skPoint(sketch, "E17.17.0.4", {"position": v(279.27, -515.2) * mm});
            skPoint(sketch, "E17.17.0.5", {"position": v(269.27, -465.2) * mm});
            skLineSegment(sketch, "E17.17.0.6", {"start": v(271.27, -465.2) * mm, "end": v(277.27, -465.2) * mm});
            skLineSegment(sketch, "E17.17.0.7", {"start": v(271.27, -515.2) * mm, "end": v(277.27, -515.2) * mm});
            skPoint(sketch, "E17.17.0.8", {"position": v(279.27, -465.2) * mm});
            skArc(sketch, "E17.17.0.9", {"start": v(279.27, -467.2) * mm, "mid": v(278.68, -465.8) * mm, "end": v(277.27, -465.2) * mm});
            skArc(sketch, "E17.17.0.10", {"start": v(277.27, -515.2) * mm, "mid": v(278.68, -514.62) * mm, "end": v(279.27, -513.2) * mm});
            skArc(sketch, "E17.17.0.11", {"start": v(271.27, -465.2) * mm, "mid": v(269.85, -465.8) * mm, "end": v(269.27, -467.2) * mm});
            skLineSegment(sketch, "E17.17.1.0", {"start": v(279.27, -453.2) * mm, "end": v(279.27, -407.2) * mm});
            skPoint(sketch, "E17.17.1.1", {"position": v(269.27, -455.2) * mm});
            skLineSegment(sketch, "E17.17.1.2", {"start": v(269.27, -453.2) * mm, "end": v(269.27, -407.2) * mm});
            skArc(sketch, "E17.17.1.3", {"start": v(269.27, -453.2) * mm, "mid": v(269.85, -454.62) * mm, "end": v(271.27, -455.2) * mm});
            skPoint(sketch, "E17.17.1.4", {"position": v(279.27, -455.2) * mm});
            skPoint(sketch, "E17.17.1.5", {"position": v(269.27, -405.2) * mm});
            skLineSegment(sketch, "E17.17.1.6", {"start": v(271.27, -405.2) * mm, "end": v(277.27, -405.2) * mm});
            skLineSegment(sketch, "E17.17.1.7", {"start": v(271.27, -455.2) * mm, "end": v(277.27, -455.2) * mm});
            skPoint(sketch, "E17.17.1.8", {"position": v(279.27, -405.2) * mm});
            skArc(sketch, "E17.17.1.9", {"start": v(279.27, -407.2) * mm, "mid": v(278.68, -405.8) * mm, "end": v(277.27, -405.2) * mm});
            skArc(sketch, "E17.17.1.10", {"start": v(277.27, -455.2) * mm, "mid": v(278.68, -454.62) * mm, "end": v(279.27, -453.2) * mm});
            skArc(sketch, "E17.17.1.11", {"start": v(271.27, -405.2) * mm, "mid": v(269.85, -405.8) * mm, "end": v(269.27, -407.2) * mm});
            skLineSegment(sketch, "E17.17.2.0", {"start": v(279.27, -393.2) * mm, "end": v(279.27, -347.2) * mm});
            skPoint(sketch, "E17.17.2.1", {"position": v(269.27, -395.2) * mm});
            skLineSegment(sketch, "E17.17.2.2", {"start": v(269.27, -393.2) * mm, "end": v(269.27, -347.2) * mm});
            skArc(sketch, "E17.17.2.3", {"start": v(269.27, -393.2) * mm, "mid": v(269.85, -394.62) * mm, "end": v(271.27, -395.2) * mm});
            skPoint(sketch, "E17.17.2.4", {"position": v(279.27, -395.2) * mm});
            skPoint(sketch, "E17.17.2.5", {"position": v(269.27, -345.2) * mm});
            skLineSegment(sketch, "E17.17.2.6", {"start": v(271.27, -345.2) * mm, "end": v(277.27, -345.2) * mm});
            skLineSegment(sketch, "E17.17.2.7", {"start": v(271.27, -395.2) * mm, "end": v(277.27, -395.2) * mm});
            skPoint(sketch, "E17.17.2.8", {"position": v(279.27, -345.2) * mm});
            skArc(sketch, "E17.17.2.9", {"start": v(279.27, -347.2) * mm, "mid": v(278.68, -345.8) * mm, "end": v(277.27, -345.2) * mm});
            skArc(sketch, "E17.17.2.10", {"start": v(277.27, -395.2) * mm, "mid": v(278.68, -394.62) * mm, "end": v(279.27, -393.2) * mm});
            skArc(sketch, "E17.17.2.11", {"start": v(271.27, -345.2) * mm, "mid": v(269.85, -345.8) * mm, "end": v(269.27, -347.2) * mm});
            skLineSegment(sketch, "E17.17.3.0", {"start": v(279.27, -333.2) * mm, "end": v(279.27, -287.2) * mm});
            skPoint(sketch, "E17.17.3.1", {"position": v(269.27, -335.2) * mm});
            skLineSegment(sketch, "E17.17.3.2", {"start": v(269.27, -333.2) * mm, "end": v(269.27, -287.2) * mm});
            skArc(sketch, "E17.17.3.3", {"start": v(269.27, -333.2) * mm, "mid": v(269.85, -334.62) * mm, "end": v(271.27, -335.2) * mm});
            skPoint(sketch, "E17.17.3.4", {"position": v(279.27, -335.2) * mm});
            skPoint(sketch, "E17.17.3.5", {"position": v(269.27, -285.2) * mm});
            skLineSegment(sketch, "E17.17.3.6", {"start": v(271.27, -285.2) * mm, "end": v(277.27, -285.2) * mm});
            skLineSegment(sketch, "E17.17.3.7", {"start": v(271.27, -335.2) * mm, "end": v(277.27, -335.2) * mm});
            skPoint(sketch, "E17.17.3.8", {"position": v(279.27, -285.2) * mm});
            skArc(sketch, "E17.17.3.9", {"start": v(279.27, -287.2) * mm, "mid": v(278.68, -285.8) * mm, "end": v(277.27, -285.2) * mm});
            skArc(sketch, "E17.17.3.10", {"start": v(277.27, -335.2) * mm, "mid": v(278.68, -334.62) * mm, "end": v(279.27, -333.2) * mm});
            skArc(sketch, "E17.17.3.11", {"start": v(271.27, -285.2) * mm, "mid": v(269.85, -285.8) * mm, "end": v(269.27, -287.2) * mm});
            skLineSegment(sketch, "E17.17.4.0", {"start": v(279.27, -273.2) * mm, "end": v(279.27, -227.2) * mm});
            skPoint(sketch, "E17.17.4.1", {"position": v(269.27, -275.2) * mm});
            skLineSegment(sketch, "E17.17.4.2", {"start": v(269.27, -273.2) * mm, "end": v(269.27, -227.2) * mm});
            skArc(sketch, "E17.17.4.3", {"start": v(269.27, -273.2) * mm, "mid": v(269.85, -274.62) * mm, "end": v(271.27, -275.2) * mm});
            skPoint(sketch, "E17.17.4.4", {"position": v(279.27, -275.2) * mm});
            skPoint(sketch, "E17.17.4.5", {"position": v(269.27, -225.2) * mm});
            skLineSegment(sketch, "E17.17.4.6", {"start": v(271.27, -225.2) * mm, "end": v(277.27, -225.2) * mm});
            skLineSegment(sketch, "E17.17.4.7", {"start": v(271.27, -275.2) * mm, "end": v(277.27, -275.2) * mm});
            skPoint(sketch, "E17.17.4.8", {"position": v(279.27, -225.2) * mm});
            skArc(sketch, "E17.17.4.9", {"start": v(279.27, -227.2) * mm, "mid": v(278.68, -225.8) * mm, "end": v(277.27, -225.2) * mm});
            skArc(sketch, "E17.17.4.10", {"start": v(277.27, -275.2) * mm, "mid": v(278.68, -274.62) * mm, "end": v(279.27, -273.2) * mm});
            skArc(sketch, "E17.17.4.11", {"start": v(271.27, -225.2) * mm, "mid": v(269.85, -225.8) * mm, "end": v(269.27, -227.2) * mm});
            skLineSegment(sketch, "E17.18.0.0", {"start": v(294.77, -513.2) * mm, "end": v(294.77, -467.2) * mm});
            skPoint(sketch, "E17.18.0.1", {"position": v(284.77, -515.2) * mm});
            skLineSegment(sketch, "E17.18.0.2", {"start": v(284.77, -513.2) * mm, "end": v(284.77, -467.2) * mm});
            skArc(sketch, "E17.18.0.3", {"start": v(284.77, -513.2) * mm, "mid": v(285.35, -514.62) * mm, "end": v(286.77, -515.2) * mm});
            skPoint(sketch, "E17.18.0.4", {"position": v(294.77, -515.2) * mm});
            skPoint(sketch, "E17.18.0.5", {"position": v(284.77, -465.2) * mm});
            skLineSegment(sketch, "E17.18.0.6", {"start": v(286.77, -465.2) * mm, "end": v(292.77, -465.2) * mm});
            skLineSegment(sketch, "E17.18.0.7", {"start": v(286.77, -515.2) * mm, "end": v(292.77, -515.2) * mm});
            skPoint(sketch, "E17.18.0.8", {"position": v(294.77, -465.2) * mm});
            skArc(sketch, "E17.18.0.9", {"start": v(294.77, -467.2) * mm, "mid": v(294.18, -465.8) * mm, "end": v(292.77, -465.2) * mm});
            skArc(sketch, "E17.18.0.10", {"start": v(292.77, -515.2) * mm, "mid": v(294.18, -514.62) * mm, "end": v(294.77, -513.2) * mm});
            skArc(sketch, "E17.18.0.11", {"start": v(286.77, -465.2) * mm, "mid": v(285.35, -465.8) * mm, "end": v(284.77, -467.2) * mm});
            skLineSegment(sketch, "E17.18.1.0", {"start": v(294.77, -453.2) * mm, "end": v(294.77, -407.2) * mm});
            skPoint(sketch, "E17.18.1.1", {"position": v(284.77, -455.2) * mm});
            skLineSegment(sketch, "E17.18.1.2", {"start": v(284.77, -453.2) * mm, "end": v(284.77, -407.2) * mm});
            skArc(sketch, "E17.18.1.3", {"start": v(284.77, -453.2) * mm, "mid": v(285.35, -454.62) * mm, "end": v(286.77, -455.2) * mm});
            skPoint(sketch, "E17.18.1.4", {"position": v(294.77, -455.2) * mm});
            skPoint(sketch, "E17.18.1.5", {"position": v(284.77, -405.2) * mm});
            skLineSegment(sketch, "E17.18.1.6", {"start": v(286.77, -405.2) * mm, "end": v(292.77, -405.2) * mm});
            skLineSegment(sketch, "E17.18.1.7", {"start": v(286.77, -455.2) * mm, "end": v(292.77, -455.2) * mm});
            skPoint(sketch, "E17.18.1.8", {"position": v(294.77, -405.2) * mm});
            skArc(sketch, "E17.18.1.9", {"start": v(294.77, -407.2) * mm, "mid": v(294.18, -405.8) * mm, "end": v(292.77, -405.2) * mm});
            skArc(sketch, "E17.18.1.10", {"start": v(292.77, -455.2) * mm, "mid": v(294.18, -454.62) * mm, "end": v(294.77, -453.2) * mm});
            skArc(sketch, "E17.18.1.11", {"start": v(286.77, -405.2) * mm, "mid": v(285.35, -405.8) * mm, "end": v(284.77, -407.2) * mm});
            skLineSegment(sketch, "E17.18.2.0", {"start": v(294.77, -393.2) * mm, "end": v(294.77, -347.2) * mm});
            skPoint(sketch, "E17.18.2.1", {"position": v(284.77, -395.2) * mm});
            skLineSegment(sketch, "E17.18.2.2", {"start": v(284.77, -393.2) * mm, "end": v(284.77, -347.2) * mm});
            skArc(sketch, "E17.18.2.3", {"start": v(284.77, -393.2) * mm, "mid": v(285.35, -394.62) * mm, "end": v(286.77, -395.2) * mm});
            skPoint(sketch, "E17.18.2.4", {"position": v(294.77, -395.2) * mm});
            skPoint(sketch, "E17.18.2.5", {"position": v(284.77, -345.2) * mm});
            skLineSegment(sketch, "E17.18.2.6", {"start": v(286.77, -345.2) * mm, "end": v(292.77, -345.2) * mm});
            skLineSegment(sketch, "E17.18.2.7", {"start": v(286.77, -395.2) * mm, "end": v(292.77, -395.2) * mm});
            skPoint(sketch, "E17.18.2.8", {"position": v(294.77, -345.2) * mm});
            skArc(sketch, "E17.18.2.9", {"start": v(294.77, -347.2) * mm, "mid": v(294.18, -345.8) * mm, "end": v(292.77, -345.2) * mm});
            skArc(sketch, "E17.18.2.10", {"start": v(292.77, -395.2) * mm, "mid": v(294.18, -394.62) * mm, "end": v(294.77, -393.2) * mm});
            skArc(sketch, "E17.18.2.11", {"start": v(286.77, -345.2) * mm, "mid": v(285.35, -345.8) * mm, "end": v(284.77, -347.2) * mm});
            skLineSegment(sketch, "E17.18.3.0", {"start": v(294.77, -333.2) * mm, "end": v(294.77, -287.2) * mm});
            skPoint(sketch, "E17.18.3.1", {"position": v(284.77, -335.2) * mm});
            skLineSegment(sketch, "E17.18.3.2", {"start": v(284.77, -333.2) * mm, "end": v(284.77, -287.2) * mm});
            skArc(sketch, "E17.18.3.3", {"start": v(284.77, -333.2) * mm, "mid": v(285.35, -334.62) * mm, "end": v(286.77, -335.2) * mm});
            skPoint(sketch, "E17.18.3.4", {"position": v(294.77, -335.2) * mm});
            skPoint(sketch, "E17.18.3.5", {"position": v(284.77, -285.2) * mm});
            skLineSegment(sketch, "E17.18.3.6", {"start": v(286.77, -285.2) * mm, "end": v(292.77, -285.2) * mm});
            skLineSegment(sketch, "E17.18.3.7", {"start": v(286.77, -335.2) * mm, "end": v(292.77, -335.2) * mm});
            skPoint(sketch, "E17.18.3.8", {"position": v(294.77, -285.2) * mm});
            skArc(sketch, "E17.18.3.9", {"start": v(294.77, -287.2) * mm, "mid": v(294.18, -285.8) * mm, "end": v(292.77, -285.2) * mm});
            skArc(sketch, "E17.18.3.10", {"start": v(292.77, -335.2) * mm, "mid": v(294.18, -334.62) * mm, "end": v(294.77, -333.2) * mm});
            skArc(sketch, "E17.18.3.11", {"start": v(286.77, -285.2) * mm, "mid": v(285.35, -285.8) * mm, "end": v(284.77, -287.2) * mm});
            skLineSegment(sketch, "E17.18.4.0", {"start": v(294.77, -273.2) * mm, "end": v(294.77, -227.2) * mm});
            skPoint(sketch, "E17.18.4.1", {"position": v(284.77, -275.2) * mm});
            skLineSegment(sketch, "E17.18.4.2", {"start": v(284.77, -273.2) * mm, "end": v(284.77, -227.2) * mm});
            skArc(sketch, "E17.18.4.3", {"start": v(284.77, -273.2) * mm, "mid": v(285.35, -274.62) * mm, "end": v(286.77, -275.2) * mm});
            skPoint(sketch, "E17.18.4.4", {"position": v(294.77, -275.2) * mm});
            skPoint(sketch, "E17.18.4.5", {"position": v(284.77, -225.2) * mm});
            skLineSegment(sketch, "E17.18.4.6", {"start": v(286.77, -225.2) * mm, "end": v(292.77, -225.2) * mm});
            skLineSegment(sketch, "E17.18.4.7", {"start": v(286.77, -275.2) * mm, "end": v(292.77, -275.2) * mm});
            skPoint(sketch, "E17.18.4.8", {"position": v(294.77, -225.2) * mm});
            skArc(sketch, "E17.18.4.9", {"start": v(294.77, -227.2) * mm, "mid": v(294.18, -225.8) * mm, "end": v(292.77, -225.2) * mm});
            skArc(sketch, "E17.18.4.10", {"start": v(292.77, -275.2) * mm, "mid": v(294.18, -274.62) * mm, "end": v(294.77, -273.2) * mm});
            skArc(sketch, "E17.18.4.11", {"start": v(286.77, -225.2) * mm, "mid": v(285.35, -225.8) * mm, "end": v(284.77, -227.2) * mm});
            skLineSegment(sketch, "E17.direction1", {"start": v(5.77, -515.2) * mm, "end": v(21.27, -515.2) * mm, "construction": true});
            skLineSegment(sketch, "E17.direction2", {"start": v(5.77, -515.2) * mm, "end": v(5.77, -455.2) * mm, "construction": true});
            skLineSegment(sketch, "E18.0.0.5", {"start": v(15.77, -213.2) * mm, "end": v(15.77, -167.2) * mm});
            skPoint(sketch, "E18.3.0.5", {"position": v(5.77, -215.2) * mm});
            skLineSegment(sketch, "E18.4.0.5", {"start": v(5.77, -213.2) * mm, "end": v(5.77, -167.2) * mm});
            skArc(sketch, "E18.7.0.5", {"start": v(5.77, -213.2) * mm, "mid": v(6.35, -214.62) * mm, "end": v(7.77, -215.2) * mm});
            skPoint(sketch, "E18.11.0.5", {"position": v(15.77, -215.2) * mm});
            skPoint(sketch, "E18.12.0.5", {"position": v(5.77, -165.2) * mm});
            skLineSegment(sketch, "E18.13.0.5", {"start": v(7.77, -165.2) * mm, "end": v(13.77, -165.2) * mm});
            skLineSegment(sketch, "E18.16.0.5", {"start": v(7.77, -215.2) * mm, "end": v(13.77, -215.2) * mm});
            skPoint(sketch, "E18.19.0.5", {"position": v(15.77, -165.2) * mm});
            skArc(sketch, "E18.20.0.5", {"start": v(15.77, -167.2) * mm, "mid": v(15.18, -165.8) * mm, "end": v(13.77, -165.2) * mm});
            skArc(sketch, "E18.24.0.5", {"start": v(13.77, -215.2) * mm, "mid": v(15.18, -214.62) * mm, "end": v(15.77, -213.2) * mm});
            skArc(sketch, "E18.28.0.5", {"start": v(7.77, -165.2) * mm, "mid": v(6.35, -165.8) * mm, "end": v(5.77, -167.2) * mm});
            skLineSegment(sketch, "E18.0.1.5", {"start": v(31.27, -213.2) * mm, "end": v(31.27, -167.2) * mm});
            skPoint(sketch, "E18.3.1.5", {"position": v(21.27, -215.2) * mm});
            skLineSegment(sketch, "E18.4.1.5", {"start": v(21.27, -213.2) * mm, "end": v(21.27, -167.2) * mm});
            skArc(sketch, "E18.7.1.5", {"start": v(21.27, -213.2) * mm, "mid": v(21.85, -214.62) * mm, "end": v(23.27, -215.2) * mm});
            skPoint(sketch, "E18.11.1.5", {"position": v(31.27, -215.2) * mm});
            skPoint(sketch, "E18.12.1.5", {"position": v(21.27, -165.2) * mm});
            skLineSegment(sketch, "E18.13.1.5", {"start": v(23.27, -165.2) * mm, "end": v(29.27, -165.2) * mm});
            skLineSegment(sketch, "E18.16.1.5", {"start": v(23.27, -215.2) * mm, "end": v(29.27, -215.2) * mm});
            skPoint(sketch, "E18.19.1.5", {"position": v(31.27, -165.2) * mm});
            skArc(sketch, "E18.20.1.5", {"start": v(31.27, -167.2) * mm, "mid": v(30.68, -165.8) * mm, "end": v(29.27, -165.2) * mm});
            skArc(sketch, "E18.24.1.5", {"start": v(29.27, -215.2) * mm, "mid": v(30.68, -214.62) * mm, "end": v(31.27, -213.2) * mm});
            skArc(sketch, "E18.28.1.5", {"start": v(23.27, -165.2) * mm, "mid": v(21.85, -165.8) * mm, "end": v(21.27, -167.2) * mm});
            skLineSegment(sketch, "E18.0.2.5", {"start": v(46.77, -213.2) * mm, "end": v(46.77, -167.2) * mm});
            skPoint(sketch, "E18.3.2.5", {"position": v(36.77, -215.2) * mm});
            skLineSegment(sketch, "E18.4.2.5", {"start": v(36.77, -213.2) * mm, "end": v(36.77, -167.2) * mm});
            skArc(sketch, "E18.7.2.5", {"start": v(36.77, -213.2) * mm, "mid": v(37.35, -214.62) * mm, "end": v(38.77, -215.2) * mm});
            skPoint(sketch, "E18.11.2.5", {"position": v(46.77, -215.2) * mm});
            skPoint(sketch, "E18.12.2.5", {"position": v(36.77, -165.2) * mm});
            skLineSegment(sketch, "E18.13.2.5", {"start": v(38.77, -165.2) * mm, "end": v(44.77, -165.2) * mm});
            skLineSegment(sketch, "E18.16.2.5", {"start": v(38.77, -215.2) * mm, "end": v(44.77, -215.2) * mm});
            skPoint(sketch, "E18.19.2.5", {"position": v(46.77, -165.2) * mm});
            skArc(sketch, "E18.20.2.5", {"start": v(46.77, -167.2) * mm, "mid": v(46.18, -165.8) * mm, "end": v(44.77, -165.2) * mm});
            skArc(sketch, "E18.24.2.5", {"start": v(44.77, -215.2) * mm, "mid": v(46.18, -214.62) * mm, "end": v(46.77, -213.2) * mm});
            skArc(sketch, "E18.28.2.5", {"start": v(38.77, -165.2) * mm, "mid": v(37.35, -165.8) * mm, "end": v(36.77, -167.2) * mm});
            skLineSegment(sketch, "E18.0.3.5", {"start": v(62.27, -213.2) * mm, "end": v(62.27, -167.2) * mm});
            skPoint(sketch, "E18.3.3.5", {"position": v(52.27, -215.2) * mm});
            skLineSegment(sketch, "E18.4.3.5", {"start": v(52.27, -213.2) * mm, "end": v(52.27, -167.2) * mm});
            skArc(sketch, "E18.7.3.5", {"start": v(52.27, -213.2) * mm, "mid": v(52.85, -214.62) * mm, "end": v(54.27, -215.2) * mm});
            skPoint(sketch, "E18.11.3.5", {"position": v(62.27, -215.2) * mm});
            skPoint(sketch, "E18.12.3.5", {"position": v(52.27, -165.2) * mm});
            skLineSegment(sketch, "E18.13.3.5", {"start": v(54.27, -165.2) * mm, "end": v(60.27, -165.2) * mm});
            skLineSegment(sketch, "E18.16.3.5", {"start": v(54.27, -215.2) * mm, "end": v(60.27, -215.2) * mm});
            skPoint(sketch, "E18.19.3.5", {"position": v(62.27, -165.2) * mm});
            skArc(sketch, "E18.20.3.5", {"start": v(62.27, -167.2) * mm, "mid": v(61.68, -165.8) * mm, "end": v(60.27, -165.2) * mm});
            skArc(sketch, "E18.24.3.5", {"start": v(60.27, -215.2) * mm, "mid": v(61.68, -214.62) * mm, "end": v(62.27, -213.2) * mm});
            skArc(sketch, "E18.28.3.5", {"start": v(54.27, -165.2) * mm, "mid": v(52.85, -165.8) * mm, "end": v(52.27, -167.2) * mm});
            skLineSegment(sketch, "E18.0.4.5", {"start": v(77.77, -213.2) * mm, "end": v(77.77, -167.2) * mm});
            skPoint(sketch, "E18.3.4.5", {"position": v(67.77, -215.2) * mm});
            skLineSegment(sketch, "E18.4.4.5", {"start": v(67.77, -213.2) * mm, "end": v(67.77, -167.2) * mm});
            skArc(sketch, "E18.7.4.5", {"start": v(67.77, -213.2) * mm, "mid": v(68.35, -214.62) * mm, "end": v(69.77, -215.2) * mm});
            skPoint(sketch, "E18.11.4.5", {"position": v(77.77, -215.2) * mm});
            skPoint(sketch, "E18.12.4.5", {"position": v(67.77, -165.2) * mm});
            skLineSegment(sketch, "E18.13.4.5", {"start": v(69.77, -165.2) * mm, "end": v(75.77, -165.2) * mm});
            skLineSegment(sketch, "E18.16.4.5", {"start": v(69.77, -215.2) * mm, "end": v(75.77, -215.2) * mm});
            skPoint(sketch, "E18.19.4.5", {"position": v(77.77, -165.2) * mm});
            skArc(sketch, "E18.20.4.5", {"start": v(77.77, -167.2) * mm, "mid": v(77.18, -165.8) * mm, "end": v(75.77, -165.2) * mm});
            skArc(sketch, "E18.24.4.5", {"start": v(75.77, -215.2) * mm, "mid": v(77.18, -214.62) * mm, "end": v(77.77, -213.2) * mm});
            skArc(sketch, "E18.28.4.5", {"start": v(69.77, -165.2) * mm, "mid": v(68.35, -165.8) * mm, "end": v(67.77, -167.2) * mm});
            skLineSegment(sketch, "E18.0.5.5", {"start": v(93.27, -213.2) * mm, "end": v(93.27, -167.2) * mm});
            skPoint(sketch, "E18.3.5.5", {"position": v(83.27, -215.2) * mm});
            skLineSegment(sketch, "E18.4.5.5", {"start": v(83.27, -213.2) * mm, "end": v(83.27, -167.2) * mm});
            skArc(sketch, "E18.7.5.5", {"start": v(83.27, -213.2) * mm, "mid": v(83.85, -214.62) * mm, "end": v(85.27, -215.2) * mm});
            skPoint(sketch, "E18.11.5.5", {"position": v(93.27, -215.2) * mm});
            skPoint(sketch, "E18.12.5.5", {"position": v(83.27, -165.2) * mm});
            skLineSegment(sketch, "E18.13.5.5", {"start": v(85.27, -165.2) * mm, "end": v(91.27, -165.2) * mm});
            skLineSegment(sketch, "E18.16.5.5", {"start": v(85.27, -215.2) * mm, "end": v(91.27, -215.2) * mm});
            skPoint(sketch, "E18.19.5.5", {"position": v(93.27, -165.2) * mm});
            skArc(sketch, "E18.20.5.5", {"start": v(93.27, -167.2) * mm, "mid": v(92.68, -165.8) * mm, "end": v(91.27, -165.2) * mm});
            skArc(sketch, "E18.24.5.5", {"start": v(91.27, -215.2) * mm, "mid": v(92.68, -214.62) * mm, "end": v(93.27, -213.2) * mm});
            skArc(sketch, "E18.28.5.5", {"start": v(85.27, -165.2) * mm, "mid": v(83.85, -165.8) * mm, "end": v(83.27, -167.2) * mm});
            skLineSegment(sketch, "E18.0.6.5", {"start": v(108.77, -213.2) * mm, "end": v(108.77, -167.2) * mm});
            skPoint(sketch, "E18.3.6.5", {"position": v(98.77, -215.2) * mm});
            skLineSegment(sketch, "E18.4.6.5", {"start": v(98.77, -213.2) * mm, "end": v(98.77, -167.2) * mm});
            skArc(sketch, "E18.7.6.5", {"start": v(98.77, -213.2) * mm, "mid": v(99.35, -214.62) * mm, "end": v(100.77, -215.2) * mm});
            skPoint(sketch, "E18.11.6.5", {"position": v(108.77, -215.2) * mm});
            skPoint(sketch, "E18.12.6.5", {"position": v(98.77, -165.2) * mm});
            skLineSegment(sketch, "E18.13.6.5", {"start": v(100.77, -165.2) * mm, "end": v(106.77, -165.2) * mm});
            skLineSegment(sketch, "E18.16.6.5", {"start": v(100.77, -215.2) * mm, "end": v(106.77, -215.2) * mm});
            skPoint(sketch, "E18.19.6.5", {"position": v(108.77, -165.2) * mm});
            skArc(sketch, "E18.20.6.5", {"start": v(108.77, -167.2) * mm, "mid": v(108.18, -165.8) * mm, "end": v(106.77, -165.2) * mm});
            skArc(sketch, "E18.24.6.5", {"start": v(106.77, -215.2) * mm, "mid": v(108.18, -214.62) * mm, "end": v(108.77, -213.2) * mm});
            skArc(sketch, "E18.28.6.5", {"start": v(100.77, -165.2) * mm, "mid": v(99.35, -165.8) * mm, "end": v(98.77, -167.2) * mm});
            skLineSegment(sketch, "E18.0.7.5", {"start": v(124.27, -213.2) * mm, "end": v(124.27, -167.2) * mm});
            skPoint(sketch, "E18.3.7.5", {"position": v(114.27, -215.2) * mm});
            skLineSegment(sketch, "E18.4.7.5", {"start": v(114.27, -213.2) * mm, "end": v(114.27, -167.2) * mm});
            skArc(sketch, "E18.7.7.5", {"start": v(114.27, -213.2) * mm, "mid": v(114.85, -214.62) * mm, "end": v(116.27, -215.2) * mm});
            skPoint(sketch, "E18.11.7.5", {"position": v(124.27, -215.2) * mm});
            skPoint(sketch, "E18.12.7.5", {"position": v(114.27, -165.2) * mm});
            skLineSegment(sketch, "E18.13.7.5", {"start": v(116.27, -165.2) * mm, "end": v(122.27, -165.2) * mm});
            skLineSegment(sketch, "E18.16.7.5", {"start": v(116.27, -215.2) * mm, "end": v(122.27, -215.2) * mm});
            skPoint(sketch, "E18.19.7.5", {"position": v(124.27, -165.2) * mm});
            skArc(sketch, "E18.20.7.5", {"start": v(124.27, -167.2) * mm, "mid": v(123.68, -165.8) * mm, "end": v(122.27, -165.2) * mm});
            skArc(sketch, "E18.24.7.5", {"start": v(122.27, -215.2) * mm, "mid": v(123.68, -214.62) * mm, "end": v(124.27, -213.2) * mm});
            skArc(sketch, "E18.28.7.5", {"start": v(116.27, -165.2) * mm, "mid": v(114.85, -165.8) * mm, "end": v(114.27, -167.2) * mm});
            skLineSegment(sketch, "E18.0.8.5", {"start": v(139.77, -213.2) * mm, "end": v(139.77, -167.2) * mm});
            skPoint(sketch, "E18.3.8.5", {"position": v(129.77, -215.2) * mm});
            skLineSegment(sketch, "E18.4.8.5", {"start": v(129.77, -213.2) * mm, "end": v(129.77, -167.2) * mm});
            skArc(sketch, "E18.7.8.5", {"start": v(129.77, -213.2) * mm, "mid": v(130.35, -214.62) * mm, "end": v(131.77, -215.2) * mm});
            skPoint(sketch, "E18.11.8.5", {"position": v(139.77, -215.2) * mm});
            skPoint(sketch, "E18.12.8.5", {"position": v(129.77, -165.2) * mm});
            skLineSegment(sketch, "E18.13.8.5", {"start": v(131.77, -165.2) * mm, "end": v(137.77, -165.2) * mm});
            skLineSegment(sketch, "E18.16.8.5", {"start": v(131.77, -215.2) * mm, "end": v(137.77, -215.2) * mm});
            skPoint(sketch, "E18.19.8.5", {"position": v(139.77, -165.2) * mm});
            skArc(sketch, "E18.20.8.5", {"start": v(139.77, -167.2) * mm, "mid": v(139.18, -165.8) * mm, "end": v(137.77, -165.2) * mm});
            skArc(sketch, "E18.24.8.5", {"start": v(137.77, -215.2) * mm, "mid": v(139.18, -214.62) * mm, "end": v(139.77, -213.2) * mm});
            skArc(sketch, "E18.28.8.5", {"start": v(131.77, -165.2) * mm, "mid": v(130.35, -165.8) * mm, "end": v(129.77, -167.2) * mm});
            skLineSegment(sketch, "E18.0.9.5", {"start": v(155.27, -213.2) * mm, "end": v(155.27, -167.2) * mm});
            skPoint(sketch, "E18.3.9.5", {"position": v(145.27, -215.2) * mm});
            skLineSegment(sketch, "E18.4.9.5", {"start": v(145.27, -213.2) * mm, "end": v(145.27, -167.2) * mm});
            skArc(sketch, "E18.7.9.5", {"start": v(145.27, -213.2) * mm, "mid": v(145.85, -214.62) * mm, "end": v(147.27, -215.2) * mm});
            skPoint(sketch, "E18.11.9.5", {"position": v(155.27, -215.2) * mm});
            skPoint(sketch, "E18.12.9.5", {"position": v(145.27, -165.2) * mm});
            skLineSegment(sketch, "E18.13.9.5", {"start": v(147.27, -165.2) * mm, "end": v(153.27, -165.2) * mm});
            skLineSegment(sketch, "E18.16.9.5", {"start": v(147.27, -215.2) * mm, "end": v(153.27, -215.2) * mm});
            skPoint(sketch, "E18.19.9.5", {"position": v(155.27, -165.2) * mm});
            skArc(sketch, "E18.20.9.5", {"start": v(155.27, -167.2) * mm, "mid": v(154.68, -165.8) * mm, "end": v(153.27, -165.2) * mm});
            skArc(sketch, "E18.24.9.5", {"start": v(153.27, -215.2) * mm, "mid": v(154.68, -214.62) * mm, "end": v(155.27, -213.2) * mm});
            skArc(sketch, "E18.28.9.5", {"start": v(147.27, -165.2) * mm, "mid": v(145.85, -165.8) * mm, "end": v(145.27, -167.2) * mm});
            skLineSegment(sketch, "E18.0.10.5", {"start": v(170.77, -213.2) * mm, "end": v(170.77, -167.2) * mm});
            skPoint(sketch, "E18.3.10.5", {"position": v(160.77, -215.2) * mm});
            skLineSegment(sketch, "E18.4.10.5", {"start": v(160.77, -213.2) * mm, "end": v(160.77, -167.2) * mm});
            skArc(sketch, "E18.7.10.5", {"start": v(160.77, -213.2) * mm, "mid": v(161.35, -214.62) * mm, "end": v(162.77, -215.2) * mm});
            skPoint(sketch, "E18.11.10.5", {"position": v(170.77, -215.2) * mm});
            skPoint(sketch, "E18.12.10.5", {"position": v(160.77, -165.2) * mm});
            skLineSegment(sketch, "E18.13.10.5", {"start": v(162.77, -165.2) * mm, "end": v(168.77, -165.2) * mm});
            skLineSegment(sketch, "E18.16.10.5", {"start": v(162.77, -215.2) * mm, "end": v(168.77, -215.2) * mm});
            skPoint(sketch, "E18.19.10.5", {"position": v(170.77, -165.2) * mm});
            skArc(sketch, "E18.20.10.5", {"start": v(170.77, -167.2) * mm, "mid": v(170.18, -165.8) * mm, "end": v(168.77, -165.2) * mm});
            skArc(sketch, "E18.24.10.5", {"start": v(168.77, -215.2) * mm, "mid": v(170.18, -214.62) * mm, "end": v(170.77, -213.2) * mm});
            skArc(sketch, "E18.28.10.5", {"start": v(162.77, -165.2) * mm, "mid": v(161.35, -165.8) * mm, "end": v(160.77, -167.2) * mm});
            skLineSegment(sketch, "E18.0.11.5", {"start": v(186.27, -213.2) * mm, "end": v(186.27, -167.2) * mm});
            skPoint(sketch, "E18.3.11.5", {"position": v(176.27, -215.2) * mm});
            skLineSegment(sketch, "E18.4.11.5", {"start": v(176.27, -213.2) * mm, "end": v(176.27, -167.2) * mm});
            skArc(sketch, "E18.7.11.5", {"start": v(176.27, -213.2) * mm, "mid": v(176.85, -214.62) * mm, "end": v(178.27, -215.2) * mm});
            skPoint(sketch, "E18.11.11.5", {"position": v(186.27, -215.2) * mm});
            skPoint(sketch, "E18.12.11.5", {"position": v(176.27, -165.2) * mm});
            skLineSegment(sketch, "E18.13.11.5", {"start": v(178.27, -165.2) * mm, "end": v(184.27, -165.2) * mm});
            skLineSegment(sketch, "E18.16.11.5", {"start": v(178.27, -215.2) * mm, "end": v(184.27, -215.2) * mm});
            skPoint(sketch, "E18.19.11.5", {"position": v(186.27, -165.2) * mm});
            skArc(sketch, "E18.20.11.5", {"start": v(186.27, -167.2) * mm, "mid": v(185.68, -165.8) * mm, "end": v(184.27, -165.2) * mm});
            skArc(sketch, "E18.24.11.5", {"start": v(184.27, -215.2) * mm, "mid": v(185.68, -214.62) * mm, "end": v(186.27, -213.2) * mm});
            skArc(sketch, "E18.28.11.5", {"start": v(178.27, -165.2) * mm, "mid": v(176.85, -165.8) * mm, "end": v(176.27, -167.2) * mm});
            skLineSegment(sketch, "E18.0.12.5", {"start": v(201.77, -213.2) * mm, "end": v(201.77, -167.2) * mm});
            skPoint(sketch, "E18.3.12.5", {"position": v(191.77, -215.2) * mm});
            skLineSegment(sketch, "E18.4.12.5", {"start": v(191.77, -213.2) * mm, "end": v(191.77, -167.2) * mm});
            skArc(sketch, "E18.7.12.5", {"start": v(191.77, -213.2) * mm, "mid": v(192.35, -214.62) * mm, "end": v(193.77, -215.2) * mm});
            skPoint(sketch, "E18.11.12.5", {"position": v(201.77, -215.2) * mm});
            skPoint(sketch, "E18.12.12.5", {"position": v(191.77, -165.2) * mm});
            skLineSegment(sketch, "E18.13.12.5", {"start": v(193.77, -165.2) * mm, "end": v(199.77, -165.2) * mm});
            skLineSegment(sketch, "E18.16.12.5", {"start": v(193.77, -215.2) * mm, "end": v(199.77, -215.2) * mm});
            skPoint(sketch, "E18.19.12.5", {"position": v(201.77, -165.2) * mm});
            skArc(sketch, "E18.20.12.5", {"start": v(201.77, -167.2) * mm, "mid": v(201.18, -165.8) * mm, "end": v(199.77, -165.2) * mm});
            skArc(sketch, "E18.24.12.5", {"start": v(199.77, -215.2) * mm, "mid": v(201.18, -214.62) * mm, "end": v(201.77, -213.2) * mm});
            skArc(sketch, "E18.28.12.5", {"start": v(193.77, -165.2) * mm, "mid": v(192.35, -165.8) * mm, "end": v(191.77, -167.2) * mm});
            skLineSegment(sketch, "E18.0.13.5", {"start": v(217.27, -213.2) * mm, "end": v(217.27, -167.2) * mm});
            skPoint(sketch, "E18.3.13.5", {"position": v(207.27, -215.2) * mm});
            skLineSegment(sketch, "E18.4.13.5", {"start": v(207.27, -213.2) * mm, "end": v(207.27, -167.2) * mm});
            skArc(sketch, "E18.7.13.5", {"start": v(207.27, -213.2) * mm, "mid": v(207.85, -214.62) * mm, "end": v(209.27, -215.2) * mm});
            skPoint(sketch, "E18.11.13.5", {"position": v(217.27, -215.2) * mm});
            skPoint(sketch, "E18.12.13.5", {"position": v(207.27, -165.2) * mm});
            skLineSegment(sketch, "E18.13.13.5", {"start": v(209.27, -165.2) * mm, "end": v(215.27, -165.2) * mm});
            skLineSegment(sketch, "E18.16.13.5", {"start": v(209.27, -215.2) * mm, "end": v(215.27, -215.2) * mm});
            skPoint(sketch, "E18.19.13.5", {"position": v(217.27, -165.2) * mm});
            skArc(sketch, "E18.20.13.5", {"start": v(217.27, -167.2) * mm, "mid": v(216.68, -165.8) * mm, "end": v(215.27, -165.2) * mm});
            skArc(sketch, "E18.24.13.5", {"start": v(215.27, -215.2) * mm, "mid": v(216.68, -214.62) * mm, "end": v(217.27, -213.2) * mm});
            skArc(sketch, "E18.28.13.5", {"start": v(209.27, -165.2) * mm, "mid": v(207.85, -165.8) * mm, "end": v(207.27, -167.2) * mm});
            skLineSegment(sketch, "E18.0.14.5", {"start": v(232.77, -213.2) * mm, "end": v(232.77, -167.2) * mm});
            skPoint(sketch, "E18.3.14.5", {"position": v(222.77, -215.2) * mm});
            skLineSegment(sketch, "E18.4.14.5", {"start": v(222.77, -213.2) * mm, "end": v(222.77, -167.2) * mm});
            skArc(sketch, "E18.7.14.5", {"start": v(222.77, -213.2) * mm, "mid": v(223.35, -214.62) * mm, "end": v(224.77, -215.2) * mm});
            skPoint(sketch, "E18.11.14.5", {"position": v(232.77, -215.2) * mm});
            skPoint(sketch, "E18.12.14.5", {"position": v(222.77, -165.2) * mm});
            skLineSegment(sketch, "E18.13.14.5", {"start": v(224.77, -165.2) * mm, "end": v(230.77, -165.2) * mm});
            skLineSegment(sketch, "E18.16.14.5", {"start": v(224.77, -215.2) * mm, "end": v(230.77, -215.2) * mm});
            skPoint(sketch, "E18.19.14.5", {"position": v(232.77, -165.2) * mm});
            skArc(sketch, "E18.20.14.5", {"start": v(232.77, -167.2) * mm, "mid": v(232.18, -165.8) * mm, "end": v(230.77, -165.2) * mm});
            skArc(sketch, "E18.24.14.5", {"start": v(230.77, -215.2) * mm, "mid": v(232.18, -214.62) * mm, "end": v(232.77, -213.2) * mm});
            skArc(sketch, "E18.28.14.5", {"start": v(224.77, -165.2) * mm, "mid": v(223.35, -165.8) * mm, "end": v(222.77, -167.2) * mm});
            skLineSegment(sketch, "E18.0.15.5", {"start": v(248.27, -213.2) * mm, "end": v(248.27, -167.2) * mm});
            skPoint(sketch, "E18.3.15.5", {"position": v(238.27, -215.2) * mm});
            skLineSegment(sketch, "E18.4.15.5", {"start": v(238.27, -213.2) * mm, "end": v(238.27, -167.2) * mm});
            skArc(sketch, "E18.7.15.5", {"start": v(238.27, -213.2) * mm, "mid": v(238.85, -214.62) * mm, "end": v(240.27, -215.2) * mm});
            skPoint(sketch, "E18.11.15.5", {"position": v(248.27, -215.2) * mm});
            skPoint(sketch, "E18.12.15.5", {"position": v(238.27, -165.2) * mm});
            skLineSegment(sketch, "E18.13.15.5", {"start": v(240.27, -165.2) * mm, "end": v(246.27, -165.2) * mm});
            skLineSegment(sketch, "E18.16.15.5", {"start": v(240.27, -215.2) * mm, "end": v(246.27, -215.2) * mm});
            skPoint(sketch, "E18.19.15.5", {"position": v(248.27, -165.2) * mm});
            skArc(sketch, "E18.20.15.5", {"start": v(248.27, -167.2) * mm, "mid": v(247.68, -165.8) * mm, "end": v(246.27, -165.2) * mm});
            skArc(sketch, "E18.24.15.5", {"start": v(246.27, -215.2) * mm, "mid": v(247.68, -214.62) * mm, "end": v(248.27, -213.2) * mm});
            skArc(sketch, "E18.28.15.5", {"start": v(240.27, -165.2) * mm, "mid": v(238.85, -165.8) * mm, "end": v(238.27, -167.2) * mm});
            skLineSegment(sketch, "E18.0.16.5", {"start": v(263.77, -213.2) * mm, "end": v(263.77, -167.2) * mm});
            skPoint(sketch, "E18.3.16.5", {"position": v(253.77, -215.2) * mm});
            skLineSegment(sketch, "E18.4.16.5", {"start": v(253.77, -213.2) * mm, "end": v(253.77, -167.2) * mm});
            skArc(sketch, "E18.7.16.5", {"start": v(253.77, -213.2) * mm, "mid": v(254.35, -214.62) * mm, "end": v(255.77, -215.2) * mm});
            skPoint(sketch, "E18.11.16.5", {"position": v(263.77, -215.2) * mm});
            skPoint(sketch, "E18.12.16.5", {"position": v(253.77, -165.2) * mm});
            skLineSegment(sketch, "E18.13.16.5", {"start": v(255.77, -165.2) * mm, "end": v(261.77, -165.2) * mm});
            skLineSegment(sketch, "E18.16.16.5", {"start": v(255.77, -215.2) * mm, "end": v(261.77, -215.2) * mm});
            skPoint(sketch, "E18.19.16.5", {"position": v(263.77, -165.2) * mm});
            skArc(sketch, "E18.20.16.5", {"start": v(263.77, -167.2) * mm, "mid": v(263.18, -165.8) * mm, "end": v(261.77, -165.2) * mm});
            skArc(sketch, "E18.24.16.5", {"start": v(261.77, -215.2) * mm, "mid": v(263.18, -214.62) * mm, "end": v(263.77, -213.2) * mm});
            skArc(sketch, "E18.28.16.5", {"start": v(255.77, -165.2) * mm, "mid": v(254.35, -165.8) * mm, "end": v(253.77, -167.2) * mm});
            skLineSegment(sketch, "E18.0.17.5", {"start": v(279.27, -213.2) * mm, "end": v(279.27, -167.2) * mm});
            skPoint(sketch, "E18.3.17.5", {"position": v(269.27, -215.2) * mm});
            skLineSegment(sketch, "E18.4.17.5", {"start": v(269.27, -213.2) * mm, "end": v(269.27, -167.2) * mm});
            skArc(sketch, "E18.7.17.5", {"start": v(269.27, -213.2) * mm, "mid": v(269.85, -214.62) * mm, "end": v(271.27, -215.2) * mm});
            skPoint(sketch, "E18.11.17.5", {"position": v(279.27, -215.2) * mm});
            skPoint(sketch, "E18.12.17.5", {"position": v(269.27, -165.2) * mm});
            skLineSegment(sketch, "E18.13.17.5", {"start": v(271.27, -165.2) * mm, "end": v(277.27, -165.2) * mm});
            skLineSegment(sketch, "E18.16.17.5", {"start": v(271.27, -215.2) * mm, "end": v(277.27, -215.2) * mm});
            skPoint(sketch, "E18.19.17.5", {"position": v(279.27, -165.2) * mm});
            skArc(sketch, "E18.20.17.5", {"start": v(279.27, -167.2) * mm, "mid": v(278.68, -165.8) * mm, "end": v(277.27, -165.2) * mm});
            skArc(sketch, "E18.24.17.5", {"start": v(277.27, -215.2) * mm, "mid": v(278.68, -214.62) * mm, "end": v(279.27, -213.2) * mm});
            skArc(sketch, "E18.28.17.5", {"start": v(271.27, -165.2) * mm, "mid": v(269.85, -165.8) * mm, "end": v(269.27, -167.2) * mm});
            skLineSegment(sketch, "E18.0.18.5", {"start": v(294.77, -213.2) * mm, "end": v(294.77, -167.2) * mm});
            skPoint(sketch, "E18.3.18.5", {"position": v(284.77, -215.2) * mm});
            skLineSegment(sketch, "E18.4.18.5", {"start": v(284.77, -213.2) * mm, "end": v(284.77, -167.2) * mm});
            skArc(sketch, "E18.7.18.5", {"start": v(284.77, -213.2) * mm, "mid": v(285.35, -214.62) * mm, "end": v(286.77, -215.2) * mm});
            skPoint(sketch, "E18.11.18.5", {"position": v(294.77, -215.2) * mm});
            skPoint(sketch, "E18.12.18.5", {"position": v(284.77, -165.2) * mm});
            skLineSegment(sketch, "E18.13.18.5", {"start": v(286.77, -165.2) * mm, "end": v(292.77, -165.2) * mm});
            skLineSegment(sketch, "E18.16.18.5", {"start": v(286.77, -215.2) * mm, "end": v(292.77, -215.2) * mm});
            skPoint(sketch, "E18.19.18.5", {"position": v(294.77, -165.2) * mm});
            skArc(sketch, "E18.20.18.5", {"start": v(294.77, -167.2) * mm, "mid": v(294.18, -165.8) * mm, "end": v(292.77, -165.2) * mm});
            skArc(sketch, "E18.24.18.5", {"start": v(292.77, -215.2) * mm, "mid": v(294.18, -214.62) * mm, "end": v(294.77, -213.2) * mm});
            skArc(sketch, "E18.28.18.5", {"start": v(286.77, -165.2) * mm, "mid": v(285.35, -165.8) * mm, "end": v(284.77, -167.2) * mm});
            skPoint(sketch, "E19.3.0.6", {"position": v(5.77, -155.2) * mm});
            skPoint(sketch, "E19.11.0.6", {"position": v(15.77, -155.2) * mm});
            skPoint(sketch, "E19.12.0.6", {"position": v(5.77, -105.2) * mm});
            skPoint(sketch, "E19.19.0.6", {"position": v(15.77, -105.2) * mm});
            skPoint(sketch, "E19.3.0.7", {"position": v(5.77, -95.2) * mm});
            skPoint(sketch, "E19.11.0.7", {"position": v(15.77, -95.2) * mm});
            skPoint(sketch, "E19.12.0.7", {"position": v(5.77, -45.2) * mm});
            skPoint(sketch, "E19.19.0.7", {"position": v(15.77, -45.2) * mm});
            skLineSegment(sketch, "E19.0.1.6", {"start": v(31.27, -153.2) * mm, "end": v(31.27, -107.2) * mm});
            skPoint(sketch, "E19.3.1.6", {"position": v(21.27, -155.2) * mm});
            skLineSegment(sketch, "E19.4.1.6", {"start": v(21.27, -153.2) * mm, "end": v(21.27, -107.2) * mm});
            skArc(sketch, "E19.7.1.6", {"start": v(21.27, -153.2) * mm, "mid": v(21.85, -154.62) * mm, "end": v(23.27, -155.2) * mm});
            skPoint(sketch, "E19.11.1.6", {"position": v(31.27, -155.2) * mm});
            skPoint(sketch, "E19.12.1.6", {"position": v(21.27, -105.2) * mm});
            skLineSegment(sketch, "E19.13.1.6", {"start": v(23.27, -105.2) * mm, "end": v(29.27, -105.2) * mm});
            skLineSegment(sketch, "E19.16.1.6", {"start": v(23.27, -155.2) * mm, "end": v(29.27, -155.2) * mm});
            skPoint(sketch, "E19.19.1.6", {"position": v(31.27, -105.2) * mm});
            skArc(sketch, "E19.20.1.6", {"start": v(31.27, -107.2) * mm, "mid": v(30.68, -105.8) * mm, "end": v(29.27, -105.2) * mm});
            skArc(sketch, "E19.24.1.6", {"start": v(29.27, -155.2) * mm, "mid": v(30.68, -154.62) * mm, "end": v(31.27, -153.2) * mm});
            skArc(sketch, "E19.28.1.6", {"start": v(23.27, -105.2) * mm, "mid": v(21.85, -105.8) * mm, "end": v(21.27, -107.2) * mm});
            skLineSegment(sketch, "E19.0.1.7", {"start": v(31.27, -93.2) * mm, "end": v(31.27, -47.2) * mm});
            skPoint(sketch, "E19.3.1.7", {"position": v(21.27, -95.2) * mm});
            skLineSegment(sketch, "E19.4.1.7", {"start": v(21.27, -93.2) * mm, "end": v(21.27, -47.2) * mm});
            skArc(sketch, "E19.7.1.7", {"start": v(21.27, -93.2) * mm, "mid": v(21.85, -94.62) * mm, "end": v(23.27, -95.2) * mm});
            skPoint(sketch, "E19.11.1.7", {"position": v(31.27, -95.2) * mm});
            skPoint(sketch, "E19.12.1.7", {"position": v(21.27, -45.2) * mm});
            skLineSegment(sketch, "E19.13.1.7", {"start": v(23.27, -45.2) * mm, "end": v(29.27, -45.2) * mm});
            skLineSegment(sketch, "E19.16.1.7", {"start": v(23.27, -95.2) * mm, "end": v(29.27, -95.2) * mm});
            skPoint(sketch, "E19.19.1.7", {"position": v(31.27, -45.2) * mm});
            skArc(sketch, "E19.20.1.7", {"start": v(31.27, -47.2) * mm, "mid": v(30.68, -45.8) * mm, "end": v(29.27, -45.2) * mm});
            skArc(sketch, "E19.24.1.7", {"start": v(29.27, -95.2) * mm, "mid": v(30.68, -94.62) * mm, "end": v(31.27, -93.2) * mm});
            skArc(sketch, "E19.28.1.7", {"start": v(23.27, -45.2) * mm, "mid": v(21.85, -45.8) * mm, "end": v(21.27, -47.2) * mm});
            skLineSegment(sketch, "E19.0.2.6", {"start": v(46.77, -153.2) * mm, "end": v(46.77, -107.2) * mm});
            skPoint(sketch, "E19.3.2.6", {"position": v(36.77, -155.2) * mm});
            skLineSegment(sketch, "E19.4.2.6", {"start": v(36.77, -153.2) * mm, "end": v(36.77, -107.2) * mm});
            skArc(sketch, "E19.7.2.6", {"start": v(36.77, -153.2) * mm, "mid": v(37.35, -154.62) * mm, "end": v(38.77, -155.2) * mm});
            skPoint(sketch, "E19.11.2.6", {"position": v(46.77, -155.2) * mm});
            skPoint(sketch, "E19.12.2.6", {"position": v(36.77, -105.2) * mm});
            skLineSegment(sketch, "E19.13.2.6", {"start": v(38.77, -105.2) * mm, "end": v(44.77, -105.2) * mm});
            skLineSegment(sketch, "E19.16.2.6", {"start": v(38.77, -155.2) * mm, "end": v(44.77, -155.2) * mm});
            skPoint(sketch, "E19.19.2.6", {"position": v(46.77, -105.2) * mm});
            skArc(sketch, "E19.20.2.6", {"start": v(46.77, -107.2) * mm, "mid": v(46.18, -105.8) * mm, "end": v(44.77, -105.2) * mm});
            skArc(sketch, "E19.24.2.6", {"start": v(44.77, -155.2) * mm, "mid": v(46.18, -154.62) * mm, "end": v(46.77, -153.2) * mm});
            skArc(sketch, "E19.28.2.6", {"start": v(38.77, -105.2) * mm, "mid": v(37.35, -105.8) * mm, "end": v(36.77, -107.2) * mm});
            skLineSegment(sketch, "E19.0.2.7", {"start": v(46.77, -93.2) * mm, "end": v(46.77, -47.2) * mm});
            skPoint(sketch, "E19.3.2.7", {"position": v(36.77, -95.2) * mm});
            skLineSegment(sketch, "E19.4.2.7", {"start": v(36.77, -93.2) * mm, "end": v(36.77, -47.2) * mm});
            skArc(sketch, "E19.7.2.7", {"start": v(36.77, -93.2) * mm, "mid": v(37.35, -94.62) * mm, "end": v(38.77, -95.2) * mm});
            skPoint(sketch, "E19.11.2.7", {"position": v(46.77, -95.2) * mm});
            skPoint(sketch, "E19.12.2.7", {"position": v(36.77, -45.2) * mm});
            skLineSegment(sketch, "E19.13.2.7", {"start": v(38.77, -45.2) * mm, "end": v(44.77, -45.2) * mm});
            skLineSegment(sketch, "E19.16.2.7", {"start": v(38.77, -95.2) * mm, "end": v(44.77, -95.2) * mm});
            skPoint(sketch, "E19.19.2.7", {"position": v(46.77, -45.2) * mm});
            skArc(sketch, "E19.20.2.7", {"start": v(46.77, -47.2) * mm, "mid": v(46.18, -45.8) * mm, "end": v(44.77, -45.2) * mm});
            skArc(sketch, "E19.24.2.7", {"start": v(44.77, -95.2) * mm, "mid": v(46.18, -94.62) * mm, "end": v(46.77, -93.2) * mm});
            skArc(sketch, "E19.28.2.7", {"start": v(38.77, -45.2) * mm, "mid": v(37.35, -45.8) * mm, "end": v(36.77, -47.2) * mm});
            skLineSegment(sketch, "E19.0.3.6", {"start": v(62.27, -153.2) * mm, "end": v(62.27, -107.2) * mm});
            skPoint(sketch, "E19.3.3.6", {"position": v(52.27, -155.2) * mm});
            skLineSegment(sketch, "E19.4.3.6", {"start": v(52.27, -153.2) * mm, "end": v(52.27, -107.2) * mm});
            skArc(sketch, "E19.7.3.6", {"start": v(52.27, -153.2) * mm, "mid": v(52.85, -154.62) * mm, "end": v(54.27, -155.2) * mm});
            skPoint(sketch, "E19.11.3.6", {"position": v(62.27, -155.2) * mm});
            skPoint(sketch, "E19.12.3.6", {"position": v(52.27, -105.2) * mm});
            skLineSegment(sketch, "E19.13.3.6", {"start": v(54.27, -105.2) * mm, "end": v(60.27, -105.2) * mm});
            skLineSegment(sketch, "E19.16.3.6", {"start": v(54.27, -155.2) * mm, "end": v(60.27, -155.2) * mm});
            skPoint(sketch, "E19.19.3.6", {"position": v(62.27, -105.2) * mm});
            skArc(sketch, "E19.20.3.6", {"start": v(62.27, -107.2) * mm, "mid": v(61.68, -105.8) * mm, "end": v(60.27, -105.2) * mm});
            skArc(sketch, "E19.24.3.6", {"start": v(60.27, -155.2) * mm, "mid": v(61.68, -154.62) * mm, "end": v(62.27, -153.2) * mm});
            skArc(sketch, "E19.28.3.6", {"start": v(54.27, -105.2) * mm, "mid": v(52.85, -105.8) * mm, "end": v(52.27, -107.2) * mm});
            skLineSegment(sketch, "E19.0.3.7", {"start": v(62.27, -93.2) * mm, "end": v(62.27, -47.2) * mm});
            skPoint(sketch, "E19.3.3.7", {"position": v(52.27, -95.2) * mm});
            skLineSegment(sketch, "E19.4.3.7", {"start": v(52.27, -93.2) * mm, "end": v(52.27, -47.2) * mm});
            skArc(sketch, "E19.7.3.7", {"start": v(52.27, -93.2) * mm, "mid": v(52.85, -94.62) * mm, "end": v(54.27, -95.2) * mm});
            skPoint(sketch, "E19.11.3.7", {"position": v(62.27, -95.2) * mm});
            skPoint(sketch, "E19.12.3.7", {"position": v(52.27, -45.2) * mm});
            skLineSegment(sketch, "E19.13.3.7", {"start": v(54.27, -45.2) * mm, "end": v(60.27, -45.2) * mm});
            skLineSegment(sketch, "E19.16.3.7", {"start": v(54.27, -95.2) * mm, "end": v(60.27, -95.2) * mm});
            skPoint(sketch, "E19.19.3.7", {"position": v(62.27, -45.2) * mm});
            skArc(sketch, "E19.20.3.7", {"start": v(62.27, -47.2) * mm, "mid": v(61.68, -45.8) * mm, "end": v(60.27, -45.2) * mm});
            skArc(sketch, "E19.24.3.7", {"start": v(60.27, -95.2) * mm, "mid": v(61.68, -94.62) * mm, "end": v(62.27, -93.2) * mm});
            skArc(sketch, "E19.28.3.7", {"start": v(54.27, -45.2) * mm, "mid": v(52.85, -45.8) * mm, "end": v(52.27, -47.2) * mm});
            skLineSegment(sketch, "E19.0.4.6", {"start": v(77.77, -153.2) * mm, "end": v(77.77, -107.2) * mm});
            skPoint(sketch, "E19.3.4.6", {"position": v(67.77, -155.2) * mm});
            skLineSegment(sketch, "E19.4.4.6", {"start": v(67.77, -153.2) * mm, "end": v(67.77, -107.2) * mm});
            skArc(sketch, "E19.7.4.6", {"start": v(67.77, -153.2) * mm, "mid": v(68.35, -154.62) * mm, "end": v(69.77, -155.2) * mm});
            skPoint(sketch, "E19.11.4.6", {"position": v(77.77, -155.2) * mm});
            skPoint(sketch, "E19.12.4.6", {"position": v(67.77, -105.2) * mm});
            skLineSegment(sketch, "E19.13.4.6", {"start": v(69.77, -105.2) * mm, "end": v(75.77, -105.2) * mm});
            skLineSegment(sketch, "E19.16.4.6", {"start": v(69.77, -155.2) * mm, "end": v(75.77, -155.2) * mm});
            skPoint(sketch, "E19.19.4.6", {"position": v(77.77, -105.2) * mm});
            skArc(sketch, "E19.20.4.6", {"start": v(77.77, -107.2) * mm, "mid": v(77.18, -105.8) * mm, "end": v(75.77, -105.2) * mm});
            skArc(sketch, "E19.24.4.6", {"start": v(75.77, -155.2) * mm, "mid": v(77.18, -154.62) * mm, "end": v(77.77, -153.2) * mm});
            skArc(sketch, "E19.28.4.6", {"start": v(69.77, -105.2) * mm, "mid": v(68.35, -105.8) * mm, "end": v(67.77, -107.2) * mm});
            skLineSegment(sketch, "E19.0.4.7", {"start": v(77.77, -93.2) * mm, "end": v(77.77, -47.2) * mm});
            skPoint(sketch, "E19.3.4.7", {"position": v(67.77, -95.2) * mm});
            skLineSegment(sketch, "E19.4.4.7", {"start": v(67.77, -93.2) * mm, "end": v(67.77, -47.2) * mm});
            skArc(sketch, "E19.7.4.7", {"start": v(67.77, -93.2) * mm, "mid": v(68.35, -94.62) * mm, "end": v(69.77, -95.2) * mm});
            skPoint(sketch, "E19.11.4.7", {"position": v(77.77, -95.2) * mm});
            skPoint(sketch, "E19.12.4.7", {"position": v(67.77, -45.2) * mm});
            skLineSegment(sketch, "E19.13.4.7", {"start": v(69.77, -45.2) * mm, "end": v(75.77, -45.2) * mm});
            skLineSegment(sketch, "E19.16.4.7", {"start": v(69.77, -95.2) * mm, "end": v(75.77, -95.2) * mm});
            skPoint(sketch, "E19.19.4.7", {"position": v(77.77, -45.2) * mm});
            skArc(sketch, "E19.20.4.7", {"start": v(77.77, -47.2) * mm, "mid": v(77.18, -45.8) * mm, "end": v(75.77, -45.2) * mm});
            skArc(sketch, "E19.24.4.7", {"start": v(75.77, -95.2) * mm, "mid": v(77.18, -94.62) * mm, "end": v(77.77, -93.2) * mm});
            skArc(sketch, "E19.28.4.7", {"start": v(69.77, -45.2) * mm, "mid": v(68.35, -45.8) * mm, "end": v(67.77, -47.2) * mm});
            skLineSegment(sketch, "E19.0.5.6", {"start": v(93.27, -153.2) * mm, "end": v(93.27, -107.2) * mm});
            skPoint(sketch, "E19.3.5.6", {"position": v(83.27, -155.2) * mm});
            skLineSegment(sketch, "E19.4.5.6", {"start": v(83.27, -153.2) * mm, "end": v(83.27, -107.2) * mm});
            skArc(sketch, "E19.7.5.6", {"start": v(83.27, -153.2) * mm, "mid": v(83.85, -154.62) * mm, "end": v(85.27, -155.2) * mm});
            skPoint(sketch, "E19.11.5.6", {"position": v(93.27, -155.2) * mm});
            skPoint(sketch, "E19.12.5.6", {"position": v(83.27, -105.2) * mm});
            skLineSegment(sketch, "E19.13.5.6", {"start": v(85.27, -105.2) * mm, "end": v(91.27, -105.2) * mm});
            skLineSegment(sketch, "E19.16.5.6", {"start": v(85.27, -155.2) * mm, "end": v(91.27, -155.2) * mm});
            skPoint(sketch, "E19.19.5.6", {"position": v(93.27, -105.2) * mm});
            skArc(sketch, "E19.20.5.6", {"start": v(93.27, -107.2) * mm, "mid": v(92.68, -105.8) * mm, "end": v(91.27, -105.2) * mm});
            skArc(sketch, "E19.24.5.6", {"start": v(91.27, -155.2) * mm, "mid": v(92.68, -154.62) * mm, "end": v(93.27, -153.2) * mm});
            skArc(sketch, "E19.28.5.6", {"start": v(85.27, -105.2) * mm, "mid": v(83.85, -105.8) * mm, "end": v(83.27, -107.2) * mm});
            skLineSegment(sketch, "E19.0.5.7", {"start": v(93.27, -93.2) * mm, "end": v(93.27, -47.2) * mm});
            skPoint(sketch, "E19.3.5.7", {"position": v(83.27, -95.2) * mm});
            skLineSegment(sketch, "E19.4.5.7", {"start": v(83.27, -93.2) * mm, "end": v(83.27, -47.2) * mm});
            skArc(sketch, "E19.7.5.7", {"start": v(83.27, -93.2) * mm, "mid": v(83.85, -94.62) * mm, "end": v(85.27, -95.2) * mm});
            skPoint(sketch, "E19.11.5.7", {"position": v(93.27, -95.2) * mm});
            skPoint(sketch, "E19.12.5.7", {"position": v(83.27, -45.2) * mm});
            skLineSegment(sketch, "E19.13.5.7", {"start": v(85.27, -45.2) * mm, "end": v(91.27, -45.2) * mm});
            skLineSegment(sketch, "E19.16.5.7", {"start": v(85.27, -95.2) * mm, "end": v(91.27, -95.2) * mm});
            skPoint(sketch, "E19.19.5.7", {"position": v(93.27, -45.2) * mm});
            skArc(sketch, "E19.20.5.7", {"start": v(93.27, -47.2) * mm, "mid": v(92.68, -45.8) * mm, "end": v(91.27, -45.2) * mm});
            skArc(sketch, "E19.24.5.7", {"start": v(91.27, -95.2) * mm, "mid": v(92.68, -94.62) * mm, "end": v(93.27, -93.2) * mm});
            skArc(sketch, "E19.28.5.7", {"start": v(85.27, -45.2) * mm, "mid": v(83.85, -45.8) * mm, "end": v(83.27, -47.2) * mm});
            skLineSegment(sketch, "E19.0.6.6", {"start": v(108.77, -153.2) * mm, "end": v(108.77, -107.2) * mm});
            skPoint(sketch, "E19.3.6.6", {"position": v(98.77, -155.2) * mm});
            skLineSegment(sketch, "E19.4.6.6", {"start": v(98.77, -153.2) * mm, "end": v(98.77, -107.2) * mm});
            skArc(sketch, "E19.7.6.6", {"start": v(98.77, -153.2) * mm, "mid": v(99.35, -154.62) * mm, "end": v(100.77, -155.2) * mm});
            skPoint(sketch, "E19.11.6.6", {"position": v(108.77, -155.2) * mm});
            skPoint(sketch, "E19.12.6.6", {"position": v(98.77, -105.2) * mm});
            skLineSegment(sketch, "E19.13.6.6", {"start": v(100.77, -105.2) * mm, "end": v(106.77, -105.2) * mm});
            skLineSegment(sketch, "E19.16.6.6", {"start": v(100.77, -155.2) * mm, "end": v(106.77, -155.2) * mm});
            skPoint(sketch, "E19.19.6.6", {"position": v(108.77, -105.2) * mm});
            skArc(sketch, "E19.20.6.6", {"start": v(108.77, -107.2) * mm, "mid": v(108.18, -105.8) * mm, "end": v(106.77, -105.2) * mm});
            skArc(sketch, "E19.24.6.6", {"start": v(106.77, -155.2) * mm, "mid": v(108.18, -154.62) * mm, "end": v(108.77, -153.2) * mm});
            skArc(sketch, "E19.28.6.6", {"start": v(100.77, -105.2) * mm, "mid": v(99.35, -105.8) * mm, "end": v(98.77, -107.2) * mm});
            skLineSegment(sketch, "E19.0.6.7", {"start": v(108.77, -93.2) * mm, "end": v(108.77, -47.2) * mm});
            skPoint(sketch, "E19.3.6.7", {"position": v(98.77, -95.2) * mm});
            skLineSegment(sketch, "E19.4.6.7", {"start": v(98.77, -93.2) * mm, "end": v(98.77, -47.2) * mm});
            skArc(sketch, "E19.7.6.7", {"start": v(98.77, -93.2) * mm, "mid": v(99.35, -94.62) * mm, "end": v(100.77, -95.2) * mm});
            skPoint(sketch, "E19.11.6.7", {"position": v(108.77, -95.2) * mm});
            skPoint(sketch, "E19.12.6.7", {"position": v(98.77, -45.2) * mm});
            skLineSegment(sketch, "E19.13.6.7", {"start": v(100.77, -45.2) * mm, "end": v(106.77, -45.2) * mm});
            skLineSegment(sketch, "E19.16.6.7", {"start": v(100.77, -95.2) * mm, "end": v(106.77, -95.2) * mm});
            skPoint(sketch, "E19.19.6.7", {"position": v(108.77, -45.2) * mm});
            skArc(sketch, "E19.20.6.7", {"start": v(108.77, -47.2) * mm, "mid": v(108.18, -45.8) * mm, "end": v(106.77, -45.2) * mm});
            skArc(sketch, "E19.24.6.7", {"start": v(106.77, -95.2) * mm, "mid": v(108.18, -94.62) * mm, "end": v(108.77, -93.2) * mm});
            skArc(sketch, "E19.28.6.7", {"start": v(100.77, -45.2) * mm, "mid": v(99.35, -45.8) * mm, "end": v(98.77, -47.2) * mm});
            skLineSegment(sketch, "E19.0.7.6", {"start": v(124.27, -153.2) * mm, "end": v(124.27, -107.2) * mm});
            skPoint(sketch, "E19.3.7.6", {"position": v(114.27, -155.2) * mm});
            skLineSegment(sketch, "E19.4.7.6", {"start": v(114.27, -153.2) * mm, "end": v(114.27, -107.2) * mm});
            skArc(sketch, "E19.7.7.6", {"start": v(114.27, -153.2) * mm, "mid": v(114.85, -154.62) * mm, "end": v(116.27, -155.2) * mm});
            skPoint(sketch, "E19.11.7.6", {"position": v(124.27, -155.2) * mm});
            skPoint(sketch, "E19.12.7.6", {"position": v(114.27, -105.2) * mm});
            skLineSegment(sketch, "E19.13.7.6", {"start": v(116.27, -105.2) * mm, "end": v(122.27, -105.2) * mm});
            skLineSegment(sketch, "E19.16.7.6", {"start": v(116.27, -155.2) * mm, "end": v(122.27, -155.2) * mm});
            skPoint(sketch, "E19.19.7.6", {"position": v(124.27, -105.2) * mm});
            skArc(sketch, "E19.20.7.6", {"start": v(124.27, -107.2) * mm, "mid": v(123.68, -105.8) * mm, "end": v(122.27, -105.2) * mm});
            skArc(sketch, "E19.24.7.6", {"start": v(122.27, -155.2) * mm, "mid": v(123.68, -154.62) * mm, "end": v(124.27, -153.2) * mm});
            skArc(sketch, "E19.28.7.6", {"start": v(116.27, -105.2) * mm, "mid": v(114.85, -105.8) * mm, "end": v(114.27, -107.2) * mm});
            skLineSegment(sketch, "E19.0.7.7", {"start": v(124.27, -93.2) * mm, "end": v(124.27, -47.2) * mm});
            skPoint(sketch, "E19.3.7.7", {"position": v(114.27, -95.2) * mm});
            skLineSegment(sketch, "E19.4.7.7", {"start": v(114.27, -93.2) * mm, "end": v(114.27, -47.2) * mm});
            skArc(sketch, "E19.7.7.7", {"start": v(114.27, -93.2) * mm, "mid": v(114.85, -94.62) * mm, "end": v(116.27, -95.2) * mm});
            skPoint(sketch, "E19.11.7.7", {"position": v(124.27, -95.2) * mm});
            skPoint(sketch, "E19.12.7.7", {"position": v(114.27, -45.2) * mm});
            skLineSegment(sketch, "E19.13.7.7", {"start": v(116.27, -45.2) * mm, "end": v(122.27, -45.2) * mm});
            skLineSegment(sketch, "E19.16.7.7", {"start": v(116.27, -95.2) * mm, "end": v(122.27, -95.2) * mm});
            skPoint(sketch, "E19.19.7.7", {"position": v(124.27, -45.2) * mm});
            skArc(sketch, "E19.20.7.7", {"start": v(124.27, -47.2) * mm, "mid": v(123.68, -45.8) * mm, "end": v(122.27, -45.2) * mm});
            skArc(sketch, "E19.24.7.7", {"start": v(122.27, -95.2) * mm, "mid": v(123.68, -94.62) * mm, "end": v(124.27, -93.2) * mm});
            skArc(sketch, "E19.28.7.7", {"start": v(116.27, -45.2) * mm, "mid": v(114.85, -45.8) * mm, "end": v(114.27, -47.2) * mm});
            skLineSegment(sketch, "E19.0.8.6", {"start": v(139.77, -153.2) * mm, "end": v(139.77, -107.2) * mm});
            skPoint(sketch, "E19.3.8.6", {"position": v(129.77, -155.2) * mm});
            skLineSegment(sketch, "E19.4.8.6", {"start": v(129.77, -153.2) * mm, "end": v(129.77, -107.2) * mm});
            skArc(sketch, "E19.7.8.6", {"start": v(129.77, -153.2) * mm, "mid": v(130.35, -154.62) * mm, "end": v(131.77, -155.2) * mm});
            skPoint(sketch, "E19.11.8.6", {"position": v(139.77, -155.2) * mm});
            skPoint(sketch, "E19.12.8.6", {"position": v(129.77, -105.2) * mm});
            skLineSegment(sketch, "E19.13.8.6", {"start": v(131.77, -105.2) * mm, "end": v(137.77, -105.2) * mm});
            skLineSegment(sketch, "E19.16.8.6", {"start": v(131.77, -155.2) * mm, "end": v(137.77, -155.2) * mm});
            skPoint(sketch, "E19.19.8.6", {"position": v(139.77, -105.2) * mm});
            skArc(sketch, "E19.20.8.6", {"start": v(139.77, -107.2) * mm, "mid": v(139.18, -105.8) * mm, "end": v(137.77, -105.2) * mm});
            skArc(sketch, "E19.24.8.6", {"start": v(137.77, -155.2) * mm, "mid": v(139.18, -154.62) * mm, "end": v(139.77, -153.2) * mm});
            skArc(sketch, "E19.28.8.6", {"start": v(131.77, -105.2) * mm, "mid": v(130.35, -105.8) * mm, "end": v(129.77, -107.2) * mm});
            skLineSegment(sketch, "E19.0.8.7", {"start": v(139.77, -93.2) * mm, "end": v(139.77, -47.2) * mm});
            skPoint(sketch, "E19.3.8.7", {"position": v(129.77, -95.2) * mm});
            skLineSegment(sketch, "E19.4.8.7", {"start": v(129.77, -93.2) * mm, "end": v(129.77, -47.2) * mm});
            skArc(sketch, "E19.7.8.7", {"start": v(129.77, -93.2) * mm, "mid": v(130.35, -94.62) * mm, "end": v(131.77, -95.2) * mm});
            skPoint(sketch, "E19.11.8.7", {"position": v(139.77, -95.2) * mm});
            skPoint(sketch, "E19.12.8.7", {"position": v(129.77, -45.2) * mm});
            skLineSegment(sketch, "E19.13.8.7", {"start": v(131.77, -45.2) * mm, "end": v(137.77, -45.2) * mm});
            skLineSegment(sketch, "E19.16.8.7", {"start": v(131.77, -95.2) * mm, "end": v(137.77, -95.2) * mm});
            skPoint(sketch, "E19.19.8.7", {"position": v(139.77, -45.2) * mm});
            skArc(sketch, "E19.20.8.7", {"start": v(139.77, -47.2) * mm, "mid": v(139.18, -45.8) * mm, "end": v(137.77, -45.2) * mm});
            skArc(sketch, "E19.24.8.7", {"start": v(137.77, -95.2) * mm, "mid": v(139.18, -94.62) * mm, "end": v(139.77, -93.2) * mm});
            skArc(sketch, "E19.28.8.7", {"start": v(131.77, -45.2) * mm, "mid": v(130.35, -45.8) * mm, "end": v(129.77, -47.2) * mm});
            skLineSegment(sketch, "E19.0.9.6", {"start": v(155.27, -153.2) * mm, "end": v(155.27, -107.2) * mm});
            skPoint(sketch, "E19.3.9.6", {"position": v(145.27, -155.2) * mm});
            skLineSegment(sketch, "E19.4.9.6", {"start": v(145.27, -153.2) * mm, "end": v(145.27, -107.2) * mm});
            skArc(sketch, "E19.7.9.6", {"start": v(145.27, -153.2) * mm, "mid": v(145.85, -154.62) * mm, "end": v(147.27, -155.2) * mm});
            skPoint(sketch, "E19.11.9.6", {"position": v(155.27, -155.2) * mm});
            skPoint(sketch, "E19.12.9.6", {"position": v(145.27, -105.2) * mm});
            skLineSegment(sketch, "E19.13.9.6", {"start": v(147.27, -105.2) * mm, "end": v(153.27, -105.2) * mm});
            skLineSegment(sketch, "E19.16.9.6", {"start": v(147.27, -155.2) * mm, "end": v(153.27, -155.2) * mm});
            skPoint(sketch, "E19.19.9.6", {"position": v(155.27, -105.2) * mm});
            skArc(sketch, "E19.20.9.6", {"start": v(155.27, -107.2) * mm, "mid": v(154.68, -105.8) * mm, "end": v(153.27, -105.2) * mm});
            skArc(sketch, "E19.24.9.6", {"start": v(153.27, -155.2) * mm, "mid": v(154.68, -154.62) * mm, "end": v(155.27, -153.2) * mm});
            skArc(sketch, "E19.28.9.6", {"start": v(147.27, -105.2) * mm, "mid": v(145.85, -105.8) * mm, "end": v(145.27, -107.2) * mm});
            skLineSegment(sketch, "E19.0.9.7", {"start": v(155.27, -93.2) * mm, "end": v(155.27, -47.2) * mm});
            skPoint(sketch, "E19.3.9.7", {"position": v(145.27, -95.2) * mm});
            skLineSegment(sketch, "E19.4.9.7", {"start": v(145.27, -93.2) * mm, "end": v(145.27, -47.2) * mm});
            skArc(sketch, "E19.7.9.7", {"start": v(145.27, -93.2) * mm, "mid": v(145.85, -94.62) * mm, "end": v(147.27, -95.2) * mm});
            skPoint(sketch, "E19.11.9.7", {"position": v(155.27, -95.2) * mm});
            skPoint(sketch, "E19.12.9.7", {"position": v(145.27, -45.2) * mm});
            skLineSegment(sketch, "E19.13.9.7", {"start": v(147.27, -45.2) * mm, "end": v(153.27, -45.2) * mm});
            skLineSegment(sketch, "E19.16.9.7", {"start": v(147.27, -95.2) * mm, "end": v(153.27, -95.2) * mm});
            skPoint(sketch, "E19.19.9.7", {"position": v(155.27, -45.2) * mm});
            skArc(sketch, "E19.20.9.7", {"start": v(155.27, -47.2) * mm, "mid": v(154.68, -45.8) * mm, "end": v(153.27, -45.2) * mm});
            skArc(sketch, "E19.24.9.7", {"start": v(153.27, -95.2) * mm, "mid": v(154.68, -94.62) * mm, "end": v(155.27, -93.2) * mm});
            skArc(sketch, "E19.28.9.7", {"start": v(147.27, -45.2) * mm, "mid": v(145.85, -45.8) * mm, "end": v(145.27, -47.2) * mm});
            skLineSegment(sketch, "E19.0.10.6", {"start": v(170.77, -153.2) * mm, "end": v(170.77, -107.2) * mm});
            skPoint(sketch, "E19.3.10.6", {"position": v(160.77, -155.2) * mm});
            skLineSegment(sketch, "E19.4.10.6", {"start": v(160.77, -153.2) * mm, "end": v(160.77, -107.2) * mm});
            skArc(sketch, "E19.7.10.6", {"start": v(160.77, -153.2) * mm, "mid": v(161.35, -154.62) * mm, "end": v(162.77, -155.2) * mm});
            skPoint(sketch, "E19.11.10.6", {"position": v(170.77, -155.2) * mm});
            skPoint(sketch, "E19.12.10.6", {"position": v(160.77, -105.2) * mm});
            skLineSegment(sketch, "E19.13.10.6", {"start": v(162.77, -105.2) * mm, "end": v(168.77, -105.2) * mm});
            skLineSegment(sketch, "E19.16.10.6", {"start": v(162.77, -155.2) * mm, "end": v(168.77, -155.2) * mm});
            skPoint(sketch, "E19.19.10.6", {"position": v(170.77, -105.2) * mm});
            skArc(sketch, "E19.20.10.6", {"start": v(170.77, -107.2) * mm, "mid": v(170.18, -105.8) * mm, "end": v(168.77, -105.2) * mm});
            skArc(sketch, "E19.24.10.6", {"start": v(168.77, -155.2) * mm, "mid": v(170.18, -154.62) * mm, "end": v(170.77, -153.2) * mm});
            skArc(sketch, "E19.28.10.6", {"start": v(162.77, -105.2) * mm, "mid": v(161.35, -105.8) * mm, "end": v(160.77, -107.2) * mm});
            skLineSegment(sketch, "E19.0.10.7", {"start": v(170.77, -93.2) * mm, "end": v(170.77, -47.2) * mm});
            skPoint(sketch, "E19.3.10.7", {"position": v(160.77, -95.2) * mm});
            skLineSegment(sketch, "E19.4.10.7", {"start": v(160.77, -93.2) * mm, "end": v(160.77, -47.2) * mm});
            skArc(sketch, "E19.7.10.7", {"start": v(160.77, -93.2) * mm, "mid": v(161.35, -94.62) * mm, "end": v(162.77, -95.2) * mm});
            skPoint(sketch, "E19.11.10.7", {"position": v(170.77, -95.2) * mm});
            skPoint(sketch, "E19.12.10.7", {"position": v(160.77, -45.2) * mm});
            skLineSegment(sketch, "E19.13.10.7", {"start": v(162.77, -45.2) * mm, "end": v(168.77, -45.2) * mm});
            skLineSegment(sketch, "E19.16.10.7", {"start": v(162.77, -95.2) * mm, "end": v(168.77, -95.2) * mm});
            skPoint(sketch, "E19.19.10.7", {"position": v(170.77, -45.2) * mm});
            skArc(sketch, "E19.20.10.7", {"start": v(170.77, -47.2) * mm, "mid": v(170.18, -45.8) * mm, "end": v(168.77, -45.2) * mm});
            skArc(sketch, "E19.24.10.7", {"start": v(168.77, -95.2) * mm, "mid": v(170.18, -94.62) * mm, "end": v(170.77, -93.2) * mm});
            skArc(sketch, "E19.28.10.7", {"start": v(162.77, -45.2) * mm, "mid": v(161.35, -45.8) * mm, "end": v(160.77, -47.2) * mm});
            skLineSegment(sketch, "E19.0.11.6", {"start": v(186.27, -153.2) * mm, "end": v(186.27, -107.2) * mm});
            skPoint(sketch, "E19.3.11.6", {"position": v(176.27, -155.2) * mm});
            skLineSegment(sketch, "E19.4.11.6", {"start": v(176.27, -153.2) * mm, "end": v(176.27, -107.2) * mm});
            skArc(sketch, "E19.7.11.6", {"start": v(176.27, -153.2) * mm, "mid": v(176.85, -154.62) * mm, "end": v(178.27, -155.2) * mm});
            skPoint(sketch, "E19.11.11.6", {"position": v(186.27, -155.2) * mm});
            skPoint(sketch, "E19.12.11.6", {"position": v(176.27, -105.2) * mm});
            skLineSegment(sketch, "E19.13.11.6", {"start": v(178.27, -105.2) * mm, "end": v(184.27, -105.2) * mm});
            skLineSegment(sketch, "E19.16.11.6", {"start": v(178.27, -155.2) * mm, "end": v(184.27, -155.2) * mm});
            skPoint(sketch, "E19.19.11.6", {"position": v(186.27, -105.2) * mm});
            skArc(sketch, "E19.20.11.6", {"start": v(186.27, -107.2) * mm, "mid": v(185.68, -105.8) * mm, "end": v(184.27, -105.2) * mm});
            skArc(sketch, "E19.24.11.6", {"start": v(184.27, -155.2) * mm, "mid": v(185.68, -154.62) * mm, "end": v(186.27, -153.2) * mm});
            skArc(sketch, "E19.28.11.6", {"start": v(178.27, -105.2) * mm, "mid": v(176.85, -105.8) * mm, "end": v(176.27, -107.2) * mm});
            skLineSegment(sketch, "E19.0.11.7", {"start": v(186.27, -93.2) * mm, "end": v(186.27, -47.2) * mm});
            skPoint(sketch, "E19.3.11.7", {"position": v(176.27, -95.2) * mm});
            skLineSegment(sketch, "E19.4.11.7", {"start": v(176.27, -93.2) * mm, "end": v(176.27, -47.2) * mm});
            skArc(sketch, "E19.7.11.7", {"start": v(176.27, -93.2) * mm, "mid": v(176.85, -94.62) * mm, "end": v(178.27, -95.2) * mm});
            skPoint(sketch, "E19.11.11.7", {"position": v(186.27, -95.2) * mm});
            skPoint(sketch, "E19.12.11.7", {"position": v(176.27, -45.2) * mm});
            skLineSegment(sketch, "E19.13.11.7", {"start": v(178.27, -45.2) * mm, "end": v(184.27, -45.2) * mm});
            skLineSegment(sketch, "E19.16.11.7", {"start": v(178.27, -95.2) * mm, "end": v(184.27, -95.2) * mm});
            skPoint(sketch, "E19.19.11.7", {"position": v(186.27, -45.2) * mm});
            skArc(sketch, "E19.20.11.7", {"start": v(186.27, -47.2) * mm, "mid": v(185.68, -45.8) * mm, "end": v(184.27, -45.2) * mm});
            skArc(sketch, "E19.24.11.7", {"start": v(184.27, -95.2) * mm, "mid": v(185.68, -94.62) * mm, "end": v(186.27, -93.2) * mm});
            skArc(sketch, "E19.28.11.7", {"start": v(178.27, -45.2) * mm, "mid": v(176.85, -45.8) * mm, "end": v(176.27, -47.2) * mm});
            skLineSegment(sketch, "E19.0.12.6", {"start": v(201.77, -153.2) * mm, "end": v(201.77, -107.2) * mm});
            skPoint(sketch, "E19.3.12.6", {"position": v(191.77, -155.2) * mm});
            skLineSegment(sketch, "E19.4.12.6", {"start": v(191.77, -153.2) * mm, "end": v(191.77, -107.2) * mm});
            skArc(sketch, "E19.7.12.6", {"start": v(191.77, -153.2) * mm, "mid": v(192.35, -154.62) * mm, "end": v(193.77, -155.2) * mm});
            skPoint(sketch, "E19.11.12.6", {"position": v(201.77, -155.2) * mm});
            skPoint(sketch, "E19.12.12.6", {"position": v(191.77, -105.2) * mm});
            skLineSegment(sketch, "E19.13.12.6", {"start": v(193.77, -105.2) * mm, "end": v(199.77, -105.2) * mm});
            skLineSegment(sketch, "E19.16.12.6", {"start": v(193.77, -155.2) * mm, "end": v(199.77, -155.2) * mm});
            skPoint(sketch, "E19.19.12.6", {"position": v(201.77, -105.2) * mm});
            skArc(sketch, "E19.20.12.6", {"start": v(201.77, -107.2) * mm, "mid": v(201.18, -105.8) * mm, "end": v(199.77, -105.2) * mm});
            skArc(sketch, "E19.24.12.6", {"start": v(199.77, -155.2) * mm, "mid": v(201.18, -154.62) * mm, "end": v(201.77, -153.2) * mm});
            skArc(sketch, "E19.28.12.6", {"start": v(193.77, -105.2) * mm, "mid": v(192.35, -105.8) * mm, "end": v(191.77, -107.2) * mm});
            skLineSegment(sketch, "E19.0.12.7", {"start": v(201.77, -93.2) * mm, "end": v(201.77, -47.2) * mm});
            skPoint(sketch, "E19.3.12.7", {"position": v(191.77, -95.2) * mm});
            skLineSegment(sketch, "E19.4.12.7", {"start": v(191.77, -93.2) * mm, "end": v(191.77, -47.2) * mm});
            skArc(sketch, "E19.7.12.7", {"start": v(191.77, -93.2) * mm, "mid": v(192.35, -94.62) * mm, "end": v(193.77, -95.2) * mm});
            skPoint(sketch, "E19.11.12.7", {"position": v(201.77, -95.2) * mm});
            skPoint(sketch, "E19.12.12.7", {"position": v(191.77, -45.2) * mm});
            skLineSegment(sketch, "E19.13.12.7", {"start": v(193.77, -45.2) * mm, "end": v(199.77, -45.2) * mm});
            skLineSegment(sketch, "E19.16.12.7", {"start": v(193.77, -95.2) * mm, "end": v(199.77, -95.2) * mm});
            skPoint(sketch, "E19.19.12.7", {"position": v(201.77, -45.2) * mm});
            skArc(sketch, "E19.20.12.7", {"start": v(201.77, -47.2) * mm, "mid": v(201.18, -45.8) * mm, "end": v(199.77, -45.2) * mm});
            skArc(sketch, "E19.24.12.7", {"start": v(199.77, -95.2) * mm, "mid": v(201.18, -94.62) * mm, "end": v(201.77, -93.2) * mm});
            skArc(sketch, "E19.28.12.7", {"start": v(193.77, -45.2) * mm, "mid": v(192.35, -45.8) * mm, "end": v(191.77, -47.2) * mm});
            skLineSegment(sketch, "E19.0.13.6", {"start": v(217.27, -153.2) * mm, "end": v(217.27, -107.2) * mm});
            skPoint(sketch, "E19.3.13.6", {"position": v(207.27, -155.2) * mm});
            skLineSegment(sketch, "E19.4.13.6", {"start": v(207.27, -153.2) * mm, "end": v(207.27, -107.2) * mm});
            skArc(sketch, "E19.7.13.6", {"start": v(207.27, -153.2) * mm, "mid": v(207.85, -154.62) * mm, "end": v(209.27, -155.2) * mm});
            skPoint(sketch, "E19.11.13.6", {"position": v(217.27, -155.2) * mm});
            skPoint(sketch, "E19.12.13.6", {"position": v(207.27, -105.2) * mm});
            skLineSegment(sketch, "E19.13.13.6", {"start": v(209.27, -105.2) * mm, "end": v(215.27, -105.2) * mm});
            skLineSegment(sketch, "E19.16.13.6", {"start": v(209.27, -155.2) * mm, "end": v(215.27, -155.2) * mm});
            skPoint(sketch, "E19.19.13.6", {"position": v(217.27, -105.2) * mm});
            skArc(sketch, "E19.20.13.6", {"start": v(217.27, -107.2) * mm, "mid": v(216.68, -105.8) * mm, "end": v(215.27, -105.2) * mm});
            skArc(sketch, "E19.24.13.6", {"start": v(215.27, -155.2) * mm, "mid": v(216.68, -154.62) * mm, "end": v(217.27, -153.2) * mm});
            skArc(sketch, "E19.28.13.6", {"start": v(209.27, -105.2) * mm, "mid": v(207.85, -105.8) * mm, "end": v(207.27, -107.2) * mm});
            skLineSegment(sketch, "E19.0.13.7", {"start": v(217.27, -93.2) * mm, "end": v(217.27, -47.2) * mm});
            skPoint(sketch, "E19.3.13.7", {"position": v(207.27, -95.2) * mm});
            skLineSegment(sketch, "E19.4.13.7", {"start": v(207.27, -93.2) * mm, "end": v(207.27, -47.2) * mm});
            skArc(sketch, "E19.7.13.7", {"start": v(207.27, -93.2) * mm, "mid": v(207.85, -94.62) * mm, "end": v(209.27, -95.2) * mm});
            skPoint(sketch, "E19.11.13.7", {"position": v(217.27, -95.2) * mm});
            skPoint(sketch, "E19.12.13.7", {"position": v(207.27, -45.2) * mm});
            skLineSegment(sketch, "E19.13.13.7", {"start": v(209.27, -45.2) * mm, "end": v(215.27, -45.2) * mm});
            skLineSegment(sketch, "E19.16.13.7", {"start": v(209.27, -95.2) * mm, "end": v(215.27, -95.2) * mm});
            skPoint(sketch, "E19.19.13.7", {"position": v(217.27, -45.2) * mm});
            skArc(sketch, "E19.20.13.7", {"start": v(217.27, -47.2) * mm, "mid": v(216.68, -45.8) * mm, "end": v(215.27, -45.2) * mm});
            skArc(sketch, "E19.24.13.7", {"start": v(215.27, -95.2) * mm, "mid": v(216.68, -94.62) * mm, "end": v(217.27, -93.2) * mm});
            skArc(sketch, "E19.28.13.7", {"start": v(209.27, -45.2) * mm, "mid": v(207.85, -45.8) * mm, "end": v(207.27, -47.2) * mm});
            skLineSegment(sketch, "E19.0.14.6", {"start": v(232.77, -153.2) * mm, "end": v(232.77, -107.2) * mm});
            skPoint(sketch, "E19.3.14.6", {"position": v(222.77, -155.2) * mm});
            skLineSegment(sketch, "E19.4.14.6", {"start": v(222.77, -153.2) * mm, "end": v(222.77, -107.2) * mm});
            skArc(sketch, "E19.7.14.6", {"start": v(222.77, -153.2) * mm, "mid": v(223.35, -154.62) * mm, "end": v(224.77, -155.2) * mm});
            skPoint(sketch, "E19.11.14.6", {"position": v(232.77, -155.2) * mm});
            skPoint(sketch, "E19.12.14.6", {"position": v(222.77, -105.2) * mm});
            skLineSegment(sketch, "E19.13.14.6", {"start": v(224.77, -105.2) * mm, "end": v(230.77, -105.2) * mm});
            skLineSegment(sketch, "E19.16.14.6", {"start": v(224.77, -155.2) * mm, "end": v(230.77, -155.2) * mm});
            skPoint(sketch, "E19.19.14.6", {"position": v(232.77, -105.2) * mm});
            skArc(sketch, "E19.20.14.6", {"start": v(232.77, -107.2) * mm, "mid": v(232.18, -105.8) * mm, "end": v(230.77, -105.2) * mm});
            skArc(sketch, "E19.24.14.6", {"start": v(230.77, -155.2) * mm, "mid": v(232.18, -154.62) * mm, "end": v(232.77, -153.2) * mm});
            skArc(sketch, "E19.28.14.6", {"start": v(224.77, -105.2) * mm, "mid": v(223.35, -105.8) * mm, "end": v(222.77, -107.2) * mm});
            skLineSegment(sketch, "E19.0.14.7", {"start": v(232.77, -93.2) * mm, "end": v(232.77, -47.2) * mm});
            skPoint(sketch, "E19.3.14.7", {"position": v(222.77, -95.2) * mm});
            skLineSegment(sketch, "E19.4.14.7", {"start": v(222.77, -93.2) * mm, "end": v(222.77, -47.2) * mm});
            skArc(sketch, "E19.7.14.7", {"start": v(222.77, -93.2) * mm, "mid": v(223.35, -94.62) * mm, "end": v(224.77, -95.2) * mm});
            skPoint(sketch, "E19.11.14.7", {"position": v(232.77, -95.2) * mm});
            skPoint(sketch, "E19.12.14.7", {"position": v(222.77, -45.2) * mm});
            skLineSegment(sketch, "E19.13.14.7", {"start": v(224.77, -45.2) * mm, "end": v(230.77, -45.2) * mm});
            skLineSegment(sketch, "E19.16.14.7", {"start": v(224.77, -95.2) * mm, "end": v(230.77, -95.2) * mm});
            skPoint(sketch, "E19.19.14.7", {"position": v(232.77, -45.2) * mm});
            skArc(sketch, "E19.20.14.7", {"start": v(232.77, -47.2) * mm, "mid": v(232.18, -45.8) * mm, "end": v(230.77, -45.2) * mm});
            skArc(sketch, "E19.24.14.7", {"start": v(230.77, -95.2) * mm, "mid": v(232.18, -94.62) * mm, "end": v(232.77, -93.2) * mm});
            skArc(sketch, "E19.28.14.7", {"start": v(224.77, -45.2) * mm, "mid": v(223.35, -45.8) * mm, "end": v(222.77, -47.2) * mm});
            skLineSegment(sketch, "E19.0.15.6", {"start": v(248.27, -153.2) * mm, "end": v(248.27, -107.2) * mm});
            skPoint(sketch, "E19.3.15.6", {"position": v(238.27, -155.2) * mm});
            skLineSegment(sketch, "E19.4.15.6", {"start": v(238.27, -153.2) * mm, "end": v(238.27, -107.2) * mm});
            skArc(sketch, "E19.7.15.6", {"start": v(238.27, -153.2) * mm, "mid": v(238.85, -154.62) * mm, "end": v(240.27, -155.2) * mm});
            skPoint(sketch, "E19.11.15.6", {"position": v(248.27, -155.2) * mm});
            skPoint(sketch, "E19.12.15.6", {"position": v(238.27, -105.2) * mm});
            skLineSegment(sketch, "E19.13.15.6", {"start": v(240.27, -105.2) * mm, "end": v(246.27, -105.2) * mm});
            skLineSegment(sketch, "E19.16.15.6", {"start": v(240.27, -155.2) * mm, "end": v(246.27, -155.2) * mm});
            skPoint(sketch, "E19.19.15.6", {"position": v(248.27, -105.2) * mm});
            skArc(sketch, "E19.20.15.6", {"start": v(248.27, -107.2) * mm, "mid": v(247.68, -105.8) * mm, "end": v(246.27, -105.2) * mm});
            skArc(sketch, "E19.24.15.6", {"start": v(246.27, -155.2) * mm, "mid": v(247.68, -154.62) * mm, "end": v(248.27, -153.2) * mm});
            skArc(sketch, "E19.28.15.6", {"start": v(240.27, -105.2) * mm, "mid": v(238.85, -105.8) * mm, "end": v(238.27, -107.2) * mm});
            skLineSegment(sketch, "E19.0.15.7", {"start": v(248.27, -93.2) * mm, "end": v(248.27, -47.2) * mm});
            skPoint(sketch, "E19.3.15.7", {"position": v(238.27, -95.2) * mm});
            skLineSegment(sketch, "E19.4.15.7", {"start": v(238.27, -93.2) * mm, "end": v(238.27, -47.2) * mm});
            skArc(sketch, "E19.7.15.7", {"start": v(238.27, -93.2) * mm, "mid": v(238.85, -94.62) * mm, "end": v(240.27, -95.2) * mm});
            skPoint(sketch, "E19.11.15.7", {"position": v(248.27, -95.2) * mm});
            skPoint(sketch, "E19.12.15.7", {"position": v(238.27, -45.2) * mm});
            skLineSegment(sketch, "E19.13.15.7", {"start": v(240.27, -45.2) * mm, "end": v(246.27, -45.2) * mm});
            skLineSegment(sketch, "E19.16.15.7", {"start": v(240.27, -95.2) * mm, "end": v(246.27, -95.2) * mm});
            skPoint(sketch, "E19.19.15.7", {"position": v(248.27, -45.2) * mm});
            skArc(sketch, "E19.20.15.7", {"start": v(248.27, -47.2) * mm, "mid": v(247.68, -45.8) * mm, "end": v(246.27, -45.2) * mm});
            skArc(sketch, "E19.24.15.7", {"start": v(246.27, -95.2) * mm, "mid": v(247.68, -94.62) * mm, "end": v(248.27, -93.2) * mm});
            skArc(sketch, "E19.28.15.7", {"start": v(240.27, -45.2) * mm, "mid": v(238.85, -45.8) * mm, "end": v(238.27, -47.2) * mm});
            skLineSegment(sketch, "E19.0.16.6", {"start": v(263.77, -153.2) * mm, "end": v(263.77, -107.2) * mm});
            skPoint(sketch, "E19.3.16.6", {"position": v(253.77, -155.2) * mm});
            skLineSegment(sketch, "E19.4.16.6", {"start": v(253.77, -153.2) * mm, "end": v(253.77, -107.2) * mm});
            skArc(sketch, "E19.7.16.6", {"start": v(253.77, -153.2) * mm, "mid": v(254.35, -154.62) * mm, "end": v(255.77, -155.2) * mm});
            skPoint(sketch, "E19.11.16.6", {"position": v(263.77, -155.2) * mm});
            skPoint(sketch, "E19.12.16.6", {"position": v(253.77, -105.2) * mm});
            skLineSegment(sketch, "E19.13.16.6", {"start": v(255.77, -105.2) * mm, "end": v(261.77, -105.2) * mm});
            skLineSegment(sketch, "E19.16.16.6", {"start": v(255.77, -155.2) * mm, "end": v(261.77, -155.2) * mm});
            skPoint(sketch, "E19.19.16.6", {"position": v(263.77, -105.2) * mm});
            skArc(sketch, "E19.20.16.6", {"start": v(263.77, -107.2) * mm, "mid": v(263.18, -105.8) * mm, "end": v(261.77, -105.2) * mm});
            skArc(sketch, "E19.24.16.6", {"start": v(261.77, -155.2) * mm, "mid": v(263.18, -154.62) * mm, "end": v(263.77, -153.2) * mm});
            skArc(sketch, "E19.28.16.6", {"start": v(255.77, -105.2) * mm, "mid": v(254.35, -105.8) * mm, "end": v(253.77, -107.2) * mm});
            skLineSegment(sketch, "E19.0.16.7", {"start": v(263.77, -93.2) * mm, "end": v(263.77, -47.2) * mm});
            skPoint(sketch, "E19.3.16.7", {"position": v(253.77, -95.2) * mm});
            skLineSegment(sketch, "E19.4.16.7", {"start": v(253.77, -93.2) * mm, "end": v(253.77, -47.2) * mm});
            skArc(sketch, "E19.7.16.7", {"start": v(253.77, -93.2) * mm, "mid": v(254.35, -94.62) * mm, "end": v(255.77, -95.2) * mm});
            skPoint(sketch, "E19.11.16.7", {"position": v(263.77, -95.2) * mm});
            skPoint(sketch, "E19.12.16.7", {"position": v(253.77, -45.2) * mm});
            skLineSegment(sketch, "E19.13.16.7", {"start": v(255.77, -45.2) * mm, "end": v(261.77, -45.2) * mm});
            skLineSegment(sketch, "E19.16.16.7", {"start": v(255.77, -95.2) * mm, "end": v(261.77, -95.2) * mm});
            skPoint(sketch, "E19.19.16.7", {"position": v(263.77, -45.2) * mm});
            skArc(sketch, "E19.20.16.7", {"start": v(263.77, -47.2) * mm, "mid": v(263.18, -45.8) * mm, "end": v(261.77, -45.2) * mm});
            skArc(sketch, "E19.24.16.7", {"start": v(261.77, -95.2) * mm, "mid": v(263.18, -94.62) * mm, "end": v(263.77, -93.2) * mm});
            skArc(sketch, "E19.28.16.7", {"start": v(255.77, -45.2) * mm, "mid": v(254.35, -45.8) * mm, "end": v(253.77, -47.2) * mm});
            skLineSegment(sketch, "E19.0.17.6", {"start": v(279.27, -153.2) * mm, "end": v(279.27, -107.2) * mm});
            skPoint(sketch, "E19.3.17.6", {"position": v(269.27, -155.2) * mm});
            skLineSegment(sketch, "E19.4.17.6", {"start": v(269.27, -153.2) * mm, "end": v(269.27, -107.2) * mm});
            skArc(sketch, "E19.7.17.6", {"start": v(269.27, -153.2) * mm, "mid": v(269.85, -154.62) * mm, "end": v(271.27, -155.2) * mm});
            skPoint(sketch, "E19.11.17.6", {"position": v(279.27, -155.2) * mm});
            skPoint(sketch, "E19.12.17.6", {"position": v(269.27, -105.2) * mm});
            skLineSegment(sketch, "E19.13.17.6", {"start": v(271.27, -105.2) * mm, "end": v(277.27, -105.2) * mm});
            skLineSegment(sketch, "E19.16.17.6", {"start": v(271.27, -155.2) * mm, "end": v(277.27, -155.2) * mm});
            skPoint(sketch, "E19.19.17.6", {"position": v(279.27, -105.2) * mm});
            skArc(sketch, "E19.20.17.6", {"start": v(279.27, -107.2) * mm, "mid": v(278.68, -105.8) * mm, "end": v(277.27, -105.2) * mm});
            skArc(sketch, "E19.24.17.6", {"start": v(277.27, -155.2) * mm, "mid": v(278.68, -154.62) * mm, "end": v(279.27, -153.2) * mm});
            skArc(sketch, "E19.28.17.6", {"start": v(271.27, -105.2) * mm, "mid": v(269.85, -105.8) * mm, "end": v(269.27, -107.2) * mm});
            skLineSegment(sketch, "E19.0.17.7", {"start": v(279.27, -93.2) * mm, "end": v(279.27, -47.2) * mm});
            skPoint(sketch, "E19.3.17.7", {"position": v(269.27, -95.2) * mm});
            skLineSegment(sketch, "E19.4.17.7", {"start": v(269.27, -93.2) * mm, "end": v(269.27, -47.2) * mm});
            skArc(sketch, "E19.7.17.7", {"start": v(269.27, -93.2) * mm, "mid": v(269.85, -94.62) * mm, "end": v(271.27, -95.2) * mm});
            skPoint(sketch, "E19.11.17.7", {"position": v(279.27, -95.2) * mm});
            skPoint(sketch, "E19.12.17.7", {"position": v(269.27, -45.2) * mm});
            skLineSegment(sketch, "E19.13.17.7", {"start": v(271.27, -45.2) * mm, "end": v(277.27, -45.2) * mm});
            skLineSegment(sketch, "E19.16.17.7", {"start": v(271.27, -95.2) * mm, "end": v(277.27, -95.2) * mm});
            skPoint(sketch, "E19.19.17.7", {"position": v(279.27, -45.2) * mm});
            skArc(sketch, "E19.20.17.7", {"start": v(279.27, -47.2) * mm, "mid": v(278.68, -45.8) * mm, "end": v(277.27, -45.2) * mm});
            skArc(sketch, "E19.24.17.7", {"start": v(277.27, -95.2) * mm, "mid": v(278.68, -94.62) * mm, "end": v(279.27, -93.2) * mm});
            skArc(sketch, "E19.28.17.7", {"start": v(271.27, -45.2) * mm, "mid": v(269.85, -45.8) * mm, "end": v(269.27, -47.2) * mm});
            skPoint(sketch, "E19.3.18.6", {"position": v(284.77, -155.2) * mm});
            skPoint(sketch, "E19.11.18.6", {"position": v(294.77, -155.2) * mm});
            skPoint(sketch, "E19.12.18.6", {"position": v(284.77, -105.2) * mm});
            skPoint(sketch, "E19.19.18.6", {"position": v(294.77, -105.2) * mm});
            skPoint(sketch, "E19.3.18.7", {"position": v(284.77, -95.2) * mm});
            skPoint(sketch, "E19.11.18.7", {"position": v(294.77, -95.2) * mm});
            skPoint(sketch, "E19.12.18.7", {"position": v(284.77, -45.2) * mm});
            skPoint(sketch, "E19.19.18.7", {"position": v(294.77, -45.2) * mm});
            skPoint(sketch, "E20.3.0.8", {"position": v(5.77, -35.2) * mm});
            skPoint(sketch, "E20.11.0.8", {"position": v(15.77, -35.2) * mm});
            skPoint(sketch, "E20.12.0.8", {"position": v(5.77, 14.8) * mm});
            skPoint(sketch, "E20.19.0.8", {"position": v(15.77, 14.8) * mm});
            skLineSegment(sketch, "E20.0.1.8", {"start": v(31.27, -33.2) * mm, "end": v(31.27, 12.8) * mm});
            skPoint(sketch, "E20.3.1.8", {"position": v(21.27, -35.2) * mm});
            skLineSegment(sketch, "E20.4.1.8", {"start": v(21.27, -33.2) * mm, "end": v(21.27, 12.8) * mm});
            skArc(sketch, "E20.7.1.8", {"start": v(21.27, -33.2) * mm, "mid": v(21.85, -34.62) * mm, "end": v(23.27, -35.2) * mm});
            skPoint(sketch, "E20.11.1.8", {"position": v(31.27, -35.2) * mm});
            skPoint(sketch, "E20.12.1.8", {"position": v(21.27, 14.8) * mm});
            skLineSegment(sketch, "E20.13.1.8", {"start": v(23.27, 14.8) * mm, "end": v(29.27, 14.8) * mm});
            skLineSegment(sketch, "E20.16.1.8", {"start": v(23.27, -35.2) * mm, "end": v(29.27, -35.2) * mm});
            skPoint(sketch, "E20.19.1.8", {"position": v(31.27, 14.8) * mm});
            skArc(sketch, "E20.20.1.8", {"start": v(31.27, 12.8) * mm, "mid": v(30.68, 14.2) * mm, "end": v(29.27, 14.8) * mm});
            skArc(sketch, "E20.24.1.8", {"start": v(29.27, -35.2) * mm, "mid": v(30.68, -34.62) * mm, "end": v(31.27, -33.2) * mm});
            skArc(sketch, "E20.28.1.8", {"start": v(23.27, 14.8) * mm, "mid": v(21.85, 14.2) * mm, "end": v(21.27, 12.8) * mm});
            skLineSegment(sketch, "E20.0.2.8", {"start": v(46.77, -33.2) * mm, "end": v(46.77, 12.8) * mm});
            skPoint(sketch, "E20.3.2.8", {"position": v(36.77, -35.2) * mm});
            skLineSegment(sketch, "E20.4.2.8", {"start": v(36.77, -33.2) * mm, "end": v(36.77, 12.8) * mm});
            skArc(sketch, "E20.7.2.8", {"start": v(36.77, -33.2) * mm, "mid": v(37.35, -34.62) * mm, "end": v(38.77, -35.2) * mm});
            skPoint(sketch, "E20.11.2.8", {"position": v(46.77, -35.2) * mm});
            skPoint(sketch, "E20.12.2.8", {"position": v(36.77, 14.8) * mm});
            skLineSegment(sketch, "E20.13.2.8", {"start": v(38.77, 14.8) * mm, "end": v(44.77, 14.8) * mm});
            skLineSegment(sketch, "E20.16.2.8", {"start": v(38.77, -35.2) * mm, "end": v(44.77, -35.2) * mm});
            skPoint(sketch, "E20.19.2.8", {"position": v(46.77, 14.8) * mm});
            skArc(sketch, "E20.20.2.8", {"start": v(46.77, 12.8) * mm, "mid": v(46.18, 14.2) * mm, "end": v(44.77, 14.8) * mm});
            skArc(sketch, "E20.24.2.8", {"start": v(44.77, -35.2) * mm, "mid": v(46.18, -34.62) * mm, "end": v(46.77, -33.2) * mm});
            skArc(sketch, "E20.28.2.8", {"start": v(38.77, 14.8) * mm, "mid": v(37.35, 14.2) * mm, "end": v(36.77, 12.8) * mm});
            skLineSegment(sketch, "E20.0.3.8", {"start": v(62.27, -33.2) * mm, "end": v(62.27, 12.8) * mm});
            skPoint(sketch, "E20.3.3.8", {"position": v(52.27, -35.2) * mm});
            skLineSegment(sketch, "E20.4.3.8", {"start": v(52.27, -33.2) * mm, "end": v(52.27, 12.8) * mm});
            skArc(sketch, "E20.7.3.8", {"start": v(52.27, -33.2) * mm, "mid": v(52.85, -34.62) * mm, "end": v(54.27, -35.2) * mm});
            skPoint(sketch, "E20.11.3.8", {"position": v(62.27, -35.2) * mm});
            skPoint(sketch, "E20.12.3.8", {"position": v(52.27, 14.8) * mm});
            skLineSegment(sketch, "E20.13.3.8", {"start": v(54.27, 14.8) * mm, "end": v(60.27, 14.8) * mm});
            skLineSegment(sketch, "E20.16.3.8", {"start": v(54.27, -35.2) * mm, "end": v(60.27, -35.2) * mm});
            skPoint(sketch, "E20.19.3.8", {"position": v(62.27, 14.8) * mm});
            skArc(sketch, "E20.20.3.8", {"start": v(62.27, 12.8) * mm, "mid": v(61.68, 14.2) * mm, "end": v(60.27, 14.8) * mm});
            skArc(sketch, "E20.24.3.8", {"start": v(60.27, -35.2) * mm, "mid": v(61.68, -34.62) * mm, "end": v(62.27, -33.2) * mm});
            skArc(sketch, "E20.28.3.8", {"start": v(54.27, 14.8) * mm, "mid": v(52.85, 14.2) * mm, "end": v(52.27, 12.8) * mm});
            skLineSegment(sketch, "E20.0.4.8", {"start": v(77.77, -33.2) * mm, "end": v(77.77, 12.8) * mm});
            skPoint(sketch, "E20.3.4.8", {"position": v(67.77, -35.2) * mm});
            skLineSegment(sketch, "E20.4.4.8", {"start": v(67.77, -33.2) * mm, "end": v(67.77, 12.8) * mm});
            skArc(sketch, "E20.7.4.8", {"start": v(67.77, -33.2) * mm, "mid": v(68.35, -34.62) * mm, "end": v(69.77, -35.2) * mm});
            skPoint(sketch, "E20.11.4.8", {"position": v(77.77, -35.2) * mm});
            skPoint(sketch, "E20.12.4.8", {"position": v(67.77, 14.8) * mm});
            skLineSegment(sketch, "E20.13.4.8", {"start": v(69.77, 14.8) * mm, "end": v(75.77, 14.8) * mm});
            skLineSegment(sketch, "E20.16.4.8", {"start": v(69.77, -35.2) * mm, "end": v(75.77, -35.2) * mm});
            skPoint(sketch, "E20.19.4.8", {"position": v(77.77, 14.8) * mm});
            skArc(sketch, "E20.20.4.8", {"start": v(77.77, 12.8) * mm, "mid": v(77.18, 14.2) * mm, "end": v(75.77, 14.8) * mm});
            skArc(sketch, "E20.24.4.8", {"start": v(75.77, -35.2) * mm, "mid": v(77.18, -34.62) * mm, "end": v(77.77, -33.2) * mm});
            skArc(sketch, "E20.28.4.8", {"start": v(69.77, 14.8) * mm, "mid": v(68.35, 14.2) * mm, "end": v(67.77, 12.8) * mm});
            skLineSegment(sketch, "E20.0.5.8", {"start": v(93.27, -33.2) * mm, "end": v(93.27, 12.8) * mm});
            skPoint(sketch, "E20.3.5.8", {"position": v(83.27, -35.2) * mm});
            skLineSegment(sketch, "E20.4.5.8", {"start": v(83.27, -33.2) * mm, "end": v(83.27, 12.8) * mm});
            skArc(sketch, "E20.7.5.8", {"start": v(83.27, -33.2) * mm, "mid": v(83.85, -34.62) * mm, "end": v(85.27, -35.2) * mm});
            skPoint(sketch, "E20.11.5.8", {"position": v(93.27, -35.2) * mm});
            skPoint(sketch, "E20.12.5.8", {"position": v(83.27, 14.8) * mm});
            skLineSegment(sketch, "E20.13.5.8", {"start": v(85.27, 14.8) * mm, "end": v(91.27, 14.8) * mm});
            skLineSegment(sketch, "E20.16.5.8", {"start": v(85.27, -35.2) * mm, "end": v(91.27, -35.2) * mm});
            skPoint(sketch, "E20.19.5.8", {"position": v(93.27, 14.8) * mm});
            skArc(sketch, "E20.20.5.8", {"start": v(93.27, 12.8) * mm, "mid": v(92.68, 14.2) * mm, "end": v(91.27, 14.8) * mm});
            skArc(sketch, "E20.24.5.8", {"start": v(91.27, -35.2) * mm, "mid": v(92.68, -34.62) * mm, "end": v(93.27, -33.2) * mm});
            skArc(sketch, "E20.28.5.8", {"start": v(85.27, 14.8) * mm, "mid": v(83.85, 14.2) * mm, "end": v(83.27, 12.8) * mm});
            skLineSegment(sketch, "E20.0.6.8", {"start": v(108.77, -33.2) * mm, "end": v(108.77, 12.8) * mm});
            skPoint(sketch, "E20.3.6.8", {"position": v(98.77, -35.2) * mm});
            skLineSegment(sketch, "E20.4.6.8", {"start": v(98.77, -33.2) * mm, "end": v(98.77, 12.8) * mm});
            skArc(sketch, "E20.7.6.8", {"start": v(98.77, -33.2) * mm, "mid": v(99.35, -34.62) * mm, "end": v(100.77, -35.2) * mm});
            skPoint(sketch, "E20.11.6.8", {"position": v(108.77, -35.2) * mm});
            skPoint(sketch, "E20.12.6.8", {"position": v(98.77, 14.8) * mm});
            skLineSegment(sketch, "E20.13.6.8", {"start": v(100.77, 14.8) * mm, "end": v(106.77, 14.8) * mm});
            skLineSegment(sketch, "E20.16.6.8", {"start": v(100.77, -35.2) * mm, "end": v(106.77, -35.2) * mm});
            skPoint(sketch, "E20.19.6.8", {"position": v(108.77, 14.8) * mm});
            skArc(sketch, "E20.20.6.8", {"start": v(108.77, 12.8) * mm, "mid": v(108.18, 14.2) * mm, "end": v(106.77, 14.8) * mm});
            skArc(sketch, "E20.24.6.8", {"start": v(106.77, -35.2) * mm, "mid": v(108.18, -34.62) * mm, "end": v(108.77, -33.2) * mm});
            skArc(sketch, "E20.28.6.8", {"start": v(100.77, 14.8) * mm, "mid": v(99.35, 14.2) * mm, "end": v(98.77, 12.8) * mm});
            skLineSegment(sketch, "E20.0.7.8", {"start": v(124.27, -33.2) * mm, "end": v(124.27, 12.8) * mm});
            skPoint(sketch, "E20.3.7.8", {"position": v(114.27, -35.2) * mm});
            skLineSegment(sketch, "E20.4.7.8", {"start": v(114.27, -33.2) * mm, "end": v(114.27, 12.8) * mm});
            skArc(sketch, "E20.7.7.8", {"start": v(114.27, -33.2) * mm, "mid": v(114.85, -34.62) * mm, "end": v(116.27, -35.2) * mm});
            skPoint(sketch, "E20.11.7.8", {"position": v(124.27, -35.2) * mm});
            skPoint(sketch, "E20.12.7.8", {"position": v(114.27, 14.8) * mm});
            skLineSegment(sketch, "E20.13.7.8", {"start": v(116.27, 14.8) * mm, "end": v(122.27, 14.8) * mm});
            skLineSegment(sketch, "E20.16.7.8", {"start": v(116.27, -35.2) * mm, "end": v(122.27, -35.2) * mm});
            skPoint(sketch, "E20.19.7.8", {"position": v(124.27, 14.8) * mm});
            skArc(sketch, "E20.20.7.8", {"start": v(124.27, 12.8) * mm, "mid": v(123.68, 14.2) * mm, "end": v(122.27, 14.8) * mm});
            skArc(sketch, "E20.24.7.8", {"start": v(122.27, -35.2) * mm, "mid": v(123.68, -34.62) * mm, "end": v(124.27, -33.2) * mm});
            skArc(sketch, "E20.28.7.8", {"start": v(116.27, 14.8) * mm, "mid": v(114.85, 14.2) * mm, "end": v(114.27, 12.8) * mm});
            skLineSegment(sketch, "E20.0.8.8", {"start": v(139.77, -33.2) * mm, "end": v(139.77, 12.8) * mm});
            skPoint(sketch, "E20.3.8.8", {"position": v(129.77, -35.2) * mm});
            skLineSegment(sketch, "E20.4.8.8", {"start": v(129.77, -33.2) * mm, "end": v(129.77, 12.8) * mm});
            skArc(sketch, "E20.7.8.8", {"start": v(129.77, -33.2) * mm, "mid": v(130.35, -34.62) * mm, "end": v(131.77, -35.2) * mm});
            skPoint(sketch, "E20.11.8.8", {"position": v(139.77, -35.2) * mm});
            skPoint(sketch, "E20.12.8.8", {"position": v(129.77, 14.8) * mm});
            skLineSegment(sketch, "E20.13.8.8", {"start": v(131.77, 14.8) * mm, "end": v(137.77, 14.8) * mm});
            skLineSegment(sketch, "E20.16.8.8", {"start": v(131.77, -35.2) * mm, "end": v(137.77, -35.2) * mm});
            skPoint(sketch, "E20.19.8.8", {"position": v(139.77, 14.8) * mm});
            skArc(sketch, "E20.20.8.8", {"start": v(139.77, 12.8) * mm, "mid": v(139.18, 14.2) * mm, "end": v(137.77, 14.8) * mm});
            skArc(sketch, "E20.24.8.8", {"start": v(137.77, -35.2) * mm, "mid": v(139.18, -34.62) * mm, "end": v(139.77, -33.2) * mm});
            skArc(sketch, "E20.28.8.8", {"start": v(131.77, 14.8) * mm, "mid": v(130.35, 14.2) * mm, "end": v(129.77, 12.8) * mm});
            skLineSegment(sketch, "E20.0.9.8", {"start": v(155.27, -33.2) * mm, "end": v(155.27, 12.8) * mm});
            skPoint(sketch, "E20.3.9.8", {"position": v(145.27, -35.2) * mm});
            skLineSegment(sketch, "E20.4.9.8", {"start": v(145.27, -33.2) * mm, "end": v(145.27, 12.8) * mm});
            skArc(sketch, "E20.7.9.8", {"start": v(145.27, -33.2) * mm, "mid": v(145.85, -34.62) * mm, "end": v(147.27, -35.2) * mm});
            skPoint(sketch, "E20.11.9.8", {"position": v(155.27, -35.2) * mm});
            skPoint(sketch, "E20.12.9.8", {"position": v(145.27, 14.8) * mm});
            skLineSegment(sketch, "E20.13.9.8", {"start": v(147.27, 14.8) * mm, "end": v(153.27, 14.8) * mm});
            skLineSegment(sketch, "E20.16.9.8", {"start": v(147.27, -35.2) * mm, "end": v(153.27, -35.2) * mm});
            skPoint(sketch, "E20.19.9.8", {"position": v(155.27, 14.8) * mm});
            skArc(sketch, "E20.20.9.8", {"start": v(155.27, 12.8) * mm, "mid": v(154.68, 14.2) * mm, "end": v(153.27, 14.8) * mm});
            skArc(sketch, "E20.24.9.8", {"start": v(153.27, -35.2) * mm, "mid": v(154.68, -34.62) * mm, "end": v(155.27, -33.2) * mm});
            skArc(sketch, "E20.28.9.8", {"start": v(147.27, 14.8) * mm, "mid": v(145.85, 14.2) * mm, "end": v(145.27, 12.8) * mm});
            skLineSegment(sketch, "E20.0.10.8", {"start": v(170.77, -33.2) * mm, "end": v(170.77, 12.8) * mm});
            skPoint(sketch, "E20.3.10.8", {"position": v(160.77, -35.2) * mm});
            skLineSegment(sketch, "E20.4.10.8", {"start": v(160.77, -33.2) * mm, "end": v(160.77, 12.8) * mm});
            skArc(sketch, "E20.7.10.8", {"start": v(160.77, -33.2) * mm, "mid": v(161.35, -34.62) * mm, "end": v(162.77, -35.2) * mm});
            skPoint(sketch, "E20.11.10.8", {"position": v(170.77, -35.2) * mm});
            skPoint(sketch, "E20.12.10.8", {"position": v(160.77, 14.8) * mm});
            skLineSegment(sketch, "E20.13.10.8", {"start": v(162.77, 14.8) * mm, "end": v(168.77, 14.8) * mm});
            skLineSegment(sketch, "E20.16.10.8", {"start": v(162.77, -35.2) * mm, "end": v(168.77, -35.2) * mm});
            skPoint(sketch, "E20.19.10.8", {"position": v(170.77, 14.8) * mm});
            skArc(sketch, "E20.20.10.8", {"start": v(170.77, 12.8) * mm, "mid": v(170.18, 14.2) * mm, "end": v(168.77, 14.8) * mm});
            skArc(sketch, "E20.24.10.8", {"start": v(168.77, -35.2) * mm, "mid": v(170.18, -34.62) * mm, "end": v(170.77, -33.2) * mm});
            skArc(sketch, "E20.28.10.8", {"start": v(162.77, 14.8) * mm, "mid": v(161.35, 14.2) * mm, "end": v(160.77, 12.8) * mm});
            skLineSegment(sketch, "E20.0.11.8", {"start": v(186.27, -33.2) * mm, "end": v(186.27, 12.8) * mm});
            skPoint(sketch, "E20.3.11.8", {"position": v(176.27, -35.2) * mm});
            skLineSegment(sketch, "E20.4.11.8", {"start": v(176.27, -33.2) * mm, "end": v(176.27, 12.8) * mm});
            skArc(sketch, "E20.7.11.8", {"start": v(176.27, -33.2) * mm, "mid": v(176.85, -34.62) * mm, "end": v(178.27, -35.2) * mm});
            skPoint(sketch, "E20.11.11.8", {"position": v(186.27, -35.2) * mm});
            skPoint(sketch, "E20.12.11.8", {"position": v(176.27, 14.8) * mm});
            skLineSegment(sketch, "E20.13.11.8", {"start": v(178.27, 14.8) * mm, "end": v(184.27, 14.8) * mm});
            skLineSegment(sketch, "E20.16.11.8", {"start": v(178.27, -35.2) * mm, "end": v(184.27, -35.2) * mm});
            skPoint(sketch, "E20.19.11.8", {"position": v(186.27, 14.8) * mm});
            skArc(sketch, "E20.20.11.8", {"start": v(186.27, 12.8) * mm, "mid": v(185.68, 14.2) * mm, "end": v(184.27, 14.8) * mm});
            skArc(sketch, "E20.24.11.8", {"start": v(184.27, -35.2) * mm, "mid": v(185.68, -34.62) * mm, "end": v(186.27, -33.2) * mm});
            skArc(sketch, "E20.28.11.8", {"start": v(178.27, 14.8) * mm, "mid": v(176.85, 14.2) * mm, "end": v(176.27, 12.8) * mm});
            skLineSegment(sketch, "E20.0.12.8", {"start": v(201.77, -33.2) * mm, "end": v(201.77, 12.8) * mm});
            skPoint(sketch, "E20.3.12.8", {"position": v(191.77, -35.2) * mm});
            skLineSegment(sketch, "E20.4.12.8", {"start": v(191.77, -33.2) * mm, "end": v(191.77, 12.8) * mm});
            skArc(sketch, "E20.7.12.8", {"start": v(191.77, -33.2) * mm, "mid": v(192.35, -34.62) * mm, "end": v(193.77, -35.2) * mm});
            skPoint(sketch, "E20.11.12.8", {"position": v(201.77, -35.2) * mm});
            skPoint(sketch, "E20.12.12.8", {"position": v(191.77, 14.8) * mm});
            skLineSegment(sketch, "E20.13.12.8", {"start": v(193.77, 14.8) * mm, "end": v(199.77, 14.8) * mm});
            skLineSegment(sketch, "E20.16.12.8", {"start": v(193.77, -35.2) * mm, "end": v(199.77, -35.2) * mm});
            skPoint(sketch, "E20.19.12.8", {"position": v(201.77, 14.8) * mm});
            skArc(sketch, "E20.20.12.8", {"start": v(201.77, 12.8) * mm, "mid": v(201.18, 14.2) * mm, "end": v(199.77, 14.8) * mm});
            skArc(sketch, "E20.24.12.8", {"start": v(199.77, -35.2) * mm, "mid": v(201.18, -34.62) * mm, "end": v(201.77, -33.2) * mm});
            skArc(sketch, "E20.28.12.8", {"start": v(193.77, 14.8) * mm, "mid": v(192.35, 14.2) * mm, "end": v(191.77, 12.8) * mm});
            skLineSegment(sketch, "E20.0.13.8", {"start": v(217.27, -33.2) * mm, "end": v(217.27, 12.8) * mm});
            skPoint(sketch, "E20.3.13.8", {"position": v(207.27, -35.2) * mm});
            skLineSegment(sketch, "E20.4.13.8", {"start": v(207.27, -33.2) * mm, "end": v(207.27, 12.8) * mm});
            skArc(sketch, "E20.7.13.8", {"start": v(207.27, -33.2) * mm, "mid": v(207.85, -34.62) * mm, "end": v(209.27, -35.2) * mm});
            skPoint(sketch, "E20.11.13.8", {"position": v(217.27, -35.2) * mm});
            skPoint(sketch, "E20.12.13.8", {"position": v(207.27, 14.8) * mm});
            skLineSegment(sketch, "E20.13.13.8", {"start": v(209.27, 14.8) * mm, "end": v(215.27, 14.8) * mm});
            skLineSegment(sketch, "E20.16.13.8", {"start": v(209.27, -35.2) * mm, "end": v(215.27, -35.2) * mm});
            skPoint(sketch, "E20.19.13.8", {"position": v(217.27, 14.8) * mm});
            skArc(sketch, "E20.20.13.8", {"start": v(217.27, 12.8) * mm, "mid": v(216.68, 14.2) * mm, "end": v(215.27, 14.8) * mm});
            skArc(sketch, "E20.24.13.8", {"start": v(215.27, -35.2) * mm, "mid": v(216.68, -34.62) * mm, "end": v(217.27, -33.2) * mm});
            skArc(sketch, "E20.28.13.8", {"start": v(209.27, 14.8) * mm, "mid": v(207.85, 14.2) * mm, "end": v(207.27, 12.8) * mm});
            skLineSegment(sketch, "E20.0.14.8", {"start": v(232.77, -33.2) * mm, "end": v(232.77, 12.8) * mm});
            skPoint(sketch, "E20.3.14.8", {"position": v(222.77, -35.2) * mm});
            skLineSegment(sketch, "E20.4.14.8", {"start": v(222.77, -33.2) * mm, "end": v(222.77, 12.8) * mm});
            skArc(sketch, "E20.7.14.8", {"start": v(222.77, -33.2) * mm, "mid": v(223.35, -34.62) * mm, "end": v(224.77, -35.2) * mm});
            skPoint(sketch, "E20.11.14.8", {"position": v(232.77, -35.2) * mm});
            skPoint(sketch, "E20.12.14.8", {"position": v(222.77, 14.8) * mm});
            skLineSegment(sketch, "E20.13.14.8", {"start": v(224.77, 14.8) * mm, "end": v(230.77, 14.8) * mm});
            skLineSegment(sketch, "E20.16.14.8", {"start": v(224.77, -35.2) * mm, "end": v(230.77, -35.2) * mm});
            skPoint(sketch, "E20.19.14.8", {"position": v(232.77, 14.8) * mm});
            skArc(sketch, "E20.20.14.8", {"start": v(232.77, 12.8) * mm, "mid": v(232.18, 14.2) * mm, "end": v(230.77, 14.8) * mm});
            skArc(sketch, "E20.24.14.8", {"start": v(230.77, -35.2) * mm, "mid": v(232.18, -34.62) * mm, "end": v(232.77, -33.2) * mm});
            skArc(sketch, "E20.28.14.8", {"start": v(224.77, 14.8) * mm, "mid": v(223.35, 14.2) * mm, "end": v(222.77, 12.8) * mm});
            skLineSegment(sketch, "E20.0.15.8", {"start": v(248.27, -33.2) * mm, "end": v(248.27, 12.8) * mm});
            skPoint(sketch, "E20.3.15.8", {"position": v(238.27, -35.2) * mm});
            skLineSegment(sketch, "E20.4.15.8", {"start": v(238.27, -33.2) * mm, "end": v(238.27, 12.8) * mm});
            skArc(sketch, "E20.7.15.8", {"start": v(238.27, -33.2) * mm, "mid": v(238.85, -34.62) * mm, "end": v(240.27, -35.2) * mm});
            skPoint(sketch, "E20.11.15.8", {"position": v(248.27, -35.2) * mm});
            skPoint(sketch, "E20.12.15.8", {"position": v(238.27, 14.8) * mm});
            skLineSegment(sketch, "E20.13.15.8", {"start": v(240.27, 14.8) * mm, "end": v(246.27, 14.8) * mm});
            skLineSegment(sketch, "E20.16.15.8", {"start": v(240.27, -35.2) * mm, "end": v(246.27, -35.2) * mm});
            skPoint(sketch, "E20.19.15.8", {"position": v(248.27, 14.8) * mm});
            skArc(sketch, "E20.20.15.8", {"start": v(248.27, 12.8) * mm, "mid": v(247.68, 14.2) * mm, "end": v(246.27, 14.8) * mm});
            skArc(sketch, "E20.24.15.8", {"start": v(246.27, -35.2) * mm, "mid": v(247.68, -34.62) * mm, "end": v(248.27, -33.2) * mm});
            skArc(sketch, "E20.28.15.8", {"start": v(240.27, 14.8) * mm, "mid": v(238.85, 14.2) * mm, "end": v(238.27, 12.8) * mm});
            skLineSegment(sketch, "E20.0.16.8", {"start": v(263.77, -33.2) * mm, "end": v(263.77, 12.8) * mm});
            skPoint(sketch, "E20.3.16.8", {"position": v(253.77, -35.2) * mm});
            skLineSegment(sketch, "E20.4.16.8", {"start": v(253.77, -33.2) * mm, "end": v(253.77, 12.8) * mm});
            skArc(sketch, "E20.7.16.8", {"start": v(253.77, -33.2) * mm, "mid": v(254.35, -34.62) * mm, "end": v(255.77, -35.2) * mm});
            skPoint(sketch, "E20.11.16.8", {"position": v(263.77, -35.2) * mm});
            skPoint(sketch, "E20.12.16.8", {"position": v(253.77, 14.8) * mm});
            skLineSegment(sketch, "E20.13.16.8", {"start": v(255.77, 14.8) * mm, "end": v(261.77, 14.8) * mm});
            skLineSegment(sketch, "E20.16.16.8", {"start": v(255.77, -35.2) * mm, "end": v(261.77, -35.2) * mm});
            skPoint(sketch, "E20.19.16.8", {"position": v(263.77, 14.8) * mm});
            skArc(sketch, "E20.20.16.8", {"start": v(263.77, 12.8) * mm, "mid": v(263.18, 14.2) * mm, "end": v(261.77, 14.8) * mm});
            skArc(sketch, "E20.24.16.8", {"start": v(261.77, -35.2) * mm, "mid": v(263.18, -34.62) * mm, "end": v(263.77, -33.2) * mm});
            skArc(sketch, "E20.28.16.8", {"start": v(255.77, 14.8) * mm, "mid": v(254.35, 14.2) * mm, "end": v(253.77, 12.8) * mm});
            skLineSegment(sketch, "E20.0.17.8", {"start": v(279.27, -33.2) * mm, "end": v(279.27, 12.8) * mm});
            skPoint(sketch, "E20.3.17.8", {"position": v(269.27, -35.2) * mm});
            skLineSegment(sketch, "E20.4.17.8", {"start": v(269.27, -33.2) * mm, "end": v(269.27, 12.8) * mm});
            skArc(sketch, "E20.7.17.8", {"start": v(269.27, -33.2) * mm, "mid": v(269.85, -34.62) * mm, "end": v(271.27, -35.2) * mm});
            skPoint(sketch, "E20.11.17.8", {"position": v(279.27, -35.2) * mm});
            skPoint(sketch, "E20.12.17.8", {"position": v(269.27, 14.8) * mm});
            skLineSegment(sketch, "E20.13.17.8", {"start": v(271.27, 14.8) * mm, "end": v(277.27, 14.8) * mm});
            skLineSegment(sketch, "E20.16.17.8", {"start": v(271.27, -35.2) * mm, "end": v(277.27, -35.2) * mm});
            skPoint(sketch, "E20.19.17.8", {"position": v(279.27, 14.8) * mm});
            skArc(sketch, "E20.20.17.8", {"start": v(279.27, 12.8) * mm, "mid": v(278.68, 14.2) * mm, "end": v(277.27, 14.8) * mm});
            skArc(sketch, "E20.24.17.8", {"start": v(277.27, -35.2) * mm, "mid": v(278.68, -34.62) * mm, "end": v(279.27, -33.2) * mm});
            skArc(sketch, "E20.28.17.8", {"start": v(271.27, 14.8) * mm, "mid": v(269.85, 14.2) * mm, "end": v(269.27, 12.8) * mm});
            skPoint(sketch, "E20.3.18.8", {"position": v(284.77, -35.2) * mm});
            skPoint(sketch, "E20.11.18.8", {"position": v(294.77, -35.2) * mm});
            skPoint(sketch, "E20.12.18.8", {"position": v(284.77, 14.8) * mm});
            skPoint(sketch, "E20.19.18.8", {"position": v(294.77, 14.8) * mm});
            skSolve(sketch);
        }
        {
            var Q0;
            Q0 = qSketchRegion(id + "F14", true);
            extrude(context, id + "F15", {"entities" : qUnion([Q0]), "operationType" : NewBodyOperationType.REMOVE, "oppositeDirection" : true, "depth" : 62 * mm, "offsetDistance" : 25 * mm, "symmetric" : true});
        }
        {
            var Q0;
            Q0=qCreatedBy(makeId("Top.planeOp"),FACE);
            var sketch = newSketch(context, id + "F16", { "sketchPlane" : qUnion([Q0])});
            skFitSpline(sketch, "E21", {"points": [v(150, 90.64) * mm, v(133.34, 83.75) * mm, v(113.5, 41.87) * mm, v(59.5, 24.24) * mm, v(13.16, 10.16) * mm, v(0, -68.08) * mm], "startDerivative": vector(-186.24, 3.88) * mm, "endDerivative": vector(-20.25, -284.5) * mm});
            skLineSegment(sketch, "E22", {"start": v(150, 191.68) * mm, "end": v(150, -626.98) * mm, "construction": true});
            skFitSpline(sketch, "E23.MirrorCS", {"points": [v(150, 90.64) * mm, v(166.66, 83.75) * mm, v(186.5, 41.87) * mm, v(240.5, 24.24) * mm, v(286.84, 10.16) * mm, v(300, -68.08) * mm], "startDerivative": vector(186.24, 3.88) * mm, "endDerivative": vector(20.25, -284.5) * mm});
            skLineSegment(sketch, "E24", {"start": v(0, -68.08) * mm, "end": v(-38.07, -68.08) * mm});
            skLineSegment(sketch, "E25", {"start": v(-38.07, -68.08) * mm, "end": v(-38.07, 153) * mm});
            skLineSegment(sketch, "E26", {"start": v(-38.07, 153) * mm, "end": v(333.33, 153) * mm});
            skLineSegment(sketch, "E27", {"start": v(333.33, 153) * mm, "end": v(333.33, -68.08) * mm});
            skLineSegment(sketch, "E28", {"start": v(333.33, -68.08) * mm, "end": v(300, -68.08) * mm});
            skSolve(sketch);
        }
        {
            var Q0;
            Q0=makeQuery(id+"F16.imprint","IMPRINT",FACE,{"disambiguationData":[TD([[makeQuery(id+"F16.imprint","IMPRINT",EDGE,{"derivedFrom":sQuery(id+"F16.wireOp",EDGE,"E21")}),-1.0]])]});
            extrude(context, id + "F17", {"entities" : qUnion([Q0]), "operationType" : NewBodyOperationType.REMOVE, "depth" : 159 * mm, "offsetDistance" : 25 * mm});
        }
        {
            var Q0;
            Q0=makeQuery(id+"F17.boolean.opBoolean","INTERSECT",EDGE,{"derivedFrom":[makeQuery(id+"F1.opExtrude","SWEPT_FACE",FACE,{"disambiguationData":[OSD([sQuery(id+"F0.wireOp",EDGE,"E2.2")])]}),makeQuery(id+"F17.opExtrude","SWEPT_FACE",FACE,{"disambiguationData":[OSD([sQuery(id+"F16.wireOp",EDGE,"E21")])]})]});
            var Q1;
            Q1=makeQuery(id+"F17.boolean.opBoolean","INTERSECT",EDGE,{"derivedFrom":[makeQuery(id+"F1.opExtrude","SWEPT_FACE",FACE,{"disambiguationData":[OSD([sQuery(id+"F0.wireOp",EDGE,"E2.2")])]}),makeQuery(id+"F17.opExtrude","SWEPT_FACE",FACE,{"disambiguationData":[OSD([sQuery(id+"F16.wireOp",EDGE,"E23.MirrorCS")])]})]});
            var Q2;
            Q2=makeQuery(id+"F1.opExtrude","SWEPT_FACE",FACE,{"disambiguationData":[OSD([sQuery(id+"F0.wireOp",EDGE,"E4")])]});
            fillet(context, id + "F18", {"entities" : qUnion([Q0, Q1, Q2]), "tangentPropagation" : true, "radius" : 3 * mm, "defaultsChanged" : false, "vertexSettings" : [], "allowEdgeOverflow" : false});
        }
        {
            var Q0;
            Q0=makeQuery(id+"F1.opExtrude","CAP_FACE",FACE,{"disambiguationData":[OSD([sQuery(id+"F0.wireOp",EDGE,"E0"),sQuery(id+"F0.wireOp",EDGE,"E1"),sQuery(id+"F0.wireOp",EDGE,"E2.0"),sQuery(id+"F0.wireOp",EDGE,"E2.2"),sQuery(id+"F0.wireOp",EDGE,"E3"),sQuery(id+"F0.wireOp",EDGE,"E4"),sQuery(id+"F0.wireOp",EDGE,"E5"),sQuery(id+"F0.wireOp",EDGE,"E6")])],"isStart":false});
            var Q1;
            Q1=makeQuery(id+"F17.boolean.opBoolean","INTERSECT",EDGE,{"derivedFrom":[makeQuery(id+"F1.opExtrude","SWEPT_FACE",FACE,{"disambiguationData":[OSD([sQuery(id+"F0.wireOp",EDGE,"E5")])]}),makeQuery(id+"F17.opExtrude","SWEPT_FACE",FACE,{"disambiguationData":[OSD([sQuery(id+"F16.wireOp",EDGE,"E23.MirrorCS")])]})]});
            var Q2;
            Q2=makeQuery(id+"F17.boolean.opBoolean","INTERSECT",EDGE,{"derivedFrom":[makeQuery(id+"F1.opExtrude","SWEPT_FACE",FACE,{"disambiguationData":[OSD([sQuery(id+"F0.wireOp",EDGE,"E6")])]}),makeQuery(id+"F17.opExtrude","SWEPT_FACE",FACE,{"disambiguationData":[OSD([sQuery(id+"F16.wireOp",EDGE,"E23.MirrorCS")])]})]});
            var Q3;
            Q3=makeQuery(id+"F1.opExtrude","CAP_EDGE",EDGE,{"disambiguationData":[OSD([sQuery(id+"F0.wireOp",EDGE,"E5")])],"isStart":true});
            var Q4;
            Q4=makeQuery(id+"F17.boolean.opBoolean","INTERSECT",EDGE,{"derivedFrom":[makeQuery(id+"F1.opExtrude","SWEPT_FACE",FACE,{"disambiguationData":[OSD([sQuery(id+"F0.wireOp",EDGE,"E5")])]}),makeQuery(id+"F17.opExtrude","SWEPT_FACE",FACE,{"disambiguationData":[OSD([sQuery(id+"F16.wireOp",EDGE,"E21")])]})]});
            var Q5;
            Q5=makeQuery(id+"F17.boolean.opBoolean","INTERSECT",EDGE,{"derivedFrom":[makeQuery(id+"F1.opExtrude","SWEPT_FACE",FACE,{"disambiguationData":[OSD([sQuery(id+"F0.wireOp",EDGE,"E6")])]}),makeQuery(id+"F17.opExtrude","SWEPT_FACE",FACE,{"disambiguationData":[OSD([sQuery(id+"F16.wireOp",EDGE,"E21")])]})]});
            var Q6;
            Q6=makeQuery(id+"F17.boolean.opBoolean","INTERSECT",EDGE,{"derivedFrom":[makeQuery(id+"F1.opExtrude","SWEPT_FACE",FACE,{"disambiguationData":[OSD([sQuery(id+"F0.wireOp",EDGE,"E0")])]}),makeQuery(id+"F17.opExtrude","SWEPT_FACE",FACE,{"disambiguationData":[OSD([sQuery(id+"F16.wireOp",EDGE,"E21")])]})]});
            var Q7;
            Q7=makeQuery(id+"F17.boolean.opBoolean","INTERSECT",EDGE,{"derivedFrom":[makeQuery(id+"F1.opExtrude","SWEPT_FACE",FACE,{"disambiguationData":[OSD([sQuery(id+"F0.wireOp",EDGE,"E0")])]}),makeQuery(id+"F17.opExtrude","SWEPT_FACE",FACE,{"disambiguationData":[OSD([sQuery(id+"F16.wireOp",EDGE,"E23.MirrorCS")])]})]});
            fillet(context, id + "F19", {"entities" : qUnion([Q0, Q1, Q2, Q3, Q4, Q5, Q6, Q7]), "tangentPropagation" : true, "radius" : 2 * mm, "defaultsChanged" : false, "vertexSettings" : [], "allowEdgeOverflow" : false});
        }
    });
